FCSTD DOCUMENT  (FreeCAD 0.20R29410 (Git))
Label: SRSv1_0
License: All rights reserved
LicenseURL: http://en.wikipedia.org/wiki/All_rights_reserved
objects: Part::Feature×157, Sketcher::SketchObject×90, App::Part×59, Part::MultiFuse×49, Part::Cylinder×49, Part::Fillet×48, Part::Cut×36, Part::Loft×34, Part::Extrusion×19, Part::Sphere×4, Part::Box×2, Part::MultiCommon×1, Part::Compound×1
note: 490 computed .brp shape members not serialized (recipe doc carries the construction recipe); baked Part::Feature solids carry a one-line shape summary decoded from their .brp

FEATURE [Part::Feature] Part__Feature049  label="T-SlottedFramingScew"
  Placement = pos=(-0.00808436,-263.233,14.5255) rot=(0.577273,-0.577389,-0.577389;2.09434rad)
  shape: bbox 11.25 x 25.4 x 17.44 mm, 56 faces, 2 solids (baked)
FEATURE [Part::Feature] Part__Feature022  label="3136N138_T-Slotted Framing"
  shape: bbox 101.6 x 133.4 x 139.7 mm, 136 faces (baked)
FEATURE [Part::Feature] Part__Feature023  label="47065T801_T-Slotted Framing"
  Placement = pos=(0,100,0) rot=(-1,0,0;1.5708rad)
  shape: bbox 25.4 x 152.4 x 25.4 mm, 108 faces (baked)
FEATURE [Part::Feature] Part__Feature024  label="47065T801_T-Slotted Framing001"
  Placement = pos=(0,200,0) rot=(-1,0,0;1.5708rad)
  shape: bbox 25.4 x 152.4 x 25.4 mm, 108 faces (baked)
FEATURE [Part::MultiFuse] Fusion008  label="framingSupport"
  Placement = pos=(0,0,-3) rot=(0,0,1;3.14159rad)
  Shapes = -> [Part__Feature024,Part__Feature022,Part__Feature023]
FEATURE [Part::Box] Box  label="Cube"
  AttacherType = Attacher::AttachEngine3D
  Height = 12
  Length = 24
  Placement = pos=(-12,-341.5,-244.5) rot=(0,0,1;0rad)
  Width = 23
FEATURE [Part::Box] Box042  label="Cube030"
  AttacherType = Attacher::AttachEngine3D
  Height = 50
  Length = 25
  Placement = pos=(-11,-309,-310) rot=(0,0,1;0rad)
  Width = 25
FEATURE [Part::Cylinder] Cylinder
  Angle = 360
  AttacherType = Attacher::AttachEngine3D
  FirstAngle = 0
  Height = 15
  Placement = pos=(0,-287.79,-241.35) rot=(1,0,0;0.698132rad)
  Radius = 1.63
  SecondAngle = 0
FEATURE [Part::Cylinder] Cylinder128  label="base013"
  Angle = 360
  AttacherType = Attacher::AttachEngine3D
  FirstAngle = 0
  Height = 4.5
  Placement = pos=(136,0,65) rot=(0,0,1;0rad)
  Radius = 40
  SecondAngle = 0
FEATURE [Part::Cylinder] Cylinder129  label="baseCut002"
  Angle = 360
  AttacherType = Attacher::AttachEngine3D
  FirstAngle = 0
  Height = 7
  Placement = pos=(5,0,74) rot=(0,0,1;0rad)
  Radius = 24
  SecondAngle = 0
FEATURE [Part::Cylinder] Cylinder130
  Angle = 360
  AttacherType = Attacher::AttachEngine3D
  FirstAngle = 0
  Height = 1
  Placement = pos=(134,32.6,65) rot=(0,0,1;0rad)
  Radius = 5.5
  SecondAngle = 0
FEATURE [Part::Cylinder] Cylinder131
  Angle = 360
  AttacherType = Attacher::AttachEngine3D
  FirstAngle = 0
  Height = 5.82
  Placement = pos=(0,-21,0) rot=(0,0,1;0rad)
  Radius = 5
  SecondAngle = 0
FEATURE [Part::Cylinder] Cylinder132
  Angle = 360
  AttacherType = Attacher::AttachEngine3D
  FirstAngle = 0
  Height = 5.82
  Placement = pos=(20.5,-21,0) rot=(0,0,1;0rad)
  Radius = 5
  SecondAngle = 0
  expr: Radius = 5
FEATURE [Part::Cylinder] Cylinder133
  Angle = 360
  AttacherType = Attacher::AttachEngine3D
  FirstAngle = 0
  Height = 5.82
  Placement = pos=(0,-21,0) rot=(0,0,1;0rad)
  Radius = 5
  SecondAngle = 0
FEATURE [Part::Cylinder] Cylinder134
  Angle = 360
  AttacherType = Attacher::AttachEngine3D
  FirstAngle = 0
  Height = 5.82
  Placement = pos=(20.5,-21,0) rot=(0,0,1;0rad)
  Radius = 5
  SecondAngle = 0
FEATURE [Part::Cylinder] Cylinder139
  Angle = 360
  AttacherType = Attacher::AttachEngine3D
  FirstAngle = 0
  Height = 10
  Placement = pos=(0,-21,0) rot=(0,0,1;0rad)
  Radius = 2
  SecondAngle = 0
FEATURE [Part::Cylinder] Cylinder140
  Angle = 360
  AttacherType = Attacher::AttachEngine3D
  FirstAngle = 0
  Height = 10
  Placement = pos=(20.5,-21,0) rot=(0,0,1;0rad)
  Radius = 2
  SecondAngle = 0
FEATURE [Part::Cylinder] Cylinder141
  Angle = 360
  AttacherType = Attacher::AttachEngine3D
  FirstAngle = 0
  Height = 10
  Placement = pos=(0,-21,0) rot=(0,0,1;0rad)
  Radius = 2
  SecondAngle = 0
FEATURE [Part::Cylinder] Cylinder142
  Angle = 360
  AttacherType = Attacher::AttachEngine3D
  FirstAngle = 0
  Height = 10
  Placement = pos=(20.5,-21,0) rot=(0,0,1;0rad)
  Radius = 2
  SecondAngle = 0
FEATURE [Part::Cylinder] Cylinder143  label="WireCut003"
  Angle = 360
  AttacherType = Attacher::AttachEngine3D
  FirstAngle = 0
  Height = 60
  Placement = pos=(134,32.6,20) rot=(0,0,1;0rad)
  Radius = 2.5
  SecondAngle = 0
FEATURE [Part::Cylinder] Cylinder146
  Angle = 360
  AttacherType = Attacher::AttachEngine3D
  FirstAngle = 0
  Height = 50
  Placement = pos=(0,-302.012,-276.116) rot=(1,0,0;0.733038rad)
  Radius = 8
  SecondAngle = 0
FEATURE [Part::Cut] Cut039
  Base = -> Cylinder146
  Tool = -> Box
FEATURE [Part::Cylinder] Cylinder147  label="cut"
  Angle = 360
  AttacherType = Attacher::AttachEngine3D
  FirstAngle = 0
  Height = 50
  Placement = pos=(0,-300.005,-278.345) rot=(1,0,0;0.733038rad)
  Radius = 5
  SecondAngle = 0
FEATURE [Part::Cylinder] Cylinder148  label="m2HeatSetInsets016"
  Angle = 360
  AttacherType = Attacher::AttachEngine3D
  FirstAngle = 0
  Height = 10
  Placement = pos=(-35,0,65) rot=(0,0,1;0rad)
  Radius = 2
  SecondAngle = 0
  expr: Radius = 2
FEATURE [Part::Cylinder] Cylinder149  label="m2HeatSetInsets017"
  Angle = 360
  AttacherType = Attacher::AttachEngine3D
  FirstAngle = 0
  Height = 10
  Placement = pos=(35,0,65) rot=(0,0,1;0rad)
  Radius = 2
  SecondAngle = 0
FEATURE [Part::Cylinder] Cylinder150  label="m2HeatSetInsets018"
  Angle = 360
  AttacherType = Attacher::AttachEngine3D
  FirstAngle = 0
  Height = 10
  Placement = pos=(0,35,65) rot=(0,0,1;0rad)
  Radius = 2
  SecondAngle = 0
FEATURE [Part::Cylinder] Cylinder151  label="m2HeatSetInsets019"
  Angle = 360
  AttacherType = Attacher::AttachEngine3D
  FirstAngle = 0
  Height = 10
  Placement = pos=(0,-35,65) rot=(0,0,1;0rad)
  Radius = 2
  SecondAngle = 0
  expr: Radius = 2
FEATURE [Part::MultiFuse] Fusion079  label="m3HeatSetCuts015"
  Placement = pos=(-5,39,70) rot=(0,0,1;0rad)
  Shapes = -> [Cylinder132,Cylinder131]
FEATURE [Part::MultiFuse] Fusion080  label="m3HeatSetCuts016"
  Placement = pos=(-5,3,70) rot=(0,0,1;0rad)
  Shapes = -> [Cylinder134,Cylinder133]
FEATURE [Part::MultiFuse] Fusion081  label="m3HeatSetCuts017"
  Placement = pos=(128.75,10,-1) rot=(0,0,1;0rad)
  Shapes = -> [Fusion080,Fusion079]
FEATURE [Part::MultiFuse] Fusion086  label="m3HeatSetCuts019"
  Placement = pos=(-5,39,70) rot=(0,0,1;0rad)
  Shapes = -> [Cylinder140,Cylinder139]
FEATURE [Part::MultiFuse] Fusion087  label="m3HeatSetCuts020"
  Placement = pos=(-5,3,70) rot=(0,0,1;0rad)
  Shapes = -> [Cylinder142,Cylinder141]
FEATURE [Part::MultiFuse] Fusion085  label="m3HeatSetCuts018"
  Placement = pos=(128.75,10,-1) rot=(0,0,1;0rad)
  Shapes = -> [Fusion087,Fusion086]
FEATURE [Part::MultiFuse] Fusion088  label="lightModuleCut004"
  Shapes = -> [Fusion085,Cylinder143]
FEATURE [Part::MultiFuse] Fusion092
  Placement = pos=(0,-350,-314) rot=(0,0,-1;0.785398rad)
  Shapes = -> [Cylinder148,Cylinder149,Cylinder150,Cylinder151]
FEATURE [Part::Feature] Part__Feature153  label="logoTopCut"
  Placement = pos=(-30.8,-333,-323.9) rot=(0,0,1;0rad)
  shape: bbox 22.79 x 8 x 17.08 mm, 886 faces (baked)
FEATURE [Sketcher::SketchObject] Sketch003  label="inner"
  FullyConstrained = true
  Placement = pos=(0,0,-259.26) rot=(0,0,1;0rad)
  sketch-geometry (4):
    g0: LineSegment StartX=-30 StartY=-277 StartZ=0 EndX=-30 EndY=-327 EndZ=0
    g1: LineSegment StartX=-30 StartY=-327 StartZ=0 EndX=30 EndY=-327 EndZ=0
    g2: LineSegment StartX=30 StartY=-327 StartZ=0 EndX=30 EndY=-277 EndZ=0
    g3: LineSegment StartX=30 StartY=-277 StartZ=0 EndX=-30 EndY=-277 EndZ=0
  constraints (12):
    c: Vertical(g0)
    c: Coincident(g1,g0)
    c: Horizontal(g1)
    c: Coincident(g2,g1)
    c: Vertical(g2)
    c: Coincident(g3,g2)
    c: Coincident(g3,g0)
    c: Horizontal(g3)
    c: DistanceX(g0) = -30
    c: DistanceX(g1) = 30
    c: DistanceY(g0) = -327
    c: DistanceY(g0,g0) = 50
FEATURE [Sketcher::SketchObject] Sketch004  label="outer"
  FullyConstrained = true
  Placement = pos=(0,0,-281.2) rot=(0,0,1;0rad)
  sketch-geometry (4):
    g0: LineSegment StartX=-59 StartY=-252 StartZ=0 EndX=-59 EndY=-352 EndZ=0
    g1: LineSegment StartX=-59 StartY=-352 StartZ=0 EndX=59 EndY=-352 EndZ=0
    g2: LineSegment StartX=59 StartY=-352 StartZ=0 EndX=59 EndY=-252 EndZ=0
    g3: LineSegment StartX=59 StartY=-252 StartZ=0 EndX=-59 EndY=-252 EndZ=0
  constraints (12):
    c: Vertical(g0)
    c: Coincident(g1,g0)
    c: Horizontal(g1)
    c: Coincident(g2,g1)
    c: Vertical(g2)
    c: Coincident(g3,g2)
    c: Coincident(g3,g0)
    c: Horizontal(g3)
    c: DistanceX(g0) = -59
    c: DistanceX(g1) = 59
    c: DistanceY(g0) = -352
    c: DistanceY(g0,g0) = 100
FEATURE [Part::Loft] Loft
  Closed = false
  MaxDegree = 5
  Ruled = false
  Sections = -> [Sketch003,Sketch004]
  Solid = true
FEATURE [Part::Fillet] Fillet
  Base = -> Loft
  Edges = 12 edges r=3: [Edge1,Edge2,Edge3,Edge4,Edge5,Edge6,Edge7,Edge8,Edge9,Edge10,Edge11,Edge12]
FEATURE [Sketcher::SketchObject] Sketch005  label="inner001"
  FullyConstrained = true
  Placement = pos=(0,0,-259.26) rot=(0,0,1;0rad)
  sketch-geometry (4):
    g0: LineSegment StartX=-30 StartY=-277 StartZ=0 EndX=-30 EndY=-327 EndZ=0
    g1: LineSegment StartX=-30 StartY=-327 StartZ=0 EndX=30 EndY=-327 EndZ=0
    g2: LineSegment StartX=30 StartY=-327 StartZ=0 EndX=30 EndY=-277 EndZ=0
    g3: LineSegment StartX=30 StartY=-277 StartZ=0 EndX=-30 EndY=-277 EndZ=0
  constraints (12):
    c: Vertical(g0)
    c: Coincident(g1,g0)
    c: Horizontal(g1)
    c: Coincident(g2,g1)
    c: Vertical(g2)
    c: Coincident(g3,g2)
    c: Coincident(g3,g0)
    c: Horizontal(g3)
    c: DistanceX(g0) = -30
    c: DistanceX(g1) = 30
    c: DistanceY(g0) = -327
    c: DistanceY(g0,g0) = 50
FEATURE [Sketcher::SketchObject] Sketch006  label="outer001"
  FullyConstrained = true
  Placement = pos=(0,0,-281.2) rot=(0,0,1;0rad)
  sketch-geometry (4):
    g0: LineSegment StartX=-59 StartY=-252 StartZ=0 EndX=-59 EndY=-352 EndZ=0
    g1: LineSegment StartX=-59 StartY=-352 StartZ=0 EndX=59 EndY=-352 EndZ=0
    g2: LineSegment StartX=59 StartY=-352 StartZ=0 EndX=59 EndY=-252 EndZ=0
    g3: LineSegment StartX=59 StartY=-252 StartZ=0 EndX=-59 EndY=-252 EndZ=0
  constraints (12):
    c: Vertical(g0)
    c: Coincident(g1,g0)
    c: Horizontal(g1)
    c: Coincident(g2,g1)
    c: Vertical(g2)
    c: Coincident(g3,g2)
    c: Coincident(g3,g0)
    c: Horizontal(g3)
    c: DistanceX(g0) = -59
    c: DistanceX(g1) = 59
    c: DistanceY(g0) = -352
    c: DistanceY(g0,g0) = 100
FEATURE [Part::Loft] Loft001
  Closed = false
  MaxDegree = 5
  Ruled = false
  Sections = -> [Sketch005,Sketch006]
  Solid = true
FEATURE [Part::Fillet] Fillet009
  Base = -> Loft001
  Edges = 12 edges r=3: [Edge1,Edge2,Edge3,Edge4,Edge5,Edge6,Edge7,Edge8,Edge9,Edge10,Edge11,Edge12]
  Placement = pos=(0,0,-4) rot=(0,0,1;0rad)
FEATURE [Part::Cut] Cut  label="sls01"
  Base = -> Fillet
  Tool = -> Fillet009
FEATURE [Sketcher::SketchObject] Sketch007  label="inner002"
  FullyConstrained = true
  Placement = pos=(0,0,-259.26) rot=(0,0,1;0rad)
  sketch-geometry (4):
    g0: LineSegment StartX=-30 StartY=-277 StartZ=0 EndX=-30 EndY=-327 EndZ=0
    g1: LineSegment StartX=-30 StartY=-327 StartZ=0 EndX=30 EndY=-327 EndZ=0
    g2: LineSegment StartX=30 StartY=-327 StartZ=0 EndX=30 EndY=-277 EndZ=0
    g3: LineSegment StartX=30 StartY=-277 StartZ=0 EndX=-30 EndY=-277 EndZ=0
  constraints (12):
    c: Vertical(g0)
    c: Coincident(g1,g0)
    c: Horizontal(g1)
    c: Coincident(g2,g1)
    c: Vertical(g2)
    c: Coincident(g3,g2)
    c: Coincident(g3,g0)
    c: Horizontal(g3)
    c: DistanceX(g0) = -30
    c: DistanceX(g1) = 30
    c: DistanceY(g0) = -327
    c: DistanceY(g0,g0) = 50
FEATURE [Sketcher::SketchObject] Sketch008  label="outer002"
  FullyConstrained = true
  Placement = pos=(0,0,-281.2) rot=(0,0,1;0rad)
  sketch-geometry (4):
    g0: LineSegment StartX=-59 StartY=-252 StartZ=0 EndX=-59 EndY=-352 EndZ=0
    g1: LineSegment StartX=-59 StartY=-352 StartZ=0 EndX=59 EndY=-352 EndZ=0
    g2: LineSegment StartX=59 StartY=-352 StartZ=0 EndX=59 EndY=-252 EndZ=0
    g3: LineSegment StartX=59 StartY=-252 StartZ=0 EndX=-59 EndY=-252 EndZ=0
  constraints (12):
    c: Vertical(g0)
    c: Coincident(g1,g0)
    c: Horizontal(g1)
    c: Coincident(g2,g1)
    c: Vertical(g2)
    c: Coincident(g3,g2)
    c: Coincident(g3,g0)
    c: Horizontal(g3)
    c: DistanceX(g0) = -59
    c: DistanceX(g1) = 59
    c: DistanceY(g0) = -352
    c: DistanceY(g0,g0) = 100
FEATURE [Part::Loft] Loft002
  Closed = false
  MaxDegree = 5
  Ruled = false
  Sections = -> [Sketch007,Sketch008]
  Solid = true
FEATURE [Part::Fillet] Fillet010
  Base = -> Loft002
  Edges = 12 edges r=3: [Edge1,Edge2,Edge3,Edge4,Edge5,Edge6,Edge7,Edge8,Edge9,Edge10,Edge11,Edge12]
FEATURE [Sketcher::SketchObject] Sketch009  label="inner003"
  FullyConstrained = true
  Placement = pos=(0,0,-259.26) rot=(0,0,1;0rad)
  sketch-geometry (4):
    g0: LineSegment StartX=-30 StartY=-277 StartZ=0 EndX=-30 EndY=-327 EndZ=0
    g1: LineSegment StartX=-30 StartY=-327 StartZ=0 EndX=30 EndY=-327 EndZ=0
    g2: LineSegment StartX=30 StartY=-327 StartZ=0 EndX=30 EndY=-277 EndZ=0
    g3: LineSegment StartX=30 StartY=-277 StartZ=0 EndX=-30 EndY=-277 EndZ=0
  constraints (12):
    c: Vertical(g0)
    c: Coincident(g1,g0)
    c: Horizontal(g1)
    c: Coincident(g2,g1)
    c: Vertical(g2)
    c: Coincident(g3,g2)
    c: Coincident(g3,g0)
    c: Horizontal(g3)
    c: DistanceX(g0) = -30
    c: DistanceX(g1) = 30
    c: DistanceY(g0) = -327
    c: DistanceY(g0,g0) = 50
FEATURE [Sketcher::SketchObject] Sketch010  label="outer003"
  FullyConstrained = true
  Placement = pos=(0,0,-281.2) rot=(0,0,1;0rad)
  sketch-geometry (4):
    g0: LineSegment StartX=-59 StartY=-252 StartZ=0 EndX=-59 EndY=-352 EndZ=0
    g1: LineSegment StartX=-59 StartY=-352 StartZ=0 EndX=59 EndY=-352 EndZ=0
    g2: LineSegment StartX=59 StartY=-352 StartZ=0 EndX=59 EndY=-252 EndZ=0
    g3: LineSegment StartX=59 StartY=-252 StartZ=0 EndX=-59 EndY=-252 EndZ=0
  constraints (12):
    c: Vertical(g0)
    c: Coincident(g1,g0)
    c: Horizontal(g1)
    c: Coincident(g2,g1)
    c: Vertical(g2)
    c: Coincident(g3,g2)
    c: Coincident(g3,g0)
    c: Horizontal(g3)
    c: DistanceX(g0) = -59
    c: DistanceX(g1) = 59
    c: DistanceY(g0) = -352
    c: DistanceY(g0,g0) = 100
FEATURE [Part::Loft] Loft003
  Closed = false
  MaxDegree = 5
  Ruled = false
  Sections = -> [Sketch009,Sketch010]
  Solid = true
FEATURE [Part::Fillet] Fillet011
  Base = -> Loft003
  Edges = 12 edges r=3: [Edge1,Edge2,Edge3,Edge4,Edge5,Edge6,Edge7,Edge8,Edge9,Edge10,Edge11,Edge12]
  Placement = pos=(0,0,-4) rot=(0,0,1;0rad)
FEATURE [Part::Cut] Cut004  label="sls002"
  Base = -> Fillet010
  Placement = pos=(0,0,-16) rot=(0,0,1;0rad)
  Tool = -> Fillet011
FEATURE [Sketcher::SketchObject] Sketch011  label="inner004"
  FullyConstrained = true
  Placement = pos=(0,0,-259.26) rot=(0,0,1;0rad)
  sketch-geometry (4):
    g0: LineSegment StartX=-30 StartY=-277 StartZ=0 EndX=-30 EndY=-327 EndZ=0
    g1: LineSegment StartX=-30 StartY=-327 StartZ=0 EndX=30 EndY=-327 EndZ=0
    g2: LineSegment StartX=30 StartY=-327 StartZ=0 EndX=30 EndY=-277 EndZ=0
    g3: LineSegment StartX=30 StartY=-277 StartZ=0 EndX=-30 EndY=-277 EndZ=0
  constraints (12):
    c: Vertical(g0)
    c: Coincident(g1,g0)
    c: Horizontal(g1)
    c: Coincident(g2,g1)
    c: Vertical(g2)
    c: Coincident(g3,g2)
    c: Coincident(g3,g0)
    c: Horizontal(g3)
    c: DistanceX(g0) = -30
    c: DistanceX(g1) = 30
    c: DistanceY(g0) = -327
    c: DistanceY(g0,g0) = 50
FEATURE [Sketcher::SketchObject] Sketch012  label="outer004"
  FullyConstrained = true
  Placement = pos=(0,0,-281.2) rot=(0,0,1;0rad)
  sketch-geometry (4):
    g0: LineSegment StartX=-59 StartY=-252 StartZ=0 EndX=-59 EndY=-352 EndZ=0
    g1: LineSegment StartX=-59 StartY=-352 StartZ=0 EndX=59 EndY=-352 EndZ=0
    g2: LineSegment StartX=59 StartY=-352 StartZ=0 EndX=59 EndY=-252 EndZ=0
    g3: LineSegment StartX=59 StartY=-252 StartZ=0 EndX=-59 EndY=-252 EndZ=0
  constraints (12):
    c: Vertical(g0)
    c: Coincident(g1,g0)
    c: Horizontal(g1)
    c: Coincident(g2,g1)
    c: Vertical(g2)
    c: Coincident(g3,g2)
    c: Coincident(g3,g0)
    c: Horizontal(g3)
    c: DistanceX(g0) = -59
    c: DistanceX(g1) = 59
    c: DistanceY(g0) = -352
    c: DistanceY(g0,g0) = 100
FEATURE [Part::Loft] Loft004
  Closed = false
  MaxDegree = 5
  Ruled = false
  Sections = -> [Sketch011,Sketch012]
  Solid = true
FEATURE [Part::Fillet] Fillet012
  Base = -> Loft004
  Edges = 12 edges r=3: [Edge1,Edge2,Edge3,Edge4,Edge5,Edge6,Edge7,Edge8,Edge9,Edge10,Edge11,Edge12]
FEATURE [Sketcher::SketchObject] Sketch013  label="inner005"
  FullyConstrained = true
  Placement = pos=(0,0,-259.26) rot=(0,0,1;0rad)
  sketch-geometry (4):
    g0: LineSegment StartX=-30 StartY=-277 StartZ=0 EndX=-30 EndY=-327 EndZ=0
    g1: LineSegment StartX=-30 StartY=-327 StartZ=0 EndX=30 EndY=-327 EndZ=0
    g2: LineSegment StartX=30 StartY=-327 StartZ=0 EndX=30 EndY=-277 EndZ=0
    g3: LineSegment StartX=30 StartY=-277 StartZ=0 EndX=-30 EndY=-277 EndZ=0
  constraints (12):
    c: Vertical(g0)
    c: Coincident(g1,g0)
    c: Horizontal(g1)
    c: Coincident(g2,g1)
    c: Vertical(g2)
    c: Coincident(g3,g2)
    c: Coincident(g3,g0)
    c: Horizontal(g3)
    c: DistanceX(g0) = -30
    c: DistanceX(g1) = 30
    c: DistanceY(g0) = -327
    c: DistanceY(g0,g0) = 50
FEATURE [Sketcher::SketchObject] Sketch014  label="outer005"
  FullyConstrained = true
  Placement = pos=(0,0,-281.2) rot=(0,0,1;0rad)
  sketch-geometry (4):
    g0: LineSegment StartX=-59 StartY=-252 StartZ=0 EndX=-59 EndY=-352 EndZ=0
    g1: LineSegment StartX=-59 StartY=-352 StartZ=0 EndX=59 EndY=-352 EndZ=0
    g2: LineSegment StartX=59 StartY=-352 StartZ=0 EndX=59 EndY=-252 EndZ=0
    g3: LineSegment StartX=59 StartY=-252 StartZ=0 EndX=-59 EndY=-252 EndZ=0
  constraints (12):
    c: Vertical(g0)
    c: Coincident(g1,g0)
    c: Horizontal(g1)
    c: Coincident(g2,g1)
    c: Vertical(g2)
    c: Coincident(g3,g2)
    c: Coincident(g3,g0)
    c: Horizontal(g3)
    c: DistanceX(g0) = -59
    c: DistanceX(g1) = 59
    c: DistanceY(g0) = -352
    c: DistanceY(g0,g0) = 100
FEATURE [Part::Loft] Loft005
  Closed = false
  MaxDegree = 5
  Ruled = false
  Sections = -> [Sketch013,Sketch014]
  Solid = true
FEATURE [Part::Fillet] Fillet013
  Base = -> Loft005
  Edges = 12 edges r=3: [Edge1,Edge2,Edge3,Edge4,Edge5,Edge6,Edge7,Edge8,Edge9,Edge10,Edge11,Edge12]
  Placement = pos=(0,0,-4) rot=(0,0,1;0rad)
FEATURE [Part::Cut] Cut005  label="sls003"
  Base = -> Fillet012
  Placement = pos=(0,0,-32) rot=(0,0,1;0rad)
  Tool = -> Fillet013
FEATURE [Sketcher::SketchObject] Sketch015  label="inner006"
  FullyConstrained = true
  Placement = pos=(0,0,-259.26) rot=(0,0,1;0rad)
  sketch-geometry (4):
    g0: LineSegment StartX=-30 StartY=-277 StartZ=0 EndX=-30 EndY=-327 EndZ=0
    g1: LineSegment StartX=-30 StartY=-327 StartZ=0 EndX=30 EndY=-327 EndZ=0
    g2: LineSegment StartX=30 StartY=-327 StartZ=0 EndX=30 EndY=-277 EndZ=0
    g3: LineSegment StartX=30 StartY=-277 StartZ=0 EndX=-30 EndY=-277 EndZ=0
  constraints (12):
    c: Vertical(g0)
    c: Coincident(g1,g0)
    c: Horizontal(g1)
    c: Coincident(g2,g1)
    c: Vertical(g2)
    c: Coincident(g3,g2)
    c: Coincident(g3,g0)
    c: Horizontal(g3)
    c: DistanceX(g0) = -30
    c: DistanceX(g1) = 30
    c: DistanceY(g0) = -327
    c: DistanceY(g0,g0) = 50
FEATURE [Sketcher::SketchObject] Sketch016  label="outer006"
  FullyConstrained = true
  Placement = pos=(0,0,-281.2) rot=(0,0,1;0rad)
  sketch-geometry (4):
    g0: LineSegment StartX=-59 StartY=-252 StartZ=0 EndX=-59 EndY=-352 EndZ=0
    g1: LineSegment StartX=-59 StartY=-352 StartZ=0 EndX=59 EndY=-352 EndZ=0
    g2: LineSegment StartX=59 StartY=-352 StartZ=0 EndX=59 EndY=-252 EndZ=0
    g3: LineSegment StartX=59 StartY=-252 StartZ=0 EndX=-59 EndY=-252 EndZ=0
  constraints (12):
    c: Vertical(g0)
    c: Coincident(g1,g0)
    c: Horizontal(g1)
    c: Coincident(g2,g1)
    c: Vertical(g2)
    c: Coincident(g3,g2)
    c: Coincident(g3,g0)
    c: Horizontal(g3)
    c: DistanceX(g0) = -59
    c: DistanceX(g1) = 59
    c: DistanceY(g0) = -352
    c: DistanceY(g0,g0) = 100
FEATURE [Part::Loft] Loft006
  Closed = false
  MaxDegree = 5
  Ruled = false
  Sections = -> [Sketch015,Sketch016]
  Solid = true
FEATURE [Part::Fillet] Fillet014
  Base = -> Loft006
  Edges = 12 edges r=3: [Edge1,Edge2,Edge3,Edge4,Edge5,Edge6,Edge7,Edge8,Edge9,Edge10,Edge11,Edge12]
FEATURE [Sketcher::SketchObject] Sketch017  label="inner007"
  FullyConstrained = true
  Placement = pos=(0,0,-259.26) rot=(0,0,1;0rad)
  sketch-geometry (4):
    g0: LineSegment StartX=-30 StartY=-277 StartZ=0 EndX=-30 EndY=-327 EndZ=0
    g1: LineSegment StartX=-30 StartY=-327 StartZ=0 EndX=30 EndY=-327 EndZ=0
    g2: LineSegment StartX=30 StartY=-327 StartZ=0 EndX=30 EndY=-277 EndZ=0
    g3: LineSegment StartX=30 StartY=-277 StartZ=0 EndX=-30 EndY=-277 EndZ=0
  constraints (12):
    c: Vertical(g0)
    c: Coincident(g1,g0)
    c: Horizontal(g1)
    c: Coincident(g2,g1)
    c: Vertical(g2)
    c: Coincident(g3,g2)
    c: Coincident(g3,g0)
    c: Horizontal(g3)
    c: DistanceX(g0) = -30
    c: DistanceX(g1) = 30
    c: DistanceY(g0) = -327
    c: DistanceY(g0,g0) = 50
FEATURE [Sketcher::SketchObject] Sketch018  label="outer007"
  FullyConstrained = true
  Placement = pos=(0,0,-281.2) rot=(0,0,1;0rad)
  sketch-geometry (4):
    g0: LineSegment StartX=-59 StartY=-252 StartZ=0 EndX=-59 EndY=-352 EndZ=0
    g1: LineSegment StartX=-59 StartY=-352 StartZ=0 EndX=59 EndY=-352 EndZ=0
    g2: LineSegment StartX=59 StartY=-352 StartZ=0 EndX=59 EndY=-252 EndZ=0
    g3: LineSegment StartX=59 StartY=-252 StartZ=0 EndX=-59 EndY=-252 EndZ=0
  constraints (12):
    c: Vertical(g0)
    c: Coincident(g1,g0)
    c: Horizontal(g1)
    c: Coincident(g2,g1)
    c: Vertical(g2)
    c: Coincident(g3,g2)
    c: Coincident(g3,g0)
    c: Horizontal(g3)
    c: DistanceX(g0) = -59
    c: DistanceX(g1) = 59
    c: DistanceY(g0) = -352
    c: DistanceY(g0,g0) = 100
FEATURE [Part::Loft] Loft007
  Closed = false
  MaxDegree = 5
  Ruled = false
  Sections = -> [Sketch017,Sketch018]
  Solid = true
FEATURE [Part::Fillet] Fillet015
  Base = -> Loft007
  Edges = 12 edges r=3: [Edge1,Edge2,Edge3,Edge4,Edge5,Edge6,Edge7,Edge8,Edge9,Edge10,Edge11,Edge12]
  Placement = pos=(0,0,-4) rot=(0,0,1;0rad)
FEATURE [Part::Cut] Cut006  label="sls004"
  Base = -> Fillet014
  Placement = pos=(0,0,-48) rot=(0,0,1;0rad)
  Tool = -> Fillet015
FEATURE [Part::MultiFuse] Fusion036  label="slsBottom"
  Shapes = -> [Cut006,Cut005]
FEATURE [Sketcher::SketchObject] Sketch023
  FullyConstrained = true
  sketch-geometry (4):
    g0: Circle CenterX=-35 CenterY=-332 CenterZ=0 NormalX=0 NormalY=0 NormalZ=1 AngleXU=0 Radius=5.5
    g1: Circle CenterX=35 CenterY=-332 CenterZ=0 NormalX=0 NormalY=0 NormalZ=1 AngleXU=0 Radius=5.5
    g2: Circle CenterX=35 CenterY=-272 CenterZ=0 NormalX=0 NormalY=0 NormalZ=1 AngleXU=0 Radius=5.5
    g3: Circle CenterX=-35 CenterY=-272 CenterZ=0 NormalX=0 NormalY=0 NormalZ=1 AngleXU=0 Radius=5.5
  constraints (12):
    c: DistanceX(g0) = -35
    c: DistanceY(g0) = -332
    c: Equal(g0,g3)
    c: Equal(g0,g2)
    c: Equal(g0,g1)
    c: Diameter(g0) = 11
    c: DistanceX(g3,g0) = 0
    c: DistanceY(g0,g3) = 60
    c: DistanceY(g2,g3) = 0
    c: DistanceY(g0,g1) = 0
    c: DistanceX(g2,g1) = 0
    c: DistanceX(g1) = 35
FEATURE [Part::Extrusion] Extrude007  label="stands"
  Base = -> Sketch023
  Dir = (0,0,1)
  DirMode = 2
  FaceMakerClass = Part::FaceMakerBullseye
  LengthFwd = 69
  LengthRev = 0
  Placement = pos=(0,0,-323) rot=(0,0,1;0rad)
  Solid = true
  Symmetric = false
FEATURE [Sketcher::SketchObject] Sketch024  label="inner008"
  FullyConstrained = true
  Placement = pos=(0,0,-259.26) rot=(0,0,1;0rad)
  sketch-geometry (4):
    g0: LineSegment StartX=-30 StartY=-277 StartZ=0 EndX=-30 EndY=-327 EndZ=0
    g1: LineSegment StartX=-30 StartY=-327 StartZ=0 EndX=30 EndY=-327 EndZ=0
    g2: LineSegment StartX=30 StartY=-327 StartZ=0 EndX=30 EndY=-277 EndZ=0
    g3: LineSegment StartX=30 StartY=-277 StartZ=0 EndX=-30 EndY=-277 EndZ=0
  constraints (12):
    c: Vertical(g0)
    c: Coincident(g1,g0)
    c: Horizontal(g1)
    c: Coincident(g2,g1)
    c: Vertical(g2)
    c: Coincident(g3,g2)
    c: Coincident(g3,g0)
    c: Horizontal(g3)
    c: DistanceX(g0) = -30
    c: DistanceX(g1) = 30
    c: DistanceY(g0) = -327
    c: DistanceY(g0,g0) = 50
FEATURE [Sketcher::SketchObject] Sketch025  label="outer008"
  FullyConstrained = true
  Placement = pos=(0,0,-281.2) rot=(0,0,1;0rad)
  sketch-geometry (4):
    g0: LineSegment StartX=-59 StartY=-252 StartZ=0 EndX=-59 EndY=-352 EndZ=0
    g1: LineSegment StartX=-59 StartY=-352 StartZ=0 EndX=59 EndY=-352 EndZ=0
    g2: LineSegment StartX=59 StartY=-352 StartZ=0 EndX=59 EndY=-252 EndZ=0
    g3: LineSegment StartX=59 StartY=-252 StartZ=0 EndX=-59 EndY=-252 EndZ=0
  constraints (12):
    c: Vertical(g0)
    c: Coincident(g1,g0)
    c: Horizontal(g1)
    c: Coincident(g2,g1)
    c: Vertical(g2)
    c: Coincident(g3,g2)
    c: Coincident(g3,g0)
    c: Horizontal(g3)
    c: DistanceX(g0) = -59
    c: DistanceX(g1) = 59
    c: DistanceY(g0) = -352
    c: DistanceY(g0,g0) = 100
FEATURE [Part::Loft] Loft008
  Closed = false
  MaxDegree = 5
  Ruled = false
  Sections = -> [Sketch024,Sketch025]
  Solid = true
FEATURE [Part::Fillet] Fillet016
  Base = -> Loft008
  Edges = 12 edges r=3: [Edge1,Edge2,Edge3,Edge4,Edge5,Edge6,Edge7,Edge8,Edge9,Edge10,Edge11,Edge12]
FEATURE [Sketcher::SketchObject] Sketch026  label="inner009"
  FullyConstrained = true
  Placement = pos=(0,0,-259.26) rot=(0,0,1;0rad)
  sketch-geometry (4):
    g0: LineSegment StartX=-30 StartY=-277 StartZ=0 EndX=-30 EndY=-327 EndZ=0
    g1: LineSegment StartX=-30 StartY=-327 StartZ=0 EndX=30 EndY=-327 EndZ=0
    g2: LineSegment StartX=30 StartY=-327 StartZ=0 EndX=30 EndY=-277 EndZ=0
    g3: LineSegment StartX=30 StartY=-277 StartZ=0 EndX=-30 EndY=-277 EndZ=0
  constraints (12):
    c: Vertical(g0)
    c: Coincident(g1,g0)
    c: Horizontal(g1)
    c: Coincident(g2,g1)
    c: Vertical(g2)
    c: Coincident(g3,g2)
    c: Coincident(g3,g0)
    c: Horizontal(g3)
    c: DistanceX(g0) = -30
    c: DistanceX(g1) = 30
    c: DistanceY(g0) = -327
    c: DistanceY(g0,g0) = 50
FEATURE [Sketcher::SketchObject] Sketch027  label="outer009"
  FullyConstrained = true
  Placement = pos=(0,0,-281.2) rot=(0,0,1;0rad)
  sketch-geometry (4):
    g0: LineSegment StartX=-59 StartY=-252 StartZ=0 EndX=-59 EndY=-352 EndZ=0
    g1: LineSegment StartX=-59 StartY=-352 StartZ=0 EndX=59 EndY=-352 EndZ=0
    g2: LineSegment StartX=59 StartY=-352 StartZ=0 EndX=59 EndY=-252 EndZ=0
    g3: LineSegment StartX=59 StartY=-252 StartZ=0 EndX=-59 EndY=-252 EndZ=0
  constraints (12):
    c: Vertical(g0)
    c: Coincident(g1,g0)
    c: Horizontal(g1)
    c: Coincident(g2,g1)
    c: Vertical(g2)
    c: Coincident(g3,g2)
    c: Coincident(g3,g0)
    c: Horizontal(g3)
    c: DistanceX(g0) = -59
    c: DistanceX(g1) = 59
    c: DistanceY(g0) = -352
    c: DistanceY(g0,g0) = 100
FEATURE [Part::Loft] Loft009
  Closed = false
  MaxDegree = 5
  Ruled = false
  Sections = -> [Sketch026,Sketch027]
  Solid = true
FEATURE [Part::Fillet] Fillet017
  Base = -> Loft009
  Edges = 12 edges r=3: [Edge1,Edge2,Edge3,Edge4,Edge5,Edge6,Edge7,Edge8,Edge9,Edge10,Edge11,Edge12]
  Placement = pos=(0,0,-4) rot=(0,0,1;0rad)
FEATURE [Part::Cut] Cut007  label="sls005"
  Base = -> Fillet016
  Placement = pos=(0,0,4) rot=(0,0,1;0rad)
  Tool = -> Fillet017
FEATURE [Sketcher::SketchObject] Sketch028  label="inner010"
  FullyConstrained = true
  Placement = pos=(0,0,-259.26) rot=(0,0,1;0rad)
  sketch-geometry (4):
    g0: LineSegment StartX=-30 StartY=-277 StartZ=0 EndX=-30 EndY=-327 EndZ=0
    g1: LineSegment StartX=-30 StartY=-327 StartZ=0 EndX=30 EndY=-327 EndZ=0
    g2: LineSegment StartX=30 StartY=-327 StartZ=0 EndX=30 EndY=-277 EndZ=0
    g3: LineSegment StartX=30 StartY=-277 StartZ=0 EndX=-30 EndY=-277 EndZ=0
  constraints (12):
    c: Vertical(g0)
    c: Coincident(g1,g0)
    c: Horizontal(g1)
    c: Coincident(g2,g1)
    c: Vertical(g2)
    c: Coincident(g3,g2)
    c: Coincident(g3,g0)
    c: Horizontal(g3)
    c: DistanceX(g0) = -30
    c: DistanceX(g1) = 30
    c: DistanceY(g0) = -327
    c: DistanceY(g0,g0) = 50
FEATURE [Sketcher::SketchObject] Sketch029  label="outer010"
  FullyConstrained = true
  Placement = pos=(0,0,-281.2) rot=(0,0,1;0rad)
  sketch-geometry (4):
    g0: LineSegment StartX=-59 StartY=-252 StartZ=0 EndX=-59 EndY=-352 EndZ=0
    g1: LineSegment StartX=-59 StartY=-352 StartZ=0 EndX=59 EndY=-352 EndZ=0
    g2: LineSegment StartX=59 StartY=-352 StartZ=0 EndX=59 EndY=-252 EndZ=0
    g3: LineSegment StartX=59 StartY=-252 StartZ=0 EndX=-59 EndY=-252 EndZ=0
  constraints (12):
    c: Vertical(g0)
    c: Coincident(g1,g0)
    c: Horizontal(g1)
    c: Coincident(g2,g1)
    c: Vertical(g2)
    c: Coincident(g3,g2)
    c: Coincident(g3,g0)
    c: Horizontal(g3)
    c: DistanceX(g0) = -59
    c: DistanceX(g1) = 59
    c: DistanceY(g0) = -352
    c: DistanceY(g0,g0) = 100
FEATURE [Part::Loft] Loft010
  Closed = false
  MaxDegree = 5
  Ruled = false
  Sections = -> [Sketch028,Sketch029]
  Solid = true
FEATURE [Part::Fillet] Fillet018
  Base = -> Loft010
  Edges = 12 edges r=3: [Edge1,Edge2,Edge3,Edge4,Edge5,Edge6,Edge7,Edge8,Edge9,Edge10,Edge11,Edge12]
FEATURE [Sketcher::SketchObject] Sketch030  label="inner011"
  FullyConstrained = true
  Placement = pos=(0,0,-259.26) rot=(0,0,1;0rad)
  sketch-geometry (4):
    g0: LineSegment StartX=-30 StartY=-277 StartZ=0 EndX=-30 EndY=-327 EndZ=0
    g1: LineSegment StartX=-30 StartY=-327 StartZ=0 EndX=30 EndY=-327 EndZ=0
    g2: LineSegment StartX=30 StartY=-327 StartZ=0 EndX=30 EndY=-277 EndZ=0
    g3: LineSegment StartX=30 StartY=-277 StartZ=0 EndX=-30 EndY=-277 EndZ=0
  constraints (12):
    c: Vertical(g0)
    c: Coincident(g1,g0)
    c: Horizontal(g1)
    c: Coincident(g2,g1)
    c: Vertical(g2)
    c: Coincident(g3,g2)
    c: Coincident(g3,g0)
    c: Horizontal(g3)
    c: DistanceX(g0) = -30
    c: DistanceX(g1) = 30
    c: DistanceY(g0) = -327
    c: DistanceY(g0,g0) = 50
FEATURE [Sketcher::SketchObject] Sketch031  label="outer011"
  FullyConstrained = true
  Placement = pos=(0,0,-281.2) rot=(0,0,1;0rad)
  sketch-geometry (4):
    g0: LineSegment StartX=-59 StartY=-252 StartZ=0 EndX=-59 EndY=-352 EndZ=0
    g1: LineSegment StartX=-59 StartY=-352 StartZ=0 EndX=59 EndY=-352 EndZ=0
    g2: LineSegment StartX=59 StartY=-352 StartZ=0 EndX=59 EndY=-252 EndZ=0
    g3: LineSegment StartX=59 StartY=-252 StartZ=0 EndX=-59 EndY=-252 EndZ=0
  constraints (12):
    c: Vertical(g0)
    c: Coincident(g1,g0)
    c: Horizontal(g1)
    c: Coincident(g2,g1)
    c: Vertical(g2)
    c: Coincident(g3,g2)
    c: Coincident(g3,g0)
    c: Horizontal(g3)
    c: DistanceX(g0) = -59
    c: DistanceX(g1) = 59
    c: DistanceY(g0) = -352
    c: DistanceY(g0,g0) = 100
FEATURE [Part::Loft] Loft011
  Closed = false
  MaxDegree = 5
  Ruled = false
  Sections = -> [Sketch030,Sketch031]
  Solid = true
FEATURE [Part::Fillet] Fillet019
  Base = -> Loft011
  Edges = 12 edges r=3: [Edge1,Edge2,Edge3,Edge4,Edge5,Edge6,Edge7,Edge8,Edge9,Edge10,Edge11,Edge12]
  Placement = pos=(0,0,-4) rot=(0,0,1;0rad)
FEATURE [Part::Cut] Cut008  label="sls006"
  Base = -> Fillet018
  Placement = pos=(0,0,7) rot=(0,0,1;0rad)
  Tool = -> Fillet019
FEATURE [Sketcher::SketchObject] Sketch033
  FullyConstrained = true
  Placement = pos=(0,0,0) rot=(1,0,0;1.5708rad)
  sketch-geometry (4):
    g0: LineSegment StartX=-22 StartY=-275.2 StartZ=0 EndX=22 EndY=-275.2 EndZ=0
    g1: LineSegment StartX=22 StartY=-275.2 StartZ=0 EndX=22 EndY=-323.5 EndZ=0
    g2: LineSegment StartX=22 StartY=-323.5 StartZ=0 EndX=-22 EndY=-323.5 EndZ=0
    g3: LineSegment StartX=-22 StartY=-323.5 StartZ=0 EndX=-22 EndY=-275.2 EndZ=0
  constraints (12):
    c: Coincident(g0,g1)
    c: Coincident(g1,g2)
    c: Coincident(g2,g3)
    c: Coincident(g3,g0)
    c: Horizontal(g0)
    c: Horizontal(g2)
    c: Vertical(g1)
    c: Vertical(g3)
    c: DistanceX(g1) = 22
    c: DistanceX(g0) = -22
    c: DistanceY(g0) = -275.2
    c: DistanceY(g2) = -323.5
FEATURE [Part::Extrusion] Extrude009  label="face"
  Base = -> Sketch033
  Dir = (0,-1,2e-16)
  DirMode = 2
  FaceMakerClass = Part::FaceMakerBullseye
  LengthFwd = 2
  LengthRev = 0
  Placement = pos=(0,-325.87,0) rot=(0,0,1;0rad)
  Solid = true
  Symmetric = false
FEATURE [Sketcher::SketchObject] Sketch034
  FullyConstrained = true
  sketch-geometry (4):
    g0: Circle CenterX=-35 CenterY=-332 CenterZ=0 NormalX=0 NormalY=0 NormalZ=1 AngleXU=0 Radius=2
    g1: Circle CenterX=35 CenterY=-332 CenterZ=0 NormalX=0 NormalY=0 NormalZ=1 AngleXU=0 Radius=2
    g2: Circle CenterX=35 CenterY=-272 CenterZ=0 NormalX=0 NormalY=0 NormalZ=1 AngleXU=0 Radius=2
    g3: Circle CenterX=-35 CenterY=-272 CenterZ=0 NormalX=0 NormalY=0 NormalZ=1 AngleXU=0 Radius=2
  constraints (12):
    c: DistanceX(g0) = -35
    c: DistanceY(g0) = -332
    c: Equal(g0,g3)
    c: Equal(g0,g2)
    c: Equal(g0,g1)
    c: Diameter(g0) = 4
    c: DistanceX(g3,g0) = 0
    c: DistanceY(g0,g3) = 60
    c: DistanceY(g2,g3) = 0
    c: DistanceY(g0,g1) = 0
    c: DistanceX(g2,g1) = 0
    c: DistanceX(g1) = 35
FEATURE [Part::Extrusion] Extrude010  label="slsCuts"
  Base = -> Sketch034
  Dir = (0,0,1)
  DirMode = 2
  FaceMakerClass = Part::FaceMakerBullseye
  LengthFwd = 20
  LengthRev = 0
  Placement = pos=(0,0,-323) rot=(0,0,1;0rad)
  Solid = true
  Symmetric = false
FEATURE [Sketcher::SketchObject] Sketch036
  FullyConstrained = true
  MapMode = 2
  sketch-geometry (4):
    g0: LineSegment StartX=-28 StartY=-347.85 StartZ=0 EndX=28 EndY=-347.85 EndZ=0
    g1: LineSegment StartX=18 StartY=-327.85 StartZ=0 EndX=28 EndY=-347.85 EndZ=0
    g2: LineSegment StartX=-28 StartY=-347.85 StartZ=0 EndX=-18 EndY=-327.85 EndZ=0
    g3: LineSegment StartX=-18 StartY=-327.85 StartZ=0 EndX=18 EndY=-327.85 EndZ=0
  constraints (12):
    c: Horizontal(g0)
    c: Coincident(g1,g0)
    c: Coincident(g2,g0)
    c: Coincident(g3,g2)
    c: Coincident(g3,g1)
    c: Horizontal(g3)
    c: DistanceX(g2) = -18
    c: DistanceX(g1) = 18
    c: DistanceX(g0,g2) = 10
    c: DistanceY(g2) = -327.85
    c: DistanceY(g0,g2) = 20
    c: DistanceX(g1,g0) = 10
FEATURE [Part::Extrusion] Extrude012
  Base = -> Sketch036
  Dir = (0,0,1)
  DirMode = 2
  FaceMakerClass = Part::FaceMakerBullseye
  LengthFwd = 40
  LengthRev = 0
  Placement = pos=(0,0,-329) rot=(0,0,1;0rad)
  Solid = true
  Symmetric = false
FEATURE [Part::Cut] Cut011  label="slsBottom001"
  Base = -> Fusion036
  Tool = -> Extrude012
FEATURE [Part::MultiFuse] Fusion037  label="sls"
  Shapes = -> [Cut011,Extrude009,Extrude007,Cut004,Cut]
FEATURE [Sketcher::SketchObject] Sketch037
  FullyConstrained = true
  sketch-geometry (4):
    g0: LineSegment StartX=-29 StartY=-278.2 StartZ=0 EndX=29 EndY=-278.2 EndZ=0
    g1: LineSegment StartX=29 StartY=-278.2 StartZ=0 EndX=29 EndY=-325.8 EndZ=0
    g2: LineSegment StartX=29 StartY=-325.8 StartZ=0 EndX=-29 EndY=-325.8 EndZ=0
    g3: LineSegment StartX=-29 StartY=-325.8 StartZ=0 EndX=-29 EndY=-278.2 EndZ=0
  constraints (12):
    c: Coincident(g0,g1)
    c: Coincident(g1,g2)
    c: Coincident(g2,g3)
    c: Coincident(g3,g0)
    c: Horizontal(g0)
    c: Horizontal(g2)
    c: Vertical(g1)
    c: Vertical(g3)
    c: DistanceX(g2) = -29
    c: DistanceY(g2) = -325.8
    c: DistanceY(g2,g0) = 47.6
    c: DistanceX(g1) = 29
FEATURE [Part::Extrusion] Extrude013  label="slsCut"
  Base = -> Sketch037
  Dir = (0,0,1)
  DirMode = 2
  FaceMakerClass = Part::FaceMakerBullseye
  LengthFwd = 60
  LengthRev = 0
  Placement = pos=(0,0,-329) rot=(0,0,1;0rad)
  Solid = true
  Symmetric = false
FEATURE [Part::Cut] Cut012  label="sls007"
  Base = -> Fusion037
  Tool = -> Extrude013
FEATURE [Sketcher::SketchObject] Sketch038  label="inner012"
  FullyConstrained = true
  Placement = pos=(0,0,-259.26) rot=(0,0,1;0rad)
  sketch-geometry (4):
    g0: LineSegment StartX=-30 StartY=-277 StartZ=0 EndX=-30 EndY=-327 EndZ=0
    g1: LineSegment StartX=-30 StartY=-327 StartZ=0 EndX=30 EndY=-327 EndZ=0
    g2: LineSegment StartX=30 StartY=-327 StartZ=0 EndX=30 EndY=-277 EndZ=0
    g3: LineSegment StartX=30 StartY=-277 StartZ=0 EndX=-30 EndY=-277 EndZ=0
  constraints (12):
    c: Vertical(g0)
    c: Coincident(g1,g0)
    c: Horizontal(g1)
    c: Coincident(g2,g1)
    c: Vertical(g2)
    c: Coincident(g3,g2)
    c: Coincident(g3,g0)
    c: Horizontal(g3)
    c: DistanceX(g0) = -30
    c: DistanceX(g1) = 30
    c: DistanceY(g0) = -327
    c: DistanceY(g0,g0) = 50
FEATURE [Sketcher::SketchObject] Sketch039  label="outer012"
  FullyConstrained = true
  Placement = pos=(0,0,-281.2) rot=(0,0,1;0rad)
  sketch-geometry (4):
    g0: LineSegment StartX=-59 StartY=-252 StartZ=0 EndX=-59 EndY=-352 EndZ=0
    g1: LineSegment StartX=-59 StartY=-352 StartZ=0 EndX=59 EndY=-352 EndZ=0
    g2: LineSegment StartX=59 StartY=-352 StartZ=0 EndX=59 EndY=-252 EndZ=0
    g3: LineSegment StartX=59 StartY=-252 StartZ=0 EndX=-59 EndY=-252 EndZ=0
  constraints (12):
    c: Vertical(g0)
    c: Coincident(g1,g0)
    c: Horizontal(g1)
    c: Coincident(g2,g1)
    c: Vertical(g2)
    c: Coincident(g3,g2)
    c: Coincident(g3,g0)
    c: Horizontal(g3)
    c: DistanceX(g0) = -59
    c: DistanceX(g1) = 59
    c: DistanceY(g0) = -352
    c: DistanceY(g0,g0) = 100
FEATURE [Part::Loft] Loft012
  Closed = false
  MaxDegree = 5
  Ruled = false
  Sections = -> [Sketch038,Sketch039]
  Solid = true
FEATURE [Part::Fillet] Fillet020
  Base = -> Loft012
  Edges = 12 edges r=3: [Edge1,Edge2,Edge3,Edge4,Edge5,Edge6,Edge7,Edge8,Edge9,Edge10,Edge11,Edge12]
FEATURE [Sketcher::SketchObject] Sketch040  label="inner013"
  FullyConstrained = true
  Placement = pos=(0,0,-259.26) rot=(0,0,1;0rad)
  sketch-geometry (4):
    g0: LineSegment StartX=-30 StartY=-277 StartZ=0 EndX=-30 EndY=-327 EndZ=0
    g1: LineSegment StartX=-30 StartY=-327 StartZ=0 EndX=30 EndY=-327 EndZ=0
    g2: LineSegment StartX=30 StartY=-327 StartZ=0 EndX=30 EndY=-277 EndZ=0
    g3: LineSegment StartX=30 StartY=-277 StartZ=0 EndX=-30 EndY=-277 EndZ=0
  constraints (12):
    c: Vertical(g0)
    c: Coincident(g1,g0)
    c: Horizontal(g1)
    c: Coincident(g2,g1)
    c: Vertical(g2)
    c: Coincident(g3,g2)
    c: Coincident(g3,g0)
    c: Horizontal(g3)
    c: DistanceX(g0) = -30
    c: DistanceX(g1) = 30
    c: DistanceY(g0) = -327
    c: DistanceY(g0,g0) = 50
FEATURE [Sketcher::SketchObject] Sketch041  label="outer013"
  FullyConstrained = true
  Placement = pos=(0,0,-281.2) rot=(0,0,1;0rad)
  sketch-geometry (4):
    g0: LineSegment StartX=-59 StartY=-252 StartZ=0 EndX=-59 EndY=-352 EndZ=0
    g1: LineSegment StartX=-59 StartY=-352 StartZ=0 EndX=59 EndY=-352 EndZ=0
    g2: LineSegment StartX=59 StartY=-352 StartZ=0 EndX=59 EndY=-252 EndZ=0
    g3: LineSegment StartX=59 StartY=-252 StartZ=0 EndX=-59 EndY=-252 EndZ=0
  constraints (12):
    c: Vertical(g0)
    c: Coincident(g1,g0)
    c: Horizontal(g1)
    c: Coincident(g2,g1)
    c: Vertical(g2)
    c: Coincident(g3,g2)
    c: Coincident(g3,g0)
    c: Horizontal(g3)
    c: DistanceX(g0) = -59
    c: DistanceX(g1) = 59
    c: DistanceY(g0) = -352
    c: DistanceY(g0,g0) = 100
FEATURE [Part::Loft] Loft013
  Closed = false
  MaxDegree = 5
  Ruled = false
  Sections = -> [Sketch040,Sketch041]
  Solid = true
FEATURE [Part::Fillet] Fillet021
  Base = -> Loft013
  Edges = 12 edges r=3: [Edge1,Edge2,Edge3,Edge4,Edge5,Edge6,Edge7,Edge8,Edge9,Edge10,Edge11,Edge12]
  Placement = pos=(0,0,-4) rot=(0,0,1;0rad)
FEATURE [Part::Cut] Cut013  label="sls008"
  Base = -> Fillet020
  Placement = pos=(0,0,10) rot=(0,0,1;0rad)
  Tool = -> Fillet021
FEATURE [Part::MultiFuse] Fusion039
  Shapes = -> [Cut013,Cut008,Cut007]
FEATURE [Sketcher::SketchObject] Sketch042  label="inner014"
  FullyConstrained = true
  Placement = pos=(0,0,-259.26) rot=(0,0,1;0rad)
  sketch-geometry (4):
    g0: LineSegment StartX=-30 StartY=-277 StartZ=0 EndX=-30 EndY=-327 EndZ=0
    g1: LineSegment StartX=-30 StartY=-327 StartZ=0 EndX=30 EndY=-327 EndZ=0
    g2: LineSegment StartX=30 StartY=-327 StartZ=0 EndX=30 EndY=-277 EndZ=0
    g3: LineSegment StartX=30 StartY=-277 StartZ=0 EndX=-30 EndY=-277 EndZ=0
  constraints (12):
    c: Vertical(g0)
    c: Coincident(g1,g0)
    c: Horizontal(g1)
    c: Coincident(g2,g1)
    c: Vertical(g2)
    c: Coincident(g3,g2)
    c: Coincident(g3,g0)
    c: Horizontal(g3)
    c: DistanceX(g0) = -30
    c: DistanceX(g1) = 30
    c: DistanceY(g0) = -327
    c: DistanceY(g0,g0) = 50
FEATURE [Sketcher::SketchObject] Sketch043  label="outer014"
  FullyConstrained = true
  Placement = pos=(0,0,-281.2) rot=(0,0,1;0rad)
  sketch-geometry (4):
    g0: LineSegment StartX=-59 StartY=-252 StartZ=0 EndX=-59 EndY=-352 EndZ=0
    g1: LineSegment StartX=-59 StartY=-352 StartZ=0 EndX=59 EndY=-352 EndZ=0
    g2: LineSegment StartX=59 StartY=-352 StartZ=0 EndX=59 EndY=-252 EndZ=0
    g3: LineSegment StartX=59 StartY=-252 StartZ=0 EndX=-59 EndY=-252 EndZ=0
  constraints (12):
    c: Vertical(g0)
    c: Coincident(g1,g0)
    c: Horizontal(g1)
    c: Coincident(g2,g1)
    c: Vertical(g2)
    c: Coincident(g3,g2)
    c: Coincident(g3,g0)
    c: Horizontal(g3)
    c: DistanceX(g0) = -59
    c: DistanceX(g1) = 59
    c: DistanceY(g0) = -352
    c: DistanceY(g0,g0) = 100
FEATURE [Part::Loft] Loft014
  Closed = false
  MaxDegree = 5
  Ruled = false
  Sections = -> [Sketch042,Sketch043]
  Solid = true
FEATURE [Part::Fillet] Fillet022
  Base = -> Loft014
  Edges = 12 edges r=3: [Edge1,Edge2,Edge3,Edge4,Edge5,Edge6,Edge7,Edge8,Edge9,Edge10,Edge11,Edge12]
FEATURE [Sketcher::SketchObject] Sketch044  label="inner015"
  FullyConstrained = true
  Placement = pos=(0,0,-259.26) rot=(0,0,1;0rad)
  sketch-geometry (4):
    g0: LineSegment StartX=-36 StartY=-277 StartZ=0 EndX=-36 EndY=-327 EndZ=0
    g1: LineSegment StartX=-36 StartY=-327 StartZ=0 EndX=36 EndY=-327 EndZ=0
    g2: LineSegment StartX=36 StartY=-327 StartZ=0 EndX=36 EndY=-277 EndZ=0
    g3: LineSegment StartX=36 StartY=-277 StartZ=0 EndX=-36 EndY=-277 EndZ=0
  constraints (12):
    c: Vertical(g0)
    c: Coincident(g1,g0)
    c: Horizontal(g1)
    c: Coincident(g2,g1)
    c: Vertical(g2)
    c: Coincident(g3,g2)
    c: Coincident(g3,g0)
    c: Horizontal(g3)
    c: DistanceX(g0) = -36
    c: DistanceX(g1) = 36
    c: DistanceY(g0) = -327
    c: DistanceY(g0,g0) = 50
FEATURE [Sketcher::SketchObject] Sketch045  label="outer015"
  FullyConstrained = true
  Placement = pos=(0,0,-281.2) rot=(0,0,1;0rad)
  sketch-geometry (4):
    g0: LineSegment StartX=-65 StartY=-252 StartZ=0 EndX=-65 EndY=-352 EndZ=0
    g1: LineSegment StartX=-65 StartY=-352 StartZ=0 EndX=65 EndY=-352 EndZ=0
    g2: LineSegment StartX=65 StartY=-352 StartZ=0 EndX=65 EndY=-252 EndZ=0
    g3: LineSegment StartX=65 StartY=-252 StartZ=0 EndX=-65 EndY=-252 EndZ=0
  constraints (12):
    c: Vertical(g0)
    c: Coincident(g1,g0)
    c: Horizontal(g1)
    c: Coincident(g2,g1)
    c: Vertical(g2)
    c: Coincident(g3,g2)
    c: Coincident(g3,g0)
    c: Horizontal(g3)
    c: DistanceX(g0) = -65
    c: DistanceX(g1) = 65
    c: DistanceY(g0) = -352
    c: DistanceY(g0,g0) = 100
FEATURE [Part::Loft] Loft015
  Closed = false
  MaxDegree = 5
  Ruled = false
  Sections = -> [Sketch044,Sketch045]
  Solid = true
FEATURE [Part::Fillet] Fillet023
  Base = -> Loft015
  Edges = 12 edges r=3: [Edge1,Edge2,Edge3,Edge4,Edge5,Edge6,Edge7,Edge8,Edge9,Edge10,Edge11,Edge12]
  Placement = pos=(0,0,-4) rot=(0,0,1;0rad)
FEATURE [Part::Cut] Cut014  label="sls009"
  Base = -> Fillet022
  Placement = pos=(0,0,4) rot=(0,0,1;0rad)
  Tool = -> Fillet023
FEATURE [Sketcher::SketchObject] Sketch046  label="inner016"
  FullyConstrained = true
  Placement = pos=(0,0,-259.26) rot=(0,0,1;0rad)
  sketch-geometry (4):
    g0: LineSegment StartX=-30 StartY=-277 StartZ=0 EndX=-30 EndY=-327 EndZ=0
    g1: LineSegment StartX=-30 StartY=-327 StartZ=0 EndX=30 EndY=-327 EndZ=0
    g2: LineSegment StartX=30 StartY=-327 StartZ=0 EndX=30 EndY=-277 EndZ=0
    g3: LineSegment StartX=30 StartY=-277 StartZ=0 EndX=-30 EndY=-277 EndZ=0
  constraints (12):
    c: Vertical(g0)
    c: Coincident(g1,g0)
    c: Horizontal(g1)
    c: Coincident(g2,g1)
    c: Vertical(g2)
    c: Coincident(g3,g2)
    c: Coincident(g3,g0)
    c: Horizontal(g3)
    c: DistanceX(g0) = -30
    c: DistanceX(g1) = 30
    c: DistanceY(g0) = -327
    c: DistanceY(g0,g0) = 50
FEATURE [Sketcher::SketchObject] Sketch047  label="outer016"
  FullyConstrained = true
  Placement = pos=(0,0,-281.2) rot=(0,0,1;0rad)
  sketch-geometry (4):
    g0: LineSegment StartX=-59 StartY=-252 StartZ=0 EndX=-59 EndY=-352 EndZ=0
    g1: LineSegment StartX=-59 StartY=-352 StartZ=0 EndX=59 EndY=-352 EndZ=0
    g2: LineSegment StartX=59 StartY=-352 StartZ=0 EndX=59 EndY=-252 EndZ=0
    g3: LineSegment StartX=59 StartY=-252 StartZ=0 EndX=-59 EndY=-252 EndZ=0
  constraints (12):
    c: Vertical(g0)
    c: Coincident(g1,g0)
    c: Horizontal(g1)
    c: Coincident(g2,g1)
    c: Vertical(g2)
    c: Coincident(g3,g2)
    c: Coincident(g3,g0)
    c: Horizontal(g3)
    c: DistanceX(g0) = -59
    c: DistanceX(g1) = 59
    c: DistanceY(g0) = -352
    c: DistanceY(g0,g0) = 100
FEATURE [Part::Loft] Loft016
  Closed = false
  MaxDegree = 5
  Ruled = false
  Sections = -> [Sketch046,Sketch047]
  Solid = true
FEATURE [Part::Fillet] Fillet024
  Base = -> Loft016
  Edges = 12 edges r=3: [Edge1,Edge2,Edge3,Edge4,Edge5,Edge6,Edge7,Edge8,Edge9,Edge10,Edge11,Edge12]
FEATURE [Sketcher::SketchObject] Sketch048  label="inner017"
  FullyConstrained = true
  Placement = pos=(0,0,-259.26) rot=(0,0,1;0rad)
  sketch-geometry (4):
    g0: LineSegment StartX=-30 StartY=-277 StartZ=0 EndX=-30 EndY=-327 EndZ=0
    g1: LineSegment StartX=-30 StartY=-327 StartZ=0 EndX=30 EndY=-327 EndZ=0
    g2: LineSegment StartX=30 StartY=-327 StartZ=0 EndX=30 EndY=-277 EndZ=0
    g3: LineSegment StartX=30 StartY=-277 StartZ=0 EndX=-30 EndY=-277 EndZ=0
  constraints (12):
    c: Vertical(g0)
    c: Coincident(g1,g0)
    c: Horizontal(g1)
    c: Coincident(g2,g1)
    c: Vertical(g2)
    c: Coincident(g3,g2)
    c: Coincident(g3,g0)
    c: Horizontal(g3)
    c: DistanceX(g0) = -30
    c: DistanceX(g1) = 30
    c: DistanceY(g0) = -327
    c: DistanceY(g0,g0) = 50
FEATURE [Sketcher::SketchObject] Sketch049  label="outer017"
  FullyConstrained = true
  Placement = pos=(0,0,-281.2) rot=(0,0,1;0rad)
  sketch-geometry (4):
    g0: LineSegment StartX=-65 StartY=-252 StartZ=0 EndX=-65 EndY=-352 EndZ=0
    g1: LineSegment StartX=-65 StartY=-352 StartZ=0 EndX=65 EndY=-352 EndZ=0
    g2: LineSegment StartX=65 StartY=-352 StartZ=0 EndX=65 EndY=-252 EndZ=0
    g3: LineSegment StartX=65 StartY=-252 StartZ=0 EndX=-65 EndY=-252 EndZ=0
  constraints (12):
    c: Vertical(g0)
    c: Coincident(g1,g0)
    c: Horizontal(g1)
    c: Coincident(g2,g1)
    c: Vertical(g2)
    c: Coincident(g3,g2)
    c: Coincident(g3,g0)
    c: Horizontal(g3)
    c: DistanceX(g0) = -65
    c: DistanceX(g1) = 65
    c: DistanceY(g0) = -352
    c: DistanceY(g0,g0) = 100
FEATURE [Part::Loft] Loft017
  Closed = false
  MaxDegree = 5
  Ruled = false
  Sections = -> [Sketch048,Sketch049]
  Solid = true
FEATURE [Part::Fillet] Fillet025
  Base = -> Loft017
  Edges = 12 edges r=3: [Edge1,Edge2,Edge3,Edge4,Edge5,Edge6,Edge7,Edge8,Edge9,Edge10,Edge11,Edge12]
  Placement = pos=(0,0,-4) rot=(0,0,1;0rad)
FEATURE [Part::Cut] Cut015  label="sls010"
  Base = -> Fillet024
  Placement = pos=(0,0,7) rot=(0,0,1;0rad)
  Tool = -> Fillet025
FEATURE [Sketcher::SketchObject] Sketch050  label="inner018"
  FullyConstrained = true
  Placement = pos=(0,0,-259.26) rot=(0,0,1;0rad)
  sketch-geometry (4):
    g0: LineSegment StartX=-30 StartY=-277 StartZ=0 EndX=-30 EndY=-327 EndZ=0
    g1: LineSegment StartX=-30 StartY=-327 StartZ=0 EndX=30 EndY=-327 EndZ=0
    g2: LineSegment StartX=30 StartY=-327 StartZ=0 EndX=30 EndY=-277 EndZ=0
    g3: LineSegment StartX=30 StartY=-277 StartZ=0 EndX=-30 EndY=-277 EndZ=0
  constraints (12):
    c: Vertical(g0)
    c: Coincident(g1,g0)
    c: Horizontal(g1)
    c: Coincident(g2,g1)
    c: Vertical(g2)
    c: Coincident(g3,g2)
    c: Coincident(g3,g0)
    c: Horizontal(g3)
    c: DistanceX(g0) = -30
    c: DistanceX(g1) = 30
    c: DistanceY(g0) = -327
    c: DistanceY(g0,g0) = 50
FEATURE [Sketcher::SketchObject] Sketch051  label="outer018"
  FullyConstrained = true
  Placement = pos=(0,0,-281.2) rot=(0,0,1;0rad)
  sketch-geometry (4):
    g0: LineSegment StartX=-59 StartY=-252 StartZ=0 EndX=-59 EndY=-352 EndZ=0
    g1: LineSegment StartX=-59 StartY=-352 StartZ=0 EndX=59 EndY=-352 EndZ=0
    g2: LineSegment StartX=59 StartY=-352 StartZ=0 EndX=59 EndY=-252 EndZ=0
    g3: LineSegment StartX=59 StartY=-252 StartZ=0 EndX=-59 EndY=-252 EndZ=0
  constraints (12):
    c: Vertical(g0)
    c: Coincident(g1,g0)
    c: Horizontal(g1)
    c: Coincident(g2,g1)
    c: Vertical(g2)
    c: Coincident(g3,g2)
    c: Coincident(g3,g0)
    c: Horizontal(g3)
    c: DistanceX(g0) = -59
    c: DistanceX(g1) = 59
    c: DistanceY(g0) = -352
    c: DistanceY(g0,g0) = 100
FEATURE [Part::Loft] Loft018
  Closed = false
  MaxDegree = 5
  Ruled = false
  Sections = -> [Sketch050,Sketch051]
  Solid = true
FEATURE [Part::Fillet] Fillet026
  Base = -> Loft018
  Edges = 12 edges r=3: [Edge1,Edge2,Edge3,Edge4,Edge5,Edge6,Edge7,Edge8,Edge9,Edge10,Edge11,Edge12]
FEATURE [Sketcher::SketchObject] Sketch052  label="inner019"
  FullyConstrained = true
  Placement = pos=(0,0,-259.26) rot=(0,0,1;0rad)
  sketch-geometry (4):
    g0: LineSegment StartX=-30 StartY=-277 StartZ=0 EndX=-30 EndY=-327 EndZ=0
    g1: LineSegment StartX=-30 StartY=-327 StartZ=0 EndX=30 EndY=-327 EndZ=0
    g2: LineSegment StartX=30 StartY=-327 StartZ=0 EndX=30 EndY=-277 EndZ=0
    g3: LineSegment StartX=30 StartY=-277 StartZ=0 EndX=-30 EndY=-277 EndZ=0
  constraints (12):
    c: Vertical(g0)
    c: Coincident(g1,g0)
    c: Horizontal(g1)
    c: Coincident(g2,g1)
    c: Vertical(g2)
    c: Coincident(g3,g2)
    c: Coincident(g3,g0)
    c: Horizontal(g3)
    c: DistanceX(g0) = -30
    c: DistanceX(g1) = 30
    c: DistanceY(g0) = -327
    c: DistanceY(g0,g0) = 50
FEATURE [Sketcher::SketchObject] Sketch053  label="outer019"
  FullyConstrained = true
  Placement = pos=(0,0,-281.2) rot=(0,0,1;0rad)
  sketch-geometry (4):
    g0: LineSegment StartX=-59 StartY=-252 StartZ=0 EndX=-59 EndY=-352 EndZ=0
    g1: LineSegment StartX=-59 StartY=-352 StartZ=0 EndX=59 EndY=-352 EndZ=0
    g2: LineSegment StartX=59 StartY=-352 StartZ=0 EndX=59 EndY=-252 EndZ=0
    g3: LineSegment StartX=59 StartY=-252 StartZ=0 EndX=-59 EndY=-252 EndZ=0
  constraints (12):
    c: Vertical(g0)
    c: Coincident(g1,g0)
    c: Horizontal(g1)
    c: Coincident(g2,g1)
    c: Vertical(g2)
    c: Coincident(g3,g2)
    c: Coincident(g3,g0)
    c: Horizontal(g3)
    c: DistanceX(g0) = -59
    c: DistanceX(g1) = 59
    c: DistanceY(g0) = -352
    c: DistanceY(g0,g0) = 100
FEATURE [Part::Loft] Loft019
  Closed = false
  MaxDegree = 5
  Ruled = false
  Sections = -> [Sketch052,Sketch053]
  Solid = true
FEATURE [Part::Fillet] Fillet027
  Base = -> Loft019
  Edges = 12 edges r=3: [Edge1,Edge2,Edge3,Edge4,Edge5,Edge6,Edge7,Edge8,Edge9,Edge10,Edge11,Edge12]
  Placement = pos=(0,0,-4) rot=(0,0,1;0rad)
FEATURE [Part::Cut] Cut016  label="sls011"
  Base = -> Fillet026
  Placement = pos=(0,0,10) rot=(0,0,1;0rad)
  Tool = -> Fillet027
FEATURE [Part::MultiFuse] Fusion040
  Placement = pos=(0,0,5) rot=(0,0,1;0rad)
  Shapes = -> [Cut016,Cut015,Cut014]
FEATURE [Part::MultiFuse] Fusion041  label="slsCUts"
  Shapes = -> [Fusion040,Fusion039]
FEATURE [Part::MultiFuse] Fusion042  label="slsCuts001"
  Shapes = -> [Fusion041,Extrude010]
FEATURE [Part::Cut] Cut017  label="sls012"
  Base = -> Cut012
  Tool = -> Fusion042
FEATURE [Part::Cut] Cut018  label="sls013"
  Base = -> Cut017
  Placement = pos=(0,17,15) rot=(0,0,1;0rad)
  Tool = -> Part__Feature153
FEATURE [Sketcher::SketchObject] Sketch054
  FullyConstrained = true
  MapMode = 2
  Placement = pos=(-0.5,-512,-305.5) rot=(0.57735,-0.57735,-0.57735;2.0944rad)
  sketch-geometry (8):
    g0: LineSegment StartX=-225.068 StartY=76.4427 StartZ=0 EndX=-228.265 EndY=72.5985 EndZ=0
    g1: LineSegment StartX=-228.265 StartY=72.5985 StartZ=0 EndX=-209.044 EndY=56.6125 EndZ=0
    g2: LineSegment StartX=-185 StartY=46.25 StartZ=0 EndX=-212.066 EndY=69.9864 EndZ=0
    g3: LineSegment StartX=-214.208 StartY=67.4108 StartZ=0 EndX=-212.066 EndY=69.9864 EndZ=0
    g4: LineSegment StartX=-214.208 StartY=67.4108 StartZ=0 EndX=-225.068 EndY=76.4427 EndZ=0
    g5: LineSegment StartX=-185 StartY=46.25 StartZ=0 EndX=-185 EndY=40.7882 EndZ=0
    g6: LineSegment StartX=-185 StartY=40.7882 StartZ=0 EndX=-203.044 EndY=56.6125 EndZ=0
    g7: LineSegment StartX=-203.044 StartY=56.6125 StartZ=0 EndX=-209.044 EndY=56.6125 EndZ=0
  constraints (24):
    c: Coincident(g0,g1)
    c: Coincident(g2,g3)
    c: Coincident(g4,g3)
    c: Coincident(g4,g0)
    c: Coincident(g5,g2)
    c: Coincident(g6,g5)
    c: Coincident(g7,g6)
    c: Horizontal(g7)
    c: Coincident(g1,g7)
    c: Parallel(g2,g6)
    c: Angle(g3,g2) = 1.54462
    c: Angle(g0,g4) = 1.5708
    c: Angle(g3,g4) = 1.5708
    c: DistanceX(g2) = -185
    c: DistanceY(g2) = 46.25
    c: Vertical(g5)
    c: Angle(g2,g5) = 2.29074
    c: Distance(g2) = 36
    c: Distance(g3) = 3.35
    c: Distance(g0) = 5
    c: Parallel(g4,g1)
    c: DistanceX(g7,g7) = 6
    c: Distance(g1) = 25
    c: Distance(g6) = 24
FEATURE [Part::Extrusion] Extrude014
  Base = -> Sketch054
  Dir = (-1,0,0)
  DirMode = 2
  FaceMakerClass = Part::FaceMakerBullseye
  LengthFwd = 61.6
  LengthRev = 0
  Placement = pos=(31.3,0,0) rot=(0,0,1;0rad)
  Solid = true
  Symmetric = false
FEATURE [Part::Cut] Cut020
  Base = -> Extrude014
  Tool = -> Cylinder
FEATURE [Part::MultiFuse] Fusion043  label="sls014"
  Shapes = -> [Cut020,Cut018]
FEATURE [Sketcher::SketchObject] Sketch095
  FullyConstrained = true
  sketch-geometry (4):
    g0: LineSegment StartX=-29.4 StartY=-303 StartZ=0 EndX=29.4 EndY=-303 EndZ=0
    g1: LineSegment StartX=29.4 StartY=-303 StartZ=0 EndX=39.5 EndY=-345 EndZ=0
    g2: LineSegment StartX=39.5 StartY=-345 StartZ=0 EndX=-39.5 EndY=-345 EndZ=0
    g3: LineSegment StartX=-39.5 StartY=-345 StartZ=0 EndX=-29.4 EndY=-303 EndZ=0
  constraints (12):
    c: Horizontal(g0)
    c: Coincident(g1,g0)
    c: Coincident(g2,g1)
    c: Horizontal(g2)
    c: Coincident(g3,g2)
    c: Coincident(g3,g0)
    c: DistanceX(g2) = -39.5
    c: DistanceY(g2) = -345
    c: DistanceX(g0) = -29.4
    c: DistanceX(g0) = 29.4
    c: DistanceX(g1) = 39.5
    c: DistanceY(g1,g0) = 42
FEATURE [Part::Extrusion] Extrude032  label="slsIn"
  Base = -> Sketch095
  Dir = (0,0,1)
  DirMode = 2
  FaceMakerClass = Part::FaceMakerBullseye
  LengthFwd = 4.5
  LengthRev = 0
  Placement = pos=(0,0,-249) rot=(0,0,1;0rad)
  Solid = true
  Symmetric = false
FEATURE [Sketcher::SketchObject] Sketch096
  FullyConstrained = true
  Placement = pos=(0,0,0) rot=(0.57735,0.57735,0.57735;2.0944rad)
  sketch-geometry (4):
    g0: LineSegment StartX=-358.25 StartY=-249 StartZ=0 EndX=-353.25 EndY=-249 EndZ=0
    g1: LineSegment StartX=-353.25 StartY=-249 StartZ=0 EndX=-326.489 EndY=-278.721 EndZ=0
    g2: LineSegment StartX=-326.489 StartY=-278.721 StartZ=0 EndX=-329.25 EndY=-281.208 EndZ=0
    g3: LineSegment StartX=-329.25 StartY=-281.208 StartZ=0 EndX=-358.25 EndY=-249 EndZ=0
  constraints (12):
    c: Coincident(g1,g0)
    c: Coincident(g0,g3)
    c: Horizontal(g0)
    c: DistanceX(g0,g0) = 5
    c: DistanceY(g0) = -249
    c: Coincident(g1,g2)
    c: Parallel(g3,g1)
    c: Coincident(g3,g2)
    c: Angle(g2,g3) = 1.5708
    c: Angle(g2) = -2.40855
    c: DistanceX(g3,g3) = 29
    c: DistanceX(g2) = -329.25
FEATURE [Part::Extrusion] Extrude033  label="slsIn001"
  Base = -> Sketch096
  Dir = (1,0,0)
  DirMode = 2
  FaceMakerClass = Part::FaceMakerBullseye
  LengthFwd = 20
  LengthRev = 0
  Placement = pos=(-10,0,0) rot=(0,0,1;0rad)
  Solid = true
  Symmetric = false
FEATURE [Part::MultiFuse] Fusion090
  Shapes = -> [Fusion043,Extrude032,Extrude033,Cut039]
FEATURE [Part::Sphere] Sphere004  label="SphereBase002"
  Angle1 = 0
  Angle2 = 12
  Angle3 = 360
  AttacherType = Attacher::AttachEngine3D
  Placement = pos=(5,0,74) rot=(0,0,1;0rad)
  Radius = 27.5
FEATURE [Part::Cut] Cut036
  Base = -> Sphere004
  Placement = pos=(131,0,-5) rot=(0,0,1;0rad)
  Tool = -> Cylinder129
FEATURE [Part::MultiFuse] Fusion082  label="Base002"
  Placement = pos=(-2,10,0) rot=(0,0,1;0rad)
  Shapes = -> [Cut036,Cylinder128]
FEATURE [Part::MultiFuse] Fusion083  label="lightModule008"
  Shapes = -> [Fusion082,Cylinder130,Fusion081]
FEATURE [Part::Cut] Cut037  label="lightModule007"
  Base = -> Fusion083
  Placement = pos=(-134,-360,-314) rot=(0,0,1;0rad)
  Tool = -> Fusion088
FEATURE [Part::MultiFuse] Fusion091  label="sls015"
  Shapes = -> [Fusion090,Cut037]
FEATURE [Part::Cut] Cut040  label="sls016"
  Base = -> Fusion091
  Tool = -> Cylinder147
FEATURE [Part::Cut] Cut041
  Base = -> Cut040
  Tool = -> Fusion092
FEATURE [Sketcher::SketchObject] Sketch100  label="SketchTop002"
  FullyConstrained = true
  sketch-geometry (6):
    g0: LineSegment StartX=50 StartY=-368.819 StartZ=0 EndX=80.9017 EndY=-273.713 EndZ=0
    g1: LineSegment StartX=80.9017 StartY=-273.713 StartZ=0 EndX=0 EndY=-214.935 EndZ=0
    g2: LineSegment StartX=0 StartY=-214.935 StartZ=0 EndX=-80.9017 EndY=-273.713 EndZ=0
    g3: LineSegment StartX=-80.9017 StartY=-273.713 StartZ=0 EndX=-50 EndY=-368.819 EndZ=0
    g4: LineSegment StartX=-50 StartY=-368.819 StartZ=0 EndX=50 EndY=-368.819 EndZ=0
    g5: Circle CenterX=0 CenterY=-300 CenterZ=0 NormalX=0 NormalY=0 NormalZ=1 AngleXU=0 Radius=85.0651
  constraints (15):
    c: Coincident(g0,g1)
    c: Coincident(g1,g2)
    c: Coincident(g2,g3)
    c: Coincident(g3,g4)
    c: Coincident(g4,g0)
    c: Equal(g0, g1-g4) x4
    c: PointOnObject(g0,g5)
    c: PointOnObject(g1,g5)
    c: PointOnObject(g2,g5)
    c: PointOnObject(g3,g5)
    c: PointOnObject(g4,g5)
    c: Horizontal(g4)
    c: DistanceX(g4,g4) = 100
    c: DistanceY(g5) = -300
    c: DistanceX(g5) = 0
FEATURE [Sketcher::SketchObject] Sketch101  label="SketchBottom002"
  FullyConstrained = true
  Placement = pos=(0,0,20) rot=(0,0,1;0rad)
  sketch-geometry (6):
    g0: LineSegment StartX=37.5 StartY=-351.614 StartZ=0 EndX=60.6763 EndY=-280.285 EndZ=0
    g1: LineSegment StartX=60.6763 StartY=-280.285 StartZ=0 EndX=0 EndY=-236.201 EndZ=0
    g2: LineSegment StartX=0 StartY=-236.201 StartZ=0 EndX=-60.6763 EndY=-280.285 EndZ=0
    g3: LineSegment StartX=-60.6763 StartY=-280.285 StartZ=0 EndX=-37.5 EndY=-351.614 EndZ=0
    g4: LineSegment StartX=-37.5 StartY=-351.614 StartZ=0 EndX=37.5 EndY=-351.614 EndZ=0
    g5: Circle CenterX=0 CenterY=-300 CenterZ=0 NormalX=0 NormalY=0 NormalZ=1 AngleXU=0 Radius=63.7988
  constraints (15):
    c: Coincident(g0,g1)
    c: Coincident(g1,g2)
    c: Coincident(g2,g3)
    c: Coincident(g3,g4)
    c: Coincident(g4,g0)
    c: Equal(g0, g1-g4) x4
    c: PointOnObject(g0,g5)
    c: PointOnObject(g1,g5)
    c: PointOnObject(g2,g5)
    c: PointOnObject(g3,g5)
    c: PointOnObject(g4,g5)
    c: Horizontal(g4)
    c: DistanceX(g4,g4) = 75
    c: DistanceX(g5) = 0
    c: DistanceY(g5) = -300
FEATURE [Part::Loft] Loft022
  Closed = false
  MaxDegree = 5
  Ruled = false
  Sections = -> [Sketch100,Sketch101]
  Solid = true
FEATURE [Sketcher::SketchObject] Sketch102  label="SketchTop003"
  FullyConstrained = true
  sketch-geometry (6):
    g0: LineSegment StartX=47.5 StartY=-365.378 StartZ=0 EndX=76.8566 EndY=-275.028 EndZ=0
    g1: LineSegment StartX=76.8566 StartY=-275.028 StartZ=0 EndX=1.9185e-12 EndY=-219.188 EndZ=0
    g2: LineSegment StartX=1.9185e-12 StartY=-219.188 StartZ=0 EndX=-76.8566 EndY=-275.028 EndZ=0
    g3: LineSegment StartX=-76.8566 StartY=-275.028 StartZ=0 EndX=-47.5 EndY=-365.378 EndZ=0
    g4: LineSegment StartX=-47.5 StartY=-365.378 StartZ=0 EndX=47.5 EndY=-365.378 EndZ=0
    g5: Circle CenterX=0 CenterY=-300 CenterZ=0 NormalX=0 NormalY=0 NormalZ=1 AngleXU=0 Radius=80.8118
  constraints (15):
    c: Coincident(g0,g1)
    c: Coincident(g1,g2)
    c: Coincident(g2,g3)
    c: Coincident(g3,g4)
    c: Coincident(g4,g0)
    c: Equal(g0, g1-g4) x4
    c: PointOnObject(g0,g5)
    c: PointOnObject(g1,g5)
    c: PointOnObject(g2,g5)
    c: PointOnObject(g3,g5)
    c: PointOnObject(g4,g5)
    c: Horizontal(g4)
    c: DistanceX(g4,g4) = 95
    c: DistanceY(g5) = -300
    c: DistanceX(g5) = 0
FEATURE [Sketcher::SketchObject] Sketch103  label="SketchBottom003"
  FullyConstrained = true
  Placement = pos=(0,0,20) rot=(0,0,1;0rad)
  sketch-geometry (6):
    g0: LineSegment StartX=35 StartY=-348.173 StartZ=0 EndX=56.6312 EndY=-281.599 EndZ=0
    g1: LineSegment StartX=56.6312 StartY=-281.599 StartZ=0 EndX=0 EndY=-240.454 EndZ=0
    g2: LineSegment StartX=0 StartY=-240.454 StartZ=0 EndX=-56.6312 EndY=-281.599 EndZ=0
    g3: LineSegment StartX=-56.6312 StartY=-281.599 StartZ=0 EndX=-35 EndY=-348.173 EndZ=0
    g4: LineSegment StartX=-35 StartY=-348.173 StartZ=0 EndX=35 EndY=-348.173 EndZ=0
    g5: Circle CenterX=0 CenterY=-300 CenterZ=0 NormalX=0 NormalY=0 NormalZ=1 AngleXU=0 Radius=59.5456
  constraints (15):
    c: Coincident(g0,g1)
    c: Coincident(g1,g2)
    c: Coincident(g2,g3)
    c: Coincident(g3,g4)
    c: Coincident(g4,g0)
    c: Equal(g0, g1-g4) x4
    c: PointOnObject(g0,g5)
    c: PointOnObject(g1,g5)
    c: PointOnObject(g2,g5)
    c: PointOnObject(g3,g5)
    c: PointOnObject(g4,g5)
    c: Horizontal(g4)
    c: DistanceX(g4,g4) = 70
    c: DistanceX(g5) = 0
    c: DistanceY(g5) = -300
FEATURE [Part::Loft] Loft023
  Closed = false
  MaxDegree = 5
  Ruled = false
  Sections = -> [Sketch102,Sketch103]
  Solid = true
FEATURE [Part::Cut] Cut044  label="srsCone001"
  Base = -> Loft022
  Placement = pos=(0,0,-36) rot=(0,0,1;0rad)
  Tool = -> Loft023
FEATURE [Part::Fillet] Fillet031
  Base = -> Cut044
  Edges = 5 edges r=1.5: [Edge3,Edge15,Edge16,Edge17,Edge18]
FEATURE [Part::Fillet] Fillet032
  Base = -> Fillet031
  Edges = 5 edges r=1.5: [Edge4,Edge7,Edge11,Edge12,Edge13]
FEATURE [Part::Fillet] Fillet033
  Base = -> Fillet032
  Edges = 5 edges r=2: [Edge1,Edge3,Edge5,Edge15,Edge17]
FEATURE [Part::Fillet] Fillet034  label="srsCone"
  Base = -> Fillet033
  Edges = 5 edges r=1.5: [Edge63,Edge64,Edge65,Edge66,Edge67]
FEATURE [Sketcher::SketchObject] Sketch104  label="SketchTop004"
  FullyConstrained = true
  sketch-geometry (6):
    g0: LineSegment StartX=50 StartY=-368.819 StartZ=0 EndX=80.9017 EndY=-273.713 EndZ=0
    g1: LineSegment StartX=80.9017 StartY=-273.713 StartZ=0 EndX=0 EndY=-214.935 EndZ=0
    g2: LineSegment StartX=0 StartY=-214.935 StartZ=0 EndX=-80.9017 EndY=-273.713 EndZ=0
    g3: LineSegment StartX=-80.9017 StartY=-273.713 StartZ=0 EndX=-50 EndY=-368.819 EndZ=0
    g4: LineSegment StartX=-50 StartY=-368.819 StartZ=0 EndX=50 EndY=-368.819 EndZ=0
    g5: Circle CenterX=0 CenterY=-300 CenterZ=0 NormalX=0 NormalY=0 NormalZ=1 AngleXU=0 Radius=85.0651
  constraints (15):
    c: Coincident(g0,g1)
    c: Coincident(g1,g2)
    c: Coincident(g2,g3)
    c: Coincident(g3,g4)
    c: Coincident(g4,g0)
    c: Equal(g0, g1-g4) x4
    c: PointOnObject(g0,g5)
    c: PointOnObject(g1,g5)
    c: PointOnObject(g2,g5)
    c: PointOnObject(g3,g5)
    c: PointOnObject(g4,g5)
    c: Horizontal(g4)
    c: DistanceX(g4,g4) = 100
    c: DistanceY(g5) = -300
    c: DistanceX(g5) = 0
FEATURE [Sketcher::SketchObject] Sketch105  label="SketchBottom004"
  FullyConstrained = true
  Placement = pos=(0,0,20) rot=(0,0,1;0rad)
  sketch-geometry (6):
    g0: LineSegment StartX=37.5 StartY=-351.614 StartZ=0 EndX=60.6763 EndY=-280.285 EndZ=0
    g1: LineSegment StartX=60.6763 StartY=-280.285 StartZ=0 EndX=0 EndY=-236.201 EndZ=0
    g2: LineSegment StartX=0 StartY=-236.201 StartZ=0 EndX=-60.6763 EndY=-280.285 EndZ=0
    g3: LineSegment StartX=-60.6763 StartY=-280.285 StartZ=0 EndX=-37.5 EndY=-351.614 EndZ=0
    g4: LineSegment StartX=-37.5 StartY=-351.614 StartZ=0 EndX=37.5 EndY=-351.614 EndZ=0
    g5: Circle CenterX=0 CenterY=-300 CenterZ=0 NormalX=0 NormalY=0 NormalZ=1 AngleXU=0 Radius=63.7988
  constraints (15):
    c: Coincident(g0,g1)
    c: Coincident(g1,g2)
    c: Coincident(g2,g3)
    c: Coincident(g3,g4)
    c: Coincident(g4,g0)
    c: Equal(g0, g1-g4) x4
    c: PointOnObject(g0,g5)
    c: PointOnObject(g1,g5)
    c: PointOnObject(g2,g5)
    c: PointOnObject(g3,g5)
    c: PointOnObject(g4,g5)
    c: Horizontal(g4)
    c: DistanceX(g4,g4) = 75
    c: DistanceX(g5) = 0
    c: DistanceY(g5) = -300
FEATURE [Part::Loft] Loft024
  Closed = false
  MaxDegree = 5
  Ruled = false
  Sections = -> [Sketch104,Sketch105]
  Solid = true
FEATURE [Sketcher::SketchObject] Sketch106  label="SketchTop005"
  FullyConstrained = true
  sketch-geometry (6):
    g0: LineSegment StartX=47.5 StartY=-365.378 StartZ=0 EndX=76.8566 EndY=-275.028 EndZ=0
    g1: LineSegment StartX=76.8566 StartY=-275.028 StartZ=0 EndX=1.9185e-12 EndY=-219.188 EndZ=0
    g2: LineSegment StartX=1.9185e-12 StartY=-219.188 StartZ=0 EndX=-76.8566 EndY=-275.028 EndZ=0
    g3: LineSegment StartX=-76.8566 StartY=-275.028 StartZ=0 EndX=-47.5 EndY=-365.378 EndZ=0
    g4: LineSegment StartX=-47.5 StartY=-365.378 StartZ=0 EndX=47.5 EndY=-365.378 EndZ=0
    g5: Circle CenterX=0 CenterY=-300 CenterZ=0 NormalX=0 NormalY=0 NormalZ=1 AngleXU=0 Radius=80.8118
  constraints (15):
    c: Coincident(g0,g1)
    c: Coincident(g1,g2)
    c: Coincident(g2,g3)
    c: Coincident(g3,g4)
    c: Coincident(g4,g0)
    c: Equal(g0, g1-g4) x4
    c: PointOnObject(g0,g5)
    c: PointOnObject(g1,g5)
    c: PointOnObject(g2,g5)
    c: PointOnObject(g3,g5)
    c: PointOnObject(g4,g5)
    c: Horizontal(g4)
    c: DistanceX(g4,g4) = 95
    c: DistanceY(g5) = -300
    c: DistanceX(g5) = 0
FEATURE [Sketcher::SketchObject] Sketch107  label="SketchBottom005"
  FullyConstrained = true
  Placement = pos=(0,0,20) rot=(0,0,1;0rad)
  sketch-geometry (6):
    g0: LineSegment StartX=35 StartY=-348.173 StartZ=0 EndX=56.6312 EndY=-281.599 EndZ=0
    g1: LineSegment StartX=56.6312 StartY=-281.599 StartZ=0 EndX=0 EndY=-240.454 EndZ=0
    g2: LineSegment StartX=0 StartY=-240.454 StartZ=0 EndX=-56.6312 EndY=-281.599 EndZ=0
    g3: LineSegment StartX=-56.6312 StartY=-281.599 StartZ=0 EndX=-35 EndY=-348.173 EndZ=0
    g4: LineSegment StartX=-35 StartY=-348.173 StartZ=0 EndX=35 EndY=-348.173 EndZ=0
    g5: Circle CenterX=0 CenterY=-300 CenterZ=0 NormalX=0 NormalY=0 NormalZ=1 AngleXU=0 Radius=59.5456
  constraints (15):
    c: Coincident(g0,g1)
    c: Coincident(g1,g2)
    c: Coincident(g2,g3)
    c: Coincident(g3,g4)
    c: Coincident(g4,g0)
    c: Equal(g0, g1-g4) x4
    c: PointOnObject(g0,g5)
    c: PointOnObject(g1,g5)
    c: PointOnObject(g2,g5)
    c: PointOnObject(g3,g5)
    c: PointOnObject(g4,g5)
    c: Horizontal(g4)
    c: DistanceX(g4,g4) = 70
    c: DistanceX(g5) = 0
    c: DistanceY(g5) = -300
FEATURE [Part::Loft] Loft025
  Closed = false
  MaxDegree = 5
  Ruled = false
  Sections = -> [Sketch106,Sketch107]
  Solid = true
FEATURE [Part::Cut] Cut045  label="srsCone002"
  Base = -> Loft024
  Placement = pos=(0,0,-36) rot=(0,0,1;0rad)
  Tool = -> Loft025
FEATURE [Part::Fillet] Fillet035
  Base = -> Cut045
  Edges = 5 edges r=1.5: [Edge3,Edge15,Edge16,Edge17,Edge18]
FEATURE [Part::Fillet] Fillet036
  Base = -> Fillet035
  Edges = 5 edges r=1.5: [Edge4,Edge7,Edge11,Edge12,Edge13]
FEATURE [Part::Fillet] Fillet037
  Base = -> Fillet036
  Edges = 5 edges r=2: [Edge1,Edge3,Edge5,Edge15,Edge17]
FEATURE [Part::Fillet] Fillet038  label="srsCone003"
  Base = -> Fillet037
  Edges = 5 edges r=1.5: [Edge63,Edge64,Edge65,Edge66,Edge67]
  Placement = pos=(0,0,-18) rot=(0,0,1;0rad)
FEATURE [Sketcher::SketchObject] Sketch108  label="SketchTop006"
  FullyConstrained = true
  sketch-geometry (6):
    g0: LineSegment StartX=50 StartY=-368.819 StartZ=0 EndX=80.9017 EndY=-273.713 EndZ=0
    g1: LineSegment StartX=80.9017 StartY=-273.713 StartZ=0 EndX=0 EndY=-214.935 EndZ=0
    g2: LineSegment StartX=0 StartY=-214.935 StartZ=0 EndX=-80.9017 EndY=-273.713 EndZ=0
    g3: LineSegment StartX=-80.9017 StartY=-273.713 StartZ=0 EndX=-50 EndY=-368.819 EndZ=0
    g4: LineSegment StartX=-50 StartY=-368.819 StartZ=0 EndX=50 EndY=-368.819 EndZ=0
    g5: Circle CenterX=0 CenterY=-300 CenterZ=0 NormalX=0 NormalY=0 NormalZ=1 AngleXU=0 Radius=85.0651
  constraints (15):
    c: Coincident(g0,g1)
    c: Coincident(g1,g2)
    c: Coincident(g2,g3)
    c: Coincident(g3,g4)
    c: Coincident(g4,g0)
    c: Equal(g0, g1-g4) x4
    c: PointOnObject(g0,g5)
    c: PointOnObject(g1,g5)
    c: PointOnObject(g2,g5)
    c: PointOnObject(g3,g5)
    c: PointOnObject(g4,g5)
    c: Horizontal(g4)
    c: DistanceX(g4,g4) = 100
    c: DistanceY(g5) = -300
    c: DistanceX(g5) = 0
FEATURE [Sketcher::SketchObject] Sketch109  label="SketchBottom006"
  FullyConstrained = true
  Placement = pos=(0,0,20) rot=(0,0,1;0rad)
  sketch-geometry (6):
    g0: LineSegment StartX=37.5 StartY=-351.614 StartZ=0 EndX=60.6763 EndY=-280.285 EndZ=0
    g1: LineSegment StartX=60.6763 StartY=-280.285 StartZ=0 EndX=0 EndY=-236.201 EndZ=0
    g2: LineSegment StartX=0 StartY=-236.201 StartZ=0 EndX=-60.6763 EndY=-280.285 EndZ=0
    g3: LineSegment StartX=-60.6763 StartY=-280.285 StartZ=0 EndX=-37.5 EndY=-351.614 EndZ=0
    g4: LineSegment StartX=-37.5 StartY=-351.614 StartZ=0 EndX=37.5 EndY=-351.614 EndZ=0
    g5: Circle CenterX=0 CenterY=-300 CenterZ=0 NormalX=0 NormalY=0 NormalZ=1 AngleXU=0 Radius=63.7988
  constraints (15):
    c: Coincident(g0,g1)
    c: Coincident(g1,g2)
    c: Coincident(g2,g3)
    c: Coincident(g3,g4)
    c: Coincident(g4,g0)
    c: Equal(g0, g1-g4) x4
    c: PointOnObject(g0,g5)
    c: PointOnObject(g1,g5)
    c: PointOnObject(g2,g5)
    c: PointOnObject(g3,g5)
    c: PointOnObject(g4,g5)
    c: Horizontal(g4)
    c: DistanceX(g4,g4) = 75
    c: DistanceX(g5) = 0
    c: DistanceY(g5) = -300
FEATURE [Part::Loft] Loft026
  Closed = false
  MaxDegree = 5
  Ruled = false
  Sections = -> [Sketch108,Sketch109]
  Solid = true
FEATURE [Sketcher::SketchObject] Sketch110  label="SketchTop007"
  FullyConstrained = true
  sketch-geometry (6):
    g0: LineSegment StartX=47.5 StartY=-365.378 StartZ=0 EndX=76.8566 EndY=-275.028 EndZ=0
    g1: LineSegment StartX=76.8566 StartY=-275.028 StartZ=0 EndX=1.9185e-12 EndY=-219.188 EndZ=0
    g2: LineSegment StartX=1.9185e-12 StartY=-219.188 StartZ=0 EndX=-76.8566 EndY=-275.028 EndZ=0
    g3: LineSegment StartX=-76.8566 StartY=-275.028 StartZ=0 EndX=-47.5 EndY=-365.378 EndZ=0
    g4: LineSegment StartX=-47.5 StartY=-365.378 StartZ=0 EndX=47.5 EndY=-365.378 EndZ=0
    g5: Circle CenterX=0 CenterY=-300 CenterZ=0 NormalX=0 NormalY=0 NormalZ=1 AngleXU=0 Radius=80.8118
  constraints (15):
    c: Coincident(g0,g1)
    c: Coincident(g1,g2)
    c: Coincident(g2,g3)
    c: Coincident(g3,g4)
    c: Coincident(g4,g0)
    c: Equal(g0, g1-g4) x4
    c: PointOnObject(g0,g5)
    c: PointOnObject(g1,g5)
    c: PointOnObject(g2,g5)
    c: PointOnObject(g3,g5)
    c: PointOnObject(g4,g5)
    c: Horizontal(g4)
    c: DistanceX(g4,g4) = 95
    c: DistanceY(g5) = -300
    c: DistanceX(g5) = 0
FEATURE [Sketcher::SketchObject] Sketch111  label="SketchBottom007"
  FullyConstrained = true
  Placement = pos=(0,0,20) rot=(0,0,1;0rad)
  sketch-geometry (6):
    g0: LineSegment StartX=35 StartY=-348.173 StartZ=0 EndX=56.6312 EndY=-281.599 EndZ=0
    g1: LineSegment StartX=56.6312 StartY=-281.599 StartZ=0 EndX=0 EndY=-240.454 EndZ=0
    g2: LineSegment StartX=0 StartY=-240.454 StartZ=0 EndX=-56.6312 EndY=-281.599 EndZ=0
    g3: LineSegment StartX=-56.6312 StartY=-281.599 StartZ=0 EndX=-35 EndY=-348.173 EndZ=0
    g4: LineSegment StartX=-35 StartY=-348.173 StartZ=0 EndX=35 EndY=-348.173 EndZ=0
    g5: Circle CenterX=0 CenterY=-300 CenterZ=0 NormalX=0 NormalY=0 NormalZ=1 AngleXU=0 Radius=59.5456
  constraints (15):
    c: Coincident(g0,g1)
    c: Coincident(g1,g2)
    c: Coincident(g2,g3)
    c: Coincident(g3,g4)
    c: Coincident(g4,g0)
    c: Equal(g0, g1-g4) x4
    c: PointOnObject(g0,g5)
    c: PointOnObject(g1,g5)
    c: PointOnObject(g2,g5)
    c: PointOnObject(g3,g5)
    c: PointOnObject(g4,g5)
    c: Horizontal(g4)
    c: DistanceX(g4,g4) = 70
    c: DistanceX(g5) = 0
    c: DistanceY(g5) = -300
FEATURE [Part::Loft] Loft027
  Closed = false
  MaxDegree = 5
  Ruled = false
  Sections = -> [Sketch110,Sketch111]
  Solid = true
FEATURE [Part::Cut] Cut046  label="srsCone004"
  Base = -> Loft026
  Placement = pos=(0,0,-36) rot=(0,0,1;0rad)
  Tool = -> Loft027
FEATURE [Part::Fillet] Fillet039
  Base = -> Cut046
  Edges = 5 edges r=1.5: [Edge3,Edge15,Edge16,Edge17,Edge18]
FEATURE [Part::Fillet] Fillet040
  Base = -> Fillet039
  Edges = 5 edges r=1.5: [Edge4,Edge7,Edge11,Edge12,Edge13]
FEATURE [Part::Fillet] Fillet041
  Base = -> Fillet040
  Edges = 5 edges r=2: [Edge1,Edge3,Edge5,Edge15,Edge17]
FEATURE [Part::Fillet] Fillet042  label="srsCone005"
  Base = -> Fillet041
  Edges = 5 edges r=1.5: [Edge63,Edge64,Edge65,Edge66,Edge67]
  Placement = pos=(0,0,-36) rot=(0,0,1;0rad)
FEATURE [Sketcher::SketchObject] Sketch112  label="SketchTop008"
  FullyConstrained = true
  sketch-geometry (6):
    g0: LineSegment StartX=50 StartY=-368.819 StartZ=0 EndX=80.9017 EndY=-273.713 EndZ=0
    g1: LineSegment StartX=80.9017 StartY=-273.713 StartZ=0 EndX=0 EndY=-214.935 EndZ=0
    g2: LineSegment StartX=0 StartY=-214.935 StartZ=0 EndX=-80.9017 EndY=-273.713 EndZ=0
    g3: LineSegment StartX=-80.9017 StartY=-273.713 StartZ=0 EndX=-50 EndY=-368.819 EndZ=0
    g4: LineSegment StartX=-50 StartY=-368.819 StartZ=0 EndX=50 EndY=-368.819 EndZ=0
    g5: Circle CenterX=0 CenterY=-300 CenterZ=0 NormalX=0 NormalY=0 NormalZ=1 AngleXU=0 Radius=85.0651
  constraints (15):
    c: Coincident(g0,g1)
    c: Coincident(g1,g2)
    c: Coincident(g2,g3)
    c: Coincident(g3,g4)
    c: Coincident(g4,g0)
    c: Equal(g0, g1-g4) x4
    c: PointOnObject(g0,g5)
    c: PointOnObject(g1,g5)
    c: PointOnObject(g2,g5)
    c: PointOnObject(g3,g5)
    c: PointOnObject(g4,g5)
    c: Horizontal(g4)
    c: DistanceX(g4,g4) = 100
    c: DistanceY(g5) = -300
    c: DistanceX(g5) = 0
FEATURE [Sketcher::SketchObject] Sketch113  label="SketchBottom008"
  FullyConstrained = true
  Placement = pos=(0,0,20) rot=(0,0,1;0rad)
  sketch-geometry (6):
    g0: LineSegment StartX=37.5 StartY=-351.614 StartZ=0 EndX=60.6763 EndY=-280.285 EndZ=0
    g1: LineSegment StartX=60.6763 StartY=-280.285 StartZ=0 EndX=0 EndY=-236.201 EndZ=0
    g2: LineSegment StartX=0 StartY=-236.201 StartZ=0 EndX=-60.6763 EndY=-280.285 EndZ=0
    g3: LineSegment StartX=-60.6763 StartY=-280.285 StartZ=0 EndX=-37.5 EndY=-351.614 EndZ=0
    g4: LineSegment StartX=-37.5 StartY=-351.614 StartZ=0 EndX=37.5 EndY=-351.614 EndZ=0
    g5: Circle CenterX=0 CenterY=-300 CenterZ=0 NormalX=0 NormalY=0 NormalZ=1 AngleXU=0 Radius=63.7988
  constraints (15):
    c: Coincident(g0,g1)
    c: Coincident(g1,g2)
    c: Coincident(g2,g3)
    c: Coincident(g3,g4)
    c: Coincident(g4,g0)
    c: Equal(g0, g1-g4) x4
    c: PointOnObject(g0,g5)
    c: PointOnObject(g1,g5)
    c: PointOnObject(g2,g5)
    c: PointOnObject(g3,g5)
    c: PointOnObject(g4,g5)
    c: Horizontal(g4)
    c: DistanceX(g4,g4) = 75
    c: DistanceX(g5) = 0
    c: DistanceY(g5) = -300
FEATURE [Part::Loft] Loft028
  Closed = false
  MaxDegree = 5
  Ruled = false
  Sections = -> [Sketch112,Sketch113]
  Solid = true
FEATURE [Sketcher::SketchObject] Sketch114  label="SketchTop009"
  FullyConstrained = true
  sketch-geometry (6):
    g0: LineSegment StartX=47.5 StartY=-365.378 StartZ=0 EndX=76.8566 EndY=-275.028 EndZ=0
    g1: LineSegment StartX=76.8566 StartY=-275.028 StartZ=0 EndX=1.9185e-12 EndY=-219.188 EndZ=0
    g2: LineSegment StartX=1.9185e-12 StartY=-219.188 StartZ=0 EndX=-76.8566 EndY=-275.028 EndZ=0
    g3: LineSegment StartX=-76.8566 StartY=-275.028 StartZ=0 EndX=-47.5 EndY=-365.378 EndZ=0
    g4: LineSegment StartX=-47.5 StartY=-365.378 StartZ=0 EndX=47.5 EndY=-365.378 EndZ=0
    g5: Circle CenterX=0 CenterY=-300 CenterZ=0 NormalX=0 NormalY=0 NormalZ=1 AngleXU=0 Radius=80.8118
  constraints (15):
    c: Coincident(g0,g1)
    c: Coincident(g1,g2)
    c: Coincident(g2,g3)
    c: Coincident(g3,g4)
    c: Coincident(g4,g0)
    c: Equal(g0, g1-g4) x4
    c: PointOnObject(g0,g5)
    c: PointOnObject(g1,g5)
    c: PointOnObject(g2,g5)
    c: PointOnObject(g3,g5)
    c: PointOnObject(g4,g5)
    c: Horizontal(g4)
    c: DistanceX(g4,g4) = 95
    c: DistanceY(g5) = -300
    c: DistanceX(g5) = 0
FEATURE [Sketcher::SketchObject] Sketch115  label="SketchBottom009"
  FullyConstrained = true
  Placement = pos=(0,0,20) rot=(0,0,1;0rad)
  sketch-geometry (6):
    g0: LineSegment StartX=35 StartY=-348.173 StartZ=0 EndX=56.6312 EndY=-281.599 EndZ=0
    g1: LineSegment StartX=56.6312 StartY=-281.599 StartZ=0 EndX=0 EndY=-240.454 EndZ=0
    g2: LineSegment StartX=0 StartY=-240.454 StartZ=0 EndX=-56.6312 EndY=-281.599 EndZ=0
    g3: LineSegment StartX=-56.6312 StartY=-281.599 StartZ=0 EndX=-35 EndY=-348.173 EndZ=0
    g4: LineSegment StartX=-35 StartY=-348.173 StartZ=0 EndX=35 EndY=-348.173 EndZ=0
    g5: Circle CenterX=0 CenterY=-300 CenterZ=0 NormalX=0 NormalY=0 NormalZ=1 AngleXU=0 Radius=59.5456
  constraints (15):
    c: Coincident(g0,g1)
    c: Coincident(g1,g2)
    c: Coincident(g2,g3)
    c: Coincident(g3,g4)
    c: Coincident(g4,g0)
    c: Equal(g0, g1-g4) x4
    c: PointOnObject(g0,g5)
    c: PointOnObject(g1,g5)
    c: PointOnObject(g2,g5)
    c: PointOnObject(g3,g5)
    c: PointOnObject(g4,g5)
    c: Horizontal(g4)
    c: DistanceX(g4,g4) = 70
    c: DistanceX(g5) = 0
    c: DistanceY(g5) = -300
FEATURE [Part::Loft] Loft029
  Closed = false
  MaxDegree = 5
  Ruled = false
  Sections = -> [Sketch114,Sketch115]
  Solid = true
FEATURE [Part::Cut] Cut047  label="srsCone006"
  Base = -> Loft028
  Placement = pos=(0,0,-36) rot=(0,0,1;0rad)
  Tool = -> Loft029
FEATURE [Part::Fillet] Fillet043
  Base = -> Cut047
  Edges = 5 edges r=1.5: [Edge3,Edge15,Edge16,Edge17,Edge18]
FEATURE [Part::Fillet] Fillet044
  Base = -> Fillet043
  Edges = 5 edges r=1.5: [Edge4,Edge7,Edge11,Edge12,Edge13]
FEATURE [Part::Fillet] Fillet045
  Base = -> Fillet044
  Edges = 5 edges r=2: [Edge1,Edge3,Edge5,Edge15,Edge17]
FEATURE [Part::Fillet] Fillet046  label="srsCone007"
  Base = -> Fillet045
  Edges = 5 edges r=1.5: [Edge63,Edge64,Edge65,Edge66,Edge67]
  Placement = pos=(0,0,-54) rot=(0,0,1;0rad)
FEATURE [Sketcher::SketchObject] Sketch116  label="SketchTop010"
  FullyConstrained = true
  sketch-geometry (6):
    g0: LineSegment StartX=50 StartY=-368.819 StartZ=0 EndX=80.9017 EndY=-273.713 EndZ=0
    g1: LineSegment StartX=80.9017 StartY=-273.713 StartZ=0 EndX=0 EndY=-214.935 EndZ=0
    g2: LineSegment StartX=0 StartY=-214.935 StartZ=0 EndX=-80.9017 EndY=-273.713 EndZ=0
    g3: LineSegment StartX=-80.9017 StartY=-273.713 StartZ=0 EndX=-50 EndY=-368.819 EndZ=0
    g4: LineSegment StartX=-50 StartY=-368.819 StartZ=0 EndX=50 EndY=-368.819 EndZ=0
    g5: Circle CenterX=0 CenterY=-300 CenterZ=0 NormalX=0 NormalY=0 NormalZ=1 AngleXU=0 Radius=85.0651
  constraints (15):
    c: Coincident(g0,g1)
    c: Coincident(g1,g2)
    c: Coincident(g2,g3)
    c: Coincident(g3,g4)
    c: Coincident(g4,g0)
    c: Equal(g0, g1-g4) x4
    c: PointOnObject(g0,g5)
    c: PointOnObject(g1,g5)
    c: PointOnObject(g2,g5)
    c: PointOnObject(g3,g5)
    c: PointOnObject(g4,g5)
    c: Horizontal(g4)
    c: DistanceX(g4,g4) = 100
    c: DistanceY(g5) = -300
    c: DistanceX(g5) = 0
FEATURE [Sketcher::SketchObject] Sketch117  label="SketchBottom010"
  FullyConstrained = true
  Placement = pos=(0,0,20) rot=(0,0,1;0rad)
  sketch-geometry (6):
    g0: LineSegment StartX=37.5 StartY=-351.614 StartZ=0 EndX=60.6763 EndY=-280.285 EndZ=0
    g1: LineSegment StartX=60.6763 StartY=-280.285 StartZ=0 EndX=0 EndY=-236.201 EndZ=0
    g2: LineSegment StartX=0 StartY=-236.201 StartZ=0 EndX=-60.6763 EndY=-280.285 EndZ=0
    g3: LineSegment StartX=-60.6763 StartY=-280.285 StartZ=0 EndX=-37.5 EndY=-351.614 EndZ=0
    g4: LineSegment StartX=-37.5 StartY=-351.614 StartZ=0 EndX=37.5 EndY=-351.614 EndZ=0
    g5: Circle CenterX=0 CenterY=-300 CenterZ=0 NormalX=0 NormalY=0 NormalZ=1 AngleXU=0 Radius=63.7988
  constraints (15):
    c: Coincident(g0,g1)
    c: Coincident(g1,g2)
    c: Coincident(g2,g3)
    c: Coincident(g3,g4)
    c: Coincident(g4,g0)
    c: Equal(g0, g1-g4) x4
    c: PointOnObject(g0,g5)
    c: PointOnObject(g1,g5)
    c: PointOnObject(g2,g5)
    c: PointOnObject(g3,g5)
    c: PointOnObject(g4,g5)
    c: Horizontal(g4)
    c: DistanceX(g4,g4) = 75
    c: DistanceX(g5) = 0
    c: DistanceY(g5) = -300
FEATURE [Part::Loft] Loft030
  Closed = false
  MaxDegree = 5
  Ruled = false
  Sections = -> [Sketch116,Sketch117]
  Solid = true
FEATURE [Sketcher::SketchObject] Sketch118  label="SketchTop011"
  FullyConstrained = true
  sketch-geometry (6):
    g0: LineSegment StartX=47.5 StartY=-365.378 StartZ=0 EndX=76.8566 EndY=-275.028 EndZ=0
    g1: LineSegment StartX=76.8566 StartY=-275.028 StartZ=0 EndX=1.9185e-12 EndY=-219.188 EndZ=0
    g2: LineSegment StartX=1.9185e-12 StartY=-219.188 StartZ=0 EndX=-76.8566 EndY=-275.028 EndZ=0
    g3: LineSegment StartX=-76.8566 StartY=-275.028 StartZ=0 EndX=-47.5 EndY=-365.378 EndZ=0
    g4: LineSegment StartX=-47.5 StartY=-365.378 StartZ=0 EndX=47.5 EndY=-365.378 EndZ=0
    g5: Circle CenterX=0 CenterY=-300 CenterZ=0 NormalX=0 NormalY=0 NormalZ=1 AngleXU=0 Radius=80.8118
  constraints (15):
    c: Coincident(g0,g1)
    c: Coincident(g1,g2)
    c: Coincident(g2,g3)
    c: Coincident(g3,g4)
    c: Coincident(g4,g0)
    c: Equal(g0, g1-g4) x4
    c: PointOnObject(g0,g5)
    c: PointOnObject(g1,g5)
    c: PointOnObject(g2,g5)
    c: PointOnObject(g3,g5)
    c: PointOnObject(g4,g5)
    c: Horizontal(g4)
    c: DistanceX(g4,g4) = 95
    c: DistanceY(g5) = -300
    c: DistanceX(g5) = 0
FEATURE [Sketcher::SketchObject] Sketch119  label="SketchBottom011"
  FullyConstrained = true
  Placement = pos=(0,0,20) rot=(0,0,1;0rad)
  sketch-geometry (6):
    g0: LineSegment StartX=35 StartY=-348.173 StartZ=0 EndX=56.6312 EndY=-281.599 EndZ=0
    g1: LineSegment StartX=56.6312 StartY=-281.599 StartZ=0 EndX=0 EndY=-240.454 EndZ=0
    g2: LineSegment StartX=0 StartY=-240.454 StartZ=0 EndX=-56.6312 EndY=-281.599 EndZ=0
    g3: LineSegment StartX=-56.6312 StartY=-281.599 StartZ=0 EndX=-35 EndY=-348.173 EndZ=0
    g4: LineSegment StartX=-35 StartY=-348.173 StartZ=0 EndX=35 EndY=-348.173 EndZ=0
    g5: Circle CenterX=0 CenterY=-300 CenterZ=0 NormalX=0 NormalY=0 NormalZ=1 AngleXU=0 Radius=59.5456
  constraints (15):
    c: Coincident(g0,g1)
    c: Coincident(g1,g2)
    c: Coincident(g2,g3)
    c: Coincident(g3,g4)
    c: Coincident(g4,g0)
    c: Equal(g0, g1-g4) x4
    c: PointOnObject(g0,g5)
    c: PointOnObject(g1,g5)
    c: PointOnObject(g2,g5)
    c: PointOnObject(g3,g5)
    c: PointOnObject(g4,g5)
    c: Horizontal(g4)
    c: DistanceX(g4,g4) = 70
    c: DistanceX(g5) = 0
    c: DistanceY(g5) = -300
FEATURE [Part::Loft] Loft031
  Closed = false
  MaxDegree = 5
  Ruled = false
  Sections = -> [Sketch118,Sketch119]
  Solid = true
FEATURE [Part::Cut] Cut048  label="srsCone008"
  Base = -> Loft030
  Placement = pos=(0,0,-36) rot=(0,0,1;0rad)
  Tool = -> Loft031
FEATURE [Part::Fillet] Fillet047
  Base = -> Cut048
  Edges = 5 edges r=1.5: [Edge3,Edge15,Edge16,Edge17,Edge18]
FEATURE [Part::Fillet] Fillet048
  Base = -> Fillet047
  Edges = 5 edges r=1.5: [Edge4,Edge7,Edge11,Edge12,Edge13]
FEATURE [Part::Fillet] Fillet049
  Base = -> Fillet048
  Edges = 5 edges r=2: [Edge1,Edge3,Edge5,Edge15,Edge17]
FEATURE [Part::Fillet] Fillet050  label="srsCone009"
  Base = -> Fillet049
  Edges = 5 edges r=1.5: [Edge63,Edge64,Edge65,Edge66,Edge67]
  Placement = pos=(0,0,-72) rot=(0,0,1;0rad)
FEATURE [Sketcher::SketchObject] Sketch120  label="SketchTop012"
  FullyConstrained = true
  sketch-geometry (6):
    g0: LineSegment StartX=50 StartY=-368.819 StartZ=0 EndX=80.9017 EndY=-273.713 EndZ=0
    g1: LineSegment StartX=80.9017 StartY=-273.713 StartZ=0 EndX=0 EndY=-214.935 EndZ=0
    g2: LineSegment StartX=0 StartY=-214.935 StartZ=0 EndX=-80.9017 EndY=-273.713 EndZ=0
    g3: LineSegment StartX=-80.9017 StartY=-273.713 StartZ=0 EndX=-50 EndY=-368.819 EndZ=0
    g4: LineSegment StartX=-50 StartY=-368.819 StartZ=0 EndX=50 EndY=-368.819 EndZ=0
    g5: Circle CenterX=0 CenterY=-300 CenterZ=0 NormalX=0 NormalY=0 NormalZ=1 AngleXU=0 Radius=85.0651
  constraints (15):
    c: Coincident(g0,g1)
    c: Coincident(g1,g2)
    c: Coincident(g2,g3)
    c: Coincident(g3,g4)
    c: Coincident(g4,g0)
    c: Equal(g0, g1-g4) x4
    c: PointOnObject(g0,g5)
    c: PointOnObject(g1,g5)
    c: PointOnObject(g2,g5)
    c: PointOnObject(g3,g5)
    c: PointOnObject(g4,g5)
    c: Horizontal(g4)
    c: DistanceX(g4,g4) = 100
    c: DistanceY(g5) = -300
    c: DistanceX(g5) = 0
FEATURE [Sketcher::SketchObject] Sketch121  label="SketchBottom012"
  FullyConstrained = true
  Placement = pos=(0,0,20) rot=(0,0,1;0rad)
  sketch-geometry (6):
    g0: LineSegment StartX=37.5 StartY=-351.614 StartZ=0 EndX=60.6763 EndY=-280.285 EndZ=0
    g1: LineSegment StartX=60.6763 StartY=-280.285 StartZ=0 EndX=0 EndY=-236.201 EndZ=0
    g2: LineSegment StartX=0 StartY=-236.201 StartZ=0 EndX=-60.6763 EndY=-280.285 EndZ=0
    g3: LineSegment StartX=-60.6763 StartY=-280.285 StartZ=0 EndX=-37.5 EndY=-351.614 EndZ=0
    g4: LineSegment StartX=-37.5 StartY=-351.614 StartZ=0 EndX=37.5 EndY=-351.614 EndZ=0
    g5: Circle CenterX=0 CenterY=-300 CenterZ=0 NormalX=0 NormalY=0 NormalZ=1 AngleXU=0 Radius=63.7988
  constraints (15):
    c: Coincident(g0,g1)
    c: Coincident(g1,g2)
    c: Coincident(g2,g3)
    c: Coincident(g3,g4)
    c: Coincident(g4,g0)
    c: Equal(g0, g1-g4) x4
    c: PointOnObject(g0,g5)
    c: PointOnObject(g1,g5)
    c: PointOnObject(g2,g5)
    c: PointOnObject(g3,g5)
    c: PointOnObject(g4,g5)
    c: Horizontal(g4)
    c: DistanceX(g4,g4) = 75
    c: DistanceX(g5) = 0
    c: DistanceY(g5) = -300
FEATURE [Part::Loft] Loft032
  Closed = false
  MaxDegree = 5
  Ruled = false
  Sections = -> [Sketch120,Sketch121]
  Solid = true
FEATURE [Sketcher::SketchObject] Sketch122  label="SketchTop013"
  FullyConstrained = true
  sketch-geometry (6):
    g0: LineSegment StartX=47.5 StartY=-365.378 StartZ=0 EndX=76.8566 EndY=-275.028 EndZ=0
    g1: LineSegment StartX=76.8566 StartY=-275.028 StartZ=0 EndX=1.9185e-12 EndY=-219.188 EndZ=0
    g2: LineSegment StartX=1.9185e-12 StartY=-219.188 StartZ=0 EndX=-76.8566 EndY=-275.028 EndZ=0
    g3: LineSegment StartX=-76.8566 StartY=-275.028 StartZ=0 EndX=-47.5 EndY=-365.378 EndZ=0
    g4: LineSegment StartX=-47.5 StartY=-365.378 StartZ=0 EndX=47.5 EndY=-365.378 EndZ=0
    g5: Circle CenterX=0 CenterY=-300 CenterZ=0 NormalX=0 NormalY=0 NormalZ=1 AngleXU=0 Radius=80.8118
  constraints (15):
    c: Coincident(g0,g1)
    c: Coincident(g1,g2)
    c: Coincident(g2,g3)
    c: Coincident(g3,g4)
    c: Coincident(g4,g0)
    c: Equal(g0, g1-g4) x4
    c: PointOnObject(g0,g5)
    c: PointOnObject(g1,g5)
    c: PointOnObject(g2,g5)
    c: PointOnObject(g3,g5)
    c: PointOnObject(g4,g5)
    c: Horizontal(g4)
    c: DistanceX(g4,g4) = 95
    c: DistanceY(g5) = -300
    c: DistanceX(g5) = 0
FEATURE [Sketcher::SketchObject] Sketch123  label="SketchBottom013"
  FullyConstrained = true
  Placement = pos=(0,0,20) rot=(0,0,1;0rad)
  sketch-geometry (6):
    g0: LineSegment StartX=35 StartY=-348.173 StartZ=0 EndX=56.6312 EndY=-281.599 EndZ=0
    g1: LineSegment StartX=56.6312 StartY=-281.599 StartZ=0 EndX=0 EndY=-240.454 EndZ=0
    g2: LineSegment StartX=0 StartY=-240.454 StartZ=0 EndX=-56.6312 EndY=-281.599 EndZ=0
    g3: LineSegment StartX=-56.6312 StartY=-281.599 StartZ=0 EndX=-35 EndY=-348.173 EndZ=0
    g4: LineSegment StartX=-35 StartY=-348.173 StartZ=0 EndX=35 EndY=-348.173 EndZ=0
    g5: Circle CenterX=0 CenterY=-300 CenterZ=0 NormalX=0 NormalY=0 NormalZ=1 AngleXU=0 Radius=59.5456
  constraints (15):
    c: Coincident(g0,g1)
    c: Coincident(g1,g2)
    c: Coincident(g2,g3)
    c: Coincident(g3,g4)
    c: Coincident(g4,g0)
    c: Equal(g0, g1-g4) x4
    c: PointOnObject(g0,g5)
    c: PointOnObject(g1,g5)
    c: PointOnObject(g2,g5)
    c: PointOnObject(g3,g5)
    c: PointOnObject(g4,g5)
    c: Horizontal(g4)
    c: DistanceX(g4,g4) = 70
    c: DistanceX(g5) = 0
    c: DistanceY(g5) = -300
FEATURE [Part::Loft] Loft033
  Closed = false
  MaxDegree = 5
  Ruled = false
  Sections = -> [Sketch122,Sketch123]
  Solid = true
FEATURE [Part::Cut] Cut049  label="srsCone010"
  Base = -> Loft032
  Placement = pos=(0,0,-36) rot=(0,0,1;0rad)
  Tool = -> Loft033
FEATURE [Part::Fillet] Fillet051
  Base = -> Cut049
  Edges = 5 edges r=1.5: [Edge3,Edge15,Edge16,Edge17,Edge18]
FEATURE [Part::Fillet] Fillet052
  Base = -> Fillet051
  Edges = 5 edges r=1.5: [Edge4,Edge7,Edge11,Edge12,Edge13]
FEATURE [Part::Fillet] Fillet053
  Base = -> Fillet052
  Edges = 5 edges r=2: [Edge1,Edge3,Edge5,Edge15,Edge17]
FEATURE [Part::Fillet] Fillet054  label="srsCone011"
  Base = -> Fillet053
  Edges = 5 edges r=1.5: [Edge63,Edge64,Edge65,Edge66,Edge67]
  Placement = pos=(0,0,-90) rot=(0,0,1;0rad)
FEATURE [Sketcher::SketchObject] Sketch124  label="SketchTop014"
  FullyConstrained = true
  sketch-geometry (6):
    g0: LineSegment StartX=50 StartY=-368.819 StartZ=0 EndX=80.9017 EndY=-273.713 EndZ=0
    g1: LineSegment StartX=80.9017 StartY=-273.713 StartZ=0 EndX=0 EndY=-214.935 EndZ=0
    g2: LineSegment StartX=0 StartY=-214.935 StartZ=0 EndX=-80.9017 EndY=-273.713 EndZ=0
    g3: LineSegment StartX=-80.9017 StartY=-273.713 StartZ=0 EndX=-50 EndY=-368.819 EndZ=0
    g4: LineSegment StartX=-50 StartY=-368.819 StartZ=0 EndX=50 EndY=-368.819 EndZ=0
    g5: Circle CenterX=0 CenterY=-300 CenterZ=0 NormalX=0 NormalY=0 NormalZ=1 AngleXU=0 Radius=85.0651
  constraints (15):
    c: Coincident(g0,g1)
    c: Coincident(g1,g2)
    c: Coincident(g2,g3)
    c: Coincident(g3,g4)
    c: Coincident(g4,g0)
    c: Equal(g0, g1-g4) x4
    c: PointOnObject(g0,g5)
    c: PointOnObject(g1,g5)
    c: PointOnObject(g2,g5)
    c: PointOnObject(g3,g5)
    c: PointOnObject(g4,g5)
    c: Horizontal(g4)
    c: DistanceX(g4,g4) = 100
    c: DistanceY(g5) = -300
    c: DistanceX(g5) = 0
FEATURE [Sketcher::SketchObject] Sketch125  label="SketchBottom014"
  FullyConstrained = true
  Placement = pos=(0,0,20) rot=(0,0,1;0rad)
  sketch-geometry (6):
    g0: LineSegment StartX=37.5 StartY=-351.614 StartZ=0 EndX=60.6763 EndY=-280.285 EndZ=0
    g1: LineSegment StartX=60.6763 StartY=-280.285 StartZ=0 EndX=0 EndY=-236.201 EndZ=0
    g2: LineSegment StartX=0 StartY=-236.201 StartZ=0 EndX=-60.6763 EndY=-280.285 EndZ=0
    g3: LineSegment StartX=-60.6763 StartY=-280.285 StartZ=0 EndX=-37.5 EndY=-351.614 EndZ=0
    g4: LineSegment StartX=-37.5 StartY=-351.614 StartZ=0 EndX=37.5 EndY=-351.614 EndZ=0
    g5: Circle CenterX=0 CenterY=-300 CenterZ=0 NormalX=0 NormalY=0 NormalZ=1 AngleXU=0 Radius=63.7988
  constraints (15):
    c: Coincident(g0,g1)
    c: Coincident(g1,g2)
    c: Coincident(g2,g3)
    c: Coincident(g3,g4)
    c: Coincident(g4,g0)
    c: Equal(g0, g1-g4) x4
    c: PointOnObject(g0,g5)
    c: PointOnObject(g1,g5)
    c: PointOnObject(g2,g5)
    c: PointOnObject(g3,g5)
    c: PointOnObject(g4,g5)
    c: Horizontal(g4)
    c: DistanceX(g4,g4) = 75
    c: DistanceX(g5) = 0
    c: DistanceY(g5) = -300
FEATURE [Part::Loft] Loft034
  Closed = false
  MaxDegree = 5
  Ruled = false
  Sections = -> [Sketch124,Sketch125]
  Solid = true
FEATURE [Sketcher::SketchObject] Sketch126  label="SketchTop015"
  FullyConstrained = true
  sketch-geometry (6):
    g0: LineSegment StartX=47.5 StartY=-365.378 StartZ=0 EndX=76.8566 EndY=-275.028 EndZ=0
    g1: LineSegment StartX=76.8566 StartY=-275.028 StartZ=0 EndX=1.9185e-12 EndY=-219.188 EndZ=0
    g2: LineSegment StartX=1.9185e-12 StartY=-219.188 StartZ=0 EndX=-76.8566 EndY=-275.028 EndZ=0
    g3: LineSegment StartX=-76.8566 StartY=-275.028 StartZ=0 EndX=-47.5 EndY=-365.378 EndZ=0
    g4: LineSegment StartX=-47.5 StartY=-365.378 StartZ=0 EndX=47.5 EndY=-365.378 EndZ=0
    g5: Circle CenterX=0 CenterY=-300 CenterZ=0 NormalX=0 NormalY=0 NormalZ=1 AngleXU=0 Radius=80.8118
  constraints (15):
    c: Coincident(g0,g1)
    c: Coincident(g1,g2)
    c: Coincident(g2,g3)
    c: Coincident(g3,g4)
    c: Coincident(g4,g0)
    c: Equal(g0, g1-g4) x4
    c: PointOnObject(g0,g5)
    c: PointOnObject(g1,g5)
    c: PointOnObject(g2,g5)
    c: PointOnObject(g3,g5)
    c: PointOnObject(g4,g5)
    c: Horizontal(g4)
    c: DistanceX(g4,g4) = 95
    c: DistanceY(g5) = -300
    c: DistanceX(g5) = 0
FEATURE [Sketcher::SketchObject] Sketch127  label="SketchBottom015"
  FullyConstrained = true
  Placement = pos=(0,0,20) rot=(0,0,1;0rad)
  sketch-geometry (6):
    g0: LineSegment StartX=35 StartY=-348.173 StartZ=0 EndX=56.6312 EndY=-281.599 EndZ=0
    g1: LineSegment StartX=56.6312 StartY=-281.599 StartZ=0 EndX=0 EndY=-240.454 EndZ=0
    g2: LineSegment StartX=0 StartY=-240.454 StartZ=0 EndX=-56.6312 EndY=-281.599 EndZ=0
    g3: LineSegment StartX=-56.6312 StartY=-281.599 StartZ=0 EndX=-35 EndY=-348.173 EndZ=0
    g4: LineSegment StartX=-35 StartY=-348.173 StartZ=0 EndX=35 EndY=-348.173 EndZ=0
    g5: Circle CenterX=0 CenterY=-300 CenterZ=0 NormalX=0 NormalY=0 NormalZ=1 AngleXU=0 Radius=59.5456
  constraints (15):
    c: Coincident(g0,g1)
    c: Coincident(g1,g2)
    c: Coincident(g2,g3)
    c: Coincident(g3,g4)
    c: Coincident(g4,g0)
    c: Equal(g0, g1-g4) x4
    c: PointOnObject(g0,g5)
    c: PointOnObject(g1,g5)
    c: PointOnObject(g2,g5)
    c: PointOnObject(g3,g5)
    c: PointOnObject(g4,g5)
    c: Horizontal(g4)
    c: DistanceX(g4,g4) = 70
    c: DistanceX(g5) = 0
    c: DistanceY(g5) = -300
FEATURE [Part::Loft] Loft035
  Closed = false
  MaxDegree = 5
  Ruled = false
  Sections = -> [Sketch126,Sketch127]
  Solid = true
FEATURE [Part::Cut] Cut050  label="srsCone012"
  Base = -> Loft034
  Placement = pos=(0,0,-36) rot=(0,0,1;0rad)
  Tool = -> Loft035
FEATURE [Part::Fillet] Fillet055
  Base = -> Cut050
  Edges = 5 edges r=1.5: [Edge3,Edge15,Edge16,Edge17,Edge18]
FEATURE [Part::Fillet] Fillet056
  Base = -> Fillet055
  Edges = 5 edges r=1.5: [Edge4,Edge7,Edge11,Edge12,Edge13]
FEATURE [Part::Fillet] Fillet057
  Base = -> Fillet056
  Edges = 5 edges r=2: [Edge1,Edge3,Edge5,Edge15,Edge17]
FEATURE [Part::Fillet] Fillet058  label="srsCone013"
  Base = -> Fillet057
  Edges = 5 edges r=1.5: [Edge63,Edge64,Edge65,Edge66,Edge67]
  Placement = pos=(0,0,-108) rot=(0,0,1;0rad)
FEATURE [Sketcher::SketchObject] Sketch128  label="SketchTop016"
  FullyConstrained = true
  sketch-geometry (6):
    g0: LineSegment StartX=50 StartY=-368.819 StartZ=0 EndX=80.9017 EndY=-273.713 EndZ=0
    g1: LineSegment StartX=80.9017 StartY=-273.713 StartZ=0 EndX=0 EndY=-214.935 EndZ=0
    g2: LineSegment StartX=0 StartY=-214.935 StartZ=0 EndX=-80.9017 EndY=-273.713 EndZ=0
    g3: LineSegment StartX=-80.9017 StartY=-273.713 StartZ=0 EndX=-50 EndY=-368.819 EndZ=0
    g4: LineSegment StartX=-50 StartY=-368.819 StartZ=0 EndX=50 EndY=-368.819 EndZ=0
    g5: Circle CenterX=0 CenterY=-300 CenterZ=0 NormalX=0 NormalY=0 NormalZ=1 AngleXU=0 Radius=85.0651
  constraints (15):
    c: Coincident(g0,g1)
    c: Coincident(g1,g2)
    c: Coincident(g2,g3)
    c: Coincident(g3,g4)
    c: Coincident(g4,g0)
    c: Equal(g0, g1-g4) x4
    c: PointOnObject(g0,g5)
    c: PointOnObject(g1,g5)
    c: PointOnObject(g2,g5)
    c: PointOnObject(g3,g5)
    c: PointOnObject(g4,g5)
    c: Horizontal(g4)
    c: DistanceX(g4,g4) = 100
    c: DistanceY(g5) = -300
    c: DistanceX(g5) = 0
FEATURE [Sketcher::SketchObject] Sketch129  label="SketchBottom016"
  FullyConstrained = true
  Placement = pos=(0,0,20) rot=(0,0,1;0rad)
  sketch-geometry (6):
    g0: LineSegment StartX=37.5 StartY=-351.614 StartZ=0 EndX=60.6763 EndY=-280.285 EndZ=0
    g1: LineSegment StartX=60.6763 StartY=-280.285 StartZ=0 EndX=0 EndY=-236.201 EndZ=0
    g2: LineSegment StartX=0 StartY=-236.201 StartZ=0 EndX=-60.6763 EndY=-280.285 EndZ=0
    g3: LineSegment StartX=-60.6763 StartY=-280.285 StartZ=0 EndX=-37.5 EndY=-351.614 EndZ=0
    g4: LineSegment StartX=-37.5 StartY=-351.614 StartZ=0 EndX=37.5 EndY=-351.614 EndZ=0
    g5: Circle CenterX=0 CenterY=-300 CenterZ=0 NormalX=0 NormalY=0 NormalZ=1 AngleXU=0 Radius=63.7988
  constraints (15):
    c: Coincident(g0,g1)
    c: Coincident(g1,g2)
    c: Coincident(g2,g3)
    c: Coincident(g3,g4)
    c: Coincident(g4,g0)
    c: Equal(g0, g1-g4) x4
    c: PointOnObject(g0,g5)
    c: PointOnObject(g1,g5)
    c: PointOnObject(g2,g5)
    c: PointOnObject(g3,g5)
    c: PointOnObject(g4,g5)
    c: Horizontal(g4)
    c: DistanceX(g4,g4) = 75
    c: DistanceX(g5) = 0
    c: DistanceY(g5) = -300
FEATURE [Part::Extrusion] Extrude  label="top"
  Base = -> Sketch129
  Dir = (0,0,1)
  DirMode = 2
  FaceMakerClass = Part::FaceMakerBullseye
  LengthFwd = 4
  LengthRev = 0
  Placement = pos=(0,0,-40) rot=(0,0,1;0rad)
  Solid = true
  Symmetric = false
FEATURE [Sketcher::SketchObject] Sketch  label="logoPanel"
  FullyConstrained = true
  Placement = pos=(0,0,-126) rot=(0,0,1;0rad)
  sketch-geometry (4):
    g0: LineSegment StartX=29.9062 StartY=-352 StartZ=0 EndX=27 EndY=-348 EndZ=0
    g1: LineSegment StartX=-27 StartY=-348 StartZ=0 EndX=-29.9062 EndY=-352 EndZ=0
    g2: LineSegment StartX=29.9062 StartY=-352 StartZ=0 EndX=-29.9062 EndY=-352 EndZ=0
    g3: LineSegment StartX=-27 StartY=-348 StartZ=0 EndX=27 EndY=-348 EndZ=0
  constraints (12):
    c: DistanceY(g1) = -352
    c: DistanceY(g1) = -348
    c: Coincident(g2,g0)
    c: Coincident(g2,g1)
    c: Horizontal(g2)
    c: Angle(g2,g1) = 0.942478
    c: Angle(g0,g2) = 0.942478
    c: DistanceX(g1) = -27
    c: DistanceX(g0) = 27
    c: Coincident(g3,g1)
    c: Coincident(g3,g0)
    c: Horizontal(g3)
FEATURE [Part::Feature] Part__Feature154  label="logoTopCut001"
  Placement = pos=(-31.2,-352,-123) rot=(0,0,1;0rad)
  shape: bbox 22.79 x 8 x 17.08 mm, 886 faces (baked)
FEATURE [Sketcher::SketchObject] Sketch130  label="logoPanel001"
  FullyConstrained = true
  Placement = pos=(0,0,-126) rot=(0,0,1;0rad)
  sketch-geometry (4):
    g0: LineSegment StartX=33.0778 StartY=-370 StartZ=0 EndX=20 EndY=-352 EndZ=0
    g1: LineSegment StartX=20 StartY=-352 StartZ=0 EndX=-20 EndY=-352 EndZ=0
    g2: LineSegment StartX=-20 StartY=-352 StartZ=0 EndX=-33.0778 EndY=-370 EndZ=0
    g3: LineSegment StartX=33.0778 StartY=-370 StartZ=0 EndX=-33.0778 EndY=-370 EndZ=0
  constraints (12):
    c: Coincident(g1,g0)
    c: Horizontal(g1)
    c: Coincident(g2,g1)
    c: DistanceY(g1) = -352
    c: Coincident(g3,g0)
    c: Coincident(g3,g2)
    c: Horizontal(g3)
    c: Angle(g3,g2) = 0.942478
    c: Angle(g0,g3) = 0.942478
    c: DistanceX(g0) = 20
    c: DistanceX(g1) = -20
    c: DistanceY(g2) = -370
FEATURE [Part::Feature] Part__Feature  label="ips7100s"
  Placement = pos=(24,-310,-121) rot=(0,0,1;0rad)
  shape: bbox 48.08 x 13.98 x 44.07 mm, 1935 faces (baked)
FEATURE [Part::Feature] Part__Feature155  label="fan"
  Placement = pos=(22.5475,33.2927,6) rot=(-0.588042,0.808831,0;3.14159rad)
  shape: bbox 15 x 15 x 4.502 mm, 133 faces (baked)
FEATURE [Part::Feature] Part__Feature001  label="plastic"
  Placement = pos=(22,36,-5.99e-13) rot=(1,0,0;3.14159rad)
  shape: bbox 48 x 37 x 12 mm, 162 faces, 21 solids (baked)
FEATURE [Part::Feature] Part__Feature002  label="metal_cover_connector"
  Placement = pos=(-2,18.5,11.5) rot=(0,0.707107,0.707107;3.14159rad)
  shape: bbox 48 x 37 x 6 mm, 58 faces (baked)
FEATURE [Part::Feature] Part__Feature003  label="metal_cover_fan"
  Placement = pos=(-2,18.5,0.5) rot=(0,-0.707107,0.707107;3.14159rad)
  shape: bbox 48 x 37 x 6 mm, 63 faces (baked)
FEATURE [Part::Feature] Part__Feature004  label="1_27mm_pin_right_angle"
  Placement = pos=(-0.770082,-1.65718,-0.233527) rot=(0,0,1;0rad)
  shape: bbox 2.2 x 4.2 x 0.4 mm, 17 faces (baked)
FEATURE [Part::Feature] Part__Feature005  label="1_27mm_plastic_for_pin"
  Placement = pos=(-0.452582,-1.45718,-0.233527) rot=(0,1,0;1.5708rad)
  shape: bbox 1.905 x 1 x 1.27 mm, 10 faces (baked)
FEATURE [Part::Feature] Part__Feature006  label="1_27mm_pin_right_angle001"
  Placement = pos=(-0.770082,-1.65718,-0.233527) rot=(0,0,1;0rad)
  shape: bbox 2.2 x 4.2 x 0.4 mm, 17 faces (baked)
FEATURE [Part::Feature] Part__Feature007  label="1_27mm_plastic_for_pin001"
  Placement = pos=(-0.452582,-1.45718,-0.233527) rot=(0,1,0;1.5708rad)
  shape: bbox 1.905 x 1 x 1.27 mm, 10 faces (baked)
FEATURE [Part::Feature] Part__Feature008  label="1_27mm_pin_right_angle002"
  Placement = pos=(-0.770082,-1.65718,-0.233527) rot=(0,0,1;0rad)
  shape: bbox 2.2 x 4.2 x 0.4 mm, 17 faces (baked)
FEATURE [Part::Feature] Part__Feature009  label="1_27mm_plastic_for_pin002"
  Placement = pos=(-0.452582,-1.45718,-0.233527) rot=(0,1,0;1.5708rad)
  shape: bbox 1.905 x 1 x 1.27 mm, 10 faces (baked)
FEATURE [Part::Feature] Part__Feature010  label="1_27mm_pin_right_angle003"
  Placement = pos=(-0.770082,-1.65718,-0.233527) rot=(0,0,1;0rad)
  shape: bbox 2.2 x 4.2 x 0.4 mm, 17 faces (baked)
FEATURE [Part::Feature] Part__Feature011  label="1_27mm_plastic_for_pin003"
  Placement = pos=(-0.452582,-1.45718,-0.233527) rot=(0,1,0;1.5708rad)
  shape: bbox 1.905 x 1 x 1.27 mm, 10 faces (baked)
FEATURE [Part::Feature] Part__Feature012  label="1_27mm_pin_right_angle004"
  Placement = pos=(-0.770082,-1.65718,-0.233527) rot=(0,0,1;0rad)
  shape: bbox 2.2 x 4.2 x 0.4 mm, 17 faces (baked)
FEATURE [Part::Feature] Part__Feature013  label="1_27mm_plastic_for_pin004"
  Placement = pos=(-0.452582,-1.45718,-0.233527) rot=(0,1,0;1.5708rad)
  shape: bbox 1.905 x 1 x 1.27 mm, 10 faces (baked)
FEATURE [Part::Feature] Part__Feature014  label="1_27mm_pin_right_angle005"
  Placement = pos=(-0.770082,-1.65718,-0.233527) rot=(0,0,1;0rad)
  shape: bbox 2.2 x 4.2 x 0.4 mm, 17 faces (baked)
FEATURE [Part::Feature] Part__Feature015  label="1_27mm_plastic_for_pin005"
  Placement = pos=(-0.452582,-1.45718,-0.233527) rot=(0,1,0;1.5708rad)
  shape: bbox 1.905 x 1 x 1.27 mm, 10 faces (baked)
FEATURE [Part::Feature] Part__Feature016  label="1_27mm_pin_right_angle006"
  Placement = pos=(-0.770082,-1.65718,-0.233527) rot=(0,0,1;0rad)
  shape: bbox 2.2 x 4.2 x 0.4 mm, 17 faces (baked)
FEATURE [Part::Feature] Part__Feature017  label="1_27mm_plastic_for_pin006"
  Placement = pos=(-0.452582,-1.45718,-0.233527) rot=(0,1,0;1.5708rad)
  shape: bbox 1.905 x 1 x 1.27 mm, 10 faces (baked)
FEATURE [Part::Feature] Part__Feature018  label="1_27mm_pin_right_angle007"
  Placement = pos=(-0.770082,-1.65718,-0.233527) rot=(0,0,1;0rad)
  shape: bbox 2.2 x 4.2 x 0.4 mm, 17 faces (baked)
FEATURE [Part::Feature] Part__Feature019  label="1_27mm_plastic_for_pin007"
  Placement = pos=(-0.452582,-1.45718,-0.233527) rot=(0,1,0;1.5708rad)
  shape: bbox 1.905 x 1 x 1.27 mm, 10 faces (baked)
FEATURE [Part::Feature] Part__Feature020  label="1_27mm_pin_right_angle008"
  Placement = pos=(-0.770082,-1.65718,-0.233527) rot=(0,0,1;0rad)
  shape: bbox 2.2 x 4.2 x 0.4 mm, 17 faces (baked)
FEATURE [Part::Feature] Part__Feature021  label="1_27mm_plastic_for_pin008"
  Placement = pos=(-0.452582,-1.45718,-0.233527) rot=(0,1,0;1.5708rad)
  shape: bbox 1.905 x 1 x 1.27 mm, 10 faces (baked)
FEATURE [Part::Feature] Part__Feature156  label="1_27mm_pin_right_angle009"
  Placement = pos=(-0.770082,-1.65718,-0.233527) rot=(0,0,1;0rad)
  shape: bbox 2.2 x 4.2 x 0.4 mm, 17 faces (baked)
FEATURE [Part::Feature] Part__Feature157  label="1_27mm_plastic_for_pin009"
  Placement = pos=(-0.452582,-1.45718,-0.233527) rot=(0,1,0;1.5708rad)
  shape: bbox 1.905 x 1 x 1.27 mm, 10 faces (baked)
FEATURE [App::Part] __27mm_single_pin_assembled  label="1_27mm_single_pin_assembled"
  Group = -> [Part__Feature004,Part__Feature005]
  Origin = -> Origin
  Placement = pos=(-0.361489,-0.21886,0.454215) rot=(0,0,1;0rad)
FEATURE [App::Part] __27mm_single_pin_assembled001  label="1_27mm_single_pin_assembled001"
  Group = -> [Part__Feature006,Part__Feature007]
  Origin = -> Origin001
  Placement = pos=(-0.361489,-0.21886,-0.795785) rot=(0,0,1;0rad)
FEATURE [App::Part] __27mm_single_pin_assembled002  label="1_27mm_single_pin_assembled002"
  Group = -> [Part__Feature008,Part__Feature009]
  Origin = -> Origin002
  Placement = pos=(-0.361489,-0.21886,-2.04579) rot=(0,0,1;0rad)
FEATURE [App::Part] __27mm_single_pin_assembled003  label="1_27mm_single_pin_assembled003"
  Group = -> [Part__Feature010,Part__Feature011]
  Origin = -> Origin003
  Placement = pos=(-0.361489,-0.21886,-3.29579) rot=(0,0,1;0rad)
FEATURE [App::Part] __27mm_single_pin_assembled004  label="1_27mm_single_pin_assembled004"
  Group = -> [Part__Feature012,Part__Feature013]
  Origin = -> Origin004
  Placement = pos=(-0.361489,-0.21886,-4.54579) rot=(0,0,1;0rad)
FEATURE [App::Part] __27mm_single_pin_assembled005  label="1_27mm_single_pin_assembled005"
  Group = -> [Part__Feature014,Part__Feature015]
  Origin = -> Origin005
  Placement = pos=(-3.17165,-0.21886,-3.76284) rot=(0,1,0;3.14159rad)
FEATURE [App::Part] __27mm_single_pin_assembled006  label="1_27mm_single_pin_assembled006"
  Group = -> [Part__Feature016,Part__Feature017]
  Origin = -> Origin006
  Placement = pos=(-3.17165,-0.21886,-5.01284) rot=(0,1,0;3.14159rad)
FEATURE [App::Part] __27mm_single_pin_assembled007  label="1_27mm_single_pin_assembled007"
  Group = -> [Part__Feature018,Part__Feature019]
  Origin = -> Origin007
  Placement = pos=(-3.17165,-0.21886,-0.0128383) rot=(0,1,0;3.14159rad)
FEATURE [App::Part] __27mm_single_pin_assembled008  label="1_27mm_single_pin_assembled008"
  Group = -> [Part__Feature020,Part__Feature021]
  Origin = -> Origin008
  Placement = pos=(-3.17165,-0.21886,-2.51284) rot=(0,1,0;3.14159rad)
FEATURE [App::Part] __27mm_single_pin_assembled009  label="1_27mm_single_pin_assembled009"
  Group = -> [Part__Feature156,Part__Feature157]
  Origin = -> Origin009
  Placement = pos=(-3.17165,-0.21886,-1.26284) rot=(0,1,0;3.14159rad)
FEATURE [App::Part] __27mm_2x10pin  label="1_27mm_2x10pin"
  Group = -> [__27mm_single_pin_assembled,__27mm_single_pin_assembled001,__27mm_single_pin_assembled002,__27mm_single_pin_assembled003,__27mm_single_pin_assembled004,__27mm_single_pin_assembled005,__27mm_single_pin_assembled006,__27mm_single_pin_assembled007,__27mm_single_pin_assembled008,__27mm_single_pin_assembled009]
  Origin = -> Origin010
  Placement = pos=(18.0516,5.67069,10.176) rot=(1,0,0;1.5708rad)
FEATURE [App::Part] pms7003
  Group = -> [Part__Feature155,Part__Feature001,Part__Feature002,Part__Feature003,__27mm_2x10pin]
  Origin = -> Origin011
  Placement = pos=(2,-286.5,-118) rot=(1,0,0;1.5708rad)
FEATURE [Part::Feature] Part__Feature158  label="SCD30"
  Placement = pos=(-1.5,-271.75,-52) rot=(0,0,1;0rad)
  shape: bbox 35.11 x 7.027 x 23.02 mm, 2292 faces, 25 solids (baked)
FEATURE [Part::Feature] Part__Feature159  label="SOLID"
  shape: bbox 1 x 0.5 x 0.5 mm, 28 faces (baked)
FEATURE [App::Part] C_0402_1005Metric
  Group = -> [Part__Feature159]
  Origin = -> Origin012
  Placement = pos=(120.904,-86.868,1.65) rot=(0,0,1;0rad)
FEATURE [Part::Feature] Part__Feature160  label="COMPOUND"
  shape: bbox 2.998 x 2.998 x 0.9931 mm, 45 faces, 8 solids (baked)
FEATURE [Part::Feature] Part__Feature161  label="COMPOUND001"
  shape: bbox 6 x 2.96 x 4.95 mm, 229 faces, 7 solids (baked)
FEATURE [Part::Feature] Part__Feature162  label="COMPOUND002"
  shape: bbox 6 x 2.96 x 4.95 mm, 229 faces, 7 solids (baked)
FEATURE [Part::Feature] Part__Feature163  label="SOLID001"
  shape: bbox 1 x 0.5 x 0.5 mm, 28 faces (baked)
FEATURE [App::Part] C_0402_1005Metric001
  Group = -> [Part__Feature163]
  Origin = -> Origin016
  Placement = pos=(124.968,-87.376,1.65) rot=(0,0,-1;1.5708rad)
FEATURE [Part::Feature] Part__Feature164  label="SOLID002"
  shape: bbox 0.65 x 0.35 x 0.2 mm, 24 faces (baked)
FEATURE [App::Part] LED_0201_0603Metric
  Group = -> [Part__Feature164]
  Origin = -> Origin017
  Placement = pos=(117.196,-81.5848,1.65) rot=(0,0,1;0rad)
FEATURE [Part::Feature] Part__Feature165  label="SOLID003"
  shape: bbox 2.54 x 10.16 x 11.54 mm, 100 faces (baked)
FEATURE [Part::Feature] Part__Feature166  label="SOLID004"
  shape: bbox 1 x 0.5 x 0.35 mm, 26 faces (baked)
FEATURE [Part::Feature] Part__Feature167  label="SOLID005"
  shape: bbox 1 x 2 x 0.45 mm, 140 faces (baked)
FEATURE [Part::Feature] Part__Feature168  label="COMPOUND003"
  shape: bbox 25.4 x 17.78 x 1.6 mm, 31 faces (baked)
FEATURE [App::Part] PinHeader_1x04_P2_54mm_Vertical  label="PinHeader_1x04_P2.54mm_Vertical"
  Group = -> [Part__Feature165]
  Origin = -> Origin018
  Placement = pos=(120.904,-91.2114,-0.05) rot=(-0.707107,0.707107,0;3.14159rad)
FEATURE [App::Part] R_0402_1005Metric
  Group = -> [Part__Feature166]
  Origin = -> Origin019
  Placement = pos=(119.634,-84.328,1.65) rot=(0,0,1;1.5708rad)
FEATURE [App::Part] R_Array_Concave_4x0402
  Group = -> [Part__Feature167]
  Origin = -> Origin020
  Placement = pos=(129.642,-85.3186,1.65) rot=(0,0,1;0rad)
FEATURE [App::Part] SENSOR_AHT20_GAE
  Group = -> [Part__Feature160]
  Origin = -> Origin013
  Placement = pos=(125.019,-83.8708,1.65) rot=(0,0,1;0rad)
FEATURE [App::Part] SM04B_SRSS_TB_LF__SN_  label="SM04B-SRSS-TB_LF__SN_"
  Group = -> [Part__Feature161]
  Origin = -> Origin014
  Placement = pos=(132.732,-85.8012,1.15) rot=(0.57735,0.57735,0.57735;2.0944rad)
FEATURE [App::Part] SM04B_SRSS_TB_LF__SN_001  label="SM04B-SRSS-TB_LF__SN_001"
  Group = -> [Part__Feature162]
  Origin = -> Origin015
  Placement = pos=(116.391,-85.8266,1.15) rot=(-0.57735,0.57735,0.57735;4.18879rad)
FEATURE [App::Part] Open_CASCADE_STEP_translator_6_9_1  label="BME280"
  Group = -> [C_0402_1005Metric,SENSOR_AHT20_GAE,SM04B_SRSS_TB_LF__SN_,SM04B_SRSS_TB_LF__SN_001,C_0402_1005Metric001,LED_0201_0603Metric,PinHeader_1x04_P2_54mm_Vertical,R_0402_1005Metric,R_Array_Concave_4x0402,Part__Feature168]
  Origin = -> Origin021
  Placement = pos=(-125,-315,36.25) rot=(-1,0,0;4.71239rad)
FEATURE [Part::Feature] Part__Feature169  label="COZIR"
  Placement = pos=(5.41,2.98,10) rot=(0,0,1;0rad)
  shape: bbox 51.61 x 17 x 50.23 mm, 43 faces (baked)
FEATURE [Part::Feature] Part__Feature170  label="COMPOUND004"
  shape: bbox 3.14 x 5 x 10.76 mm, 60 faces, 10 solids (baked)
FEATURE [App::Part] COZIR_Sensor_v2  label="COZIR Sensor v2"
  Group = -> [Part__Feature169,Part__Feature170]
  Origin = -> Origin022
  Placement = pos=(53.75,-287.25,-104.75) rot=(0,0,1;0rad)
FEATURE [Part::Feature] Part__Feature171  label="cozIRBlink"
  Placement = pos=(0,-264.25,-92) rot=(0,0,1;0rad)
  shape: bbox 21.06 x 9.056 x 38.62 mm, 1727 faces (baked)
FEATURE [Part::Cylinder] Cylinder153  label="SJH-5XD"
  Angle = 360
  AttacherType = Attacher::AttachEngine3D
  FirstAngle = 0
  Height = 19
  Placement = pos=(38,-285,-115) rot=(0,0,1;0rad)
  Radius = 10
  SecondAngle = 0
FEATURE [Part::Feature] Part__Feature172  label="SOLID006"
  shape: bbox 14.22 x 14.22 x 8 mm, 4 faces (baked)
FEATURE [Part::Feature] Part__Feature173  label="COMPOUND005"
  shape: bbox 19 x 19 x 10.5 mm, 41 faces, 0 solids (baked)
FEATURE [App::Part] Document  label="SO2LowCost"
  Group = -> [Part__Feature172,Part__Feature173]
  Origin = -> Origin023
  Placement = pos=(-38,-285,-115) rot=(0,0,1;0rad)
FEATURE [Part::Feature] Part__Feature174  label="SOLID007"
  shape: bbox 1 x 0.5 x 0.5 mm, 28 faces (baked)
FEATURE [App::Part] C_0402_1005Metric002
  Group = -> [Part__Feature174]
  Origin = -> Origin024
  Placement = pos=(120.904,-86.868,1.65) rot=(0,0,1;0rad)
FEATURE [Part::Feature] Part__Feature175  label="COMPOUND006"
  shape: bbox 2.998 x 2.998 x 0.9931 mm, 45 faces, 8 solids (baked)
FEATURE [Part::Feature] Part__Feature176  label="COMPOUND007"
  shape: bbox 6 x 2.96 x 4.95 mm, 229 faces, 7 solids (baked)
FEATURE [Part::Feature] Part__Feature177  label="COMPOUND008"
  shape: bbox 6 x 2.96 x 4.95 mm, 229 faces, 7 solids (baked)
FEATURE [Part::Feature] Part__Feature178  label="SOLID008"
  shape: bbox 1 x 0.5 x 0.5 mm, 28 faces (baked)
FEATURE [App::Part] C_0402_1005Metric003
  Group = -> [Part__Feature178]
  Origin = -> Origin028
  Placement = pos=(124.968,-87.376,1.65) rot=(0,0,-1;1.5708rad)
FEATURE [Part::Feature] Part__Feature179  label="SOLID009"
  shape: bbox 0.65 x 0.35 x 0.2 mm, 24 faces (baked)
FEATURE [App::Part] LED_0201_0603Metric001
  Group = -> [Part__Feature179]
  Origin = -> Origin029
  Placement = pos=(117.196,-81.5848,1.65) rot=(0,0,1;0rad)
FEATURE [Part::Feature] Part__Feature180  label="SOLID010"
  shape: bbox 2.54 x 10.16 x 11.54 mm, 100 faces (baked)
FEATURE [Part::Feature] Part__Feature181  label="SOLID011"
  shape: bbox 1 x 0.5 x 0.35 mm, 26 faces (baked)
FEATURE [Part::Feature] Part__Feature182  label="SOLID012"
  shape: bbox 1 x 2 x 0.45 mm, 140 faces (baked)
FEATURE [Part::Feature] Part__Feature183  label="COMPOUND009"
  shape: bbox 25.4 x 17.78 x 1.6 mm, 31 faces (baked)
FEATURE [App::Part] PinHeader_1x04_P2_54mm_Vertical001  label="PinHeader_1x04_P2.54mm_Vertical001"
  Group = -> [Part__Feature180]
  Origin = -> Origin030
  Placement = pos=(120.904,-91.2114,-0.05) rot=(-0.707107,0.707107,0;3.14159rad)
FEATURE [App::Part] R_0402_1005Metric001
  Group = -> [Part__Feature181]
  Origin = -> Origin031
  Placement = pos=(119.634,-84.328,1.65) rot=(0,0,1;1.5708rad)
FEATURE [App::Part] R_Array_Concave_4x0403
  Group = -> [Part__Feature182]
  Origin = -> Origin032
  Placement = pos=(129.642,-85.3186,1.65) rot=(0,0,1;0rad)
FEATURE [App::Part] SENSOR_AHT20_GAE001
  Group = -> [Part__Feature175]
  Origin = -> Origin025
  Placement = pos=(125.019,-83.8708,1.65) rot=(0,0,1;0rad)
FEATURE [App::Part] SM04B_SRSS_TB_LF__SN_002  label="SM04B-SRSS-TB_LF__SN_002"
  Group = -> [Part__Feature176]
  Origin = -> Origin026
  Placement = pos=(132.732,-85.8012,1.15) rot=(0.57735,0.57735,0.57735;2.0944rad)
FEATURE [App::Part] SM04B_SRSS_TB_LF__SN_003  label="SM04B-SRSS-TB_LF__SN_003"
  Group = -> [Part__Feature177]
  Origin = -> Origin027
  Placement = pos=(116.391,-85.8266,1.15) rot=(-0.57735,0.57735,0.57735;4.18879rad)
FEATURE [App::Part] Open_CASCADE_STEP_translator_6_9_002  label="TMP117"
  Group = -> [C_0402_1005Metric002,SENSOR_AHT20_GAE001,SM04B_SRSS_TB_LF__SN_002,SM04B_SRSS_TB_LF__SN_003,C_0402_1005Metric003,LED_0201_0603Metric001,PinHeader_1x04_P2_54mm_Vertical001,R_0402_1005Metric001,R_Array_Concave_4x0403,Part__Feature183]
  Origin = -> Origin033
  Placement = pos=(-125,-330,36.25) rot=(-1,0,0;4.71239rad)
FEATURE [Part::Feature] Part__Feature184  label="SOLID013"
  shape: bbox 1 x 0.5 x 0.5 mm, 28 faces (baked)
FEATURE [App::Part] C_0402_1005Metric004
  Group = -> [Part__Feature184]
  Origin = -> Origin034
  Placement = pos=(120.904,-86.868,1.65) rot=(0,0,1;0rad)
FEATURE [Part::Feature] Part__Feature185  label="COMPOUND010"
  shape: bbox 2.998 x 2.998 x 0.9931 mm, 45 faces, 8 solids (baked)
FEATURE [Part::Feature] Part__Feature186  label="COMPOUND011"
  shape: bbox 6 x 2.96 x 4.95 mm, 229 faces, 7 solids (baked)
FEATURE [Part::Feature] Part__Feature187  label="COMPOUND012"
  shape: bbox 6 x 2.96 x 4.95 mm, 229 faces, 7 solids (baked)
FEATURE [Part::Feature] Part__Feature188  label="SOLID014"
  shape: bbox 1 x 0.5 x 0.5 mm, 28 faces (baked)
FEATURE [App::Part] C_0402_1005Metric005
  Group = -> [Part__Feature188]
  Origin = -> Origin038
  Placement = pos=(124.968,-87.376,1.65) rot=(0,0,-1;1.5708rad)
FEATURE [Part::Feature] Part__Feature189  label="SOLID015"
  shape: bbox 0.65 x 0.35 x 0.2 mm, 24 faces (baked)
FEATURE [App::Part] LED_0201_0603Metric002
  Group = -> [Part__Feature189]
  Origin = -> Origin039
  Placement = pos=(117.196,-81.5848,1.65) rot=(0,0,1;0rad)
FEATURE [Part::Feature] Part__Feature190  label="SOLID016"
  shape: bbox 2.54 x 10.16 x 11.54 mm, 100 faces (baked)
FEATURE [Part::Feature] Part__Feature191  label="SOLID017"
  shape: bbox 1 x 0.5 x 0.35 mm, 26 faces (baked)
FEATURE [Part::Feature] Part__Feature192  label="SOLID018"
  shape: bbox 1 x 2 x 0.45 mm, 140 faces (baked)
FEATURE [Part::Feature] Part__Feature193  label="COMPOUND013"
  shape: bbox 25.4 x 17.78 x 1.6 mm, 31 faces (baked)
FEATURE [App::Part] PinHeader_1x04_P2_54mm_Vertical002  label="PinHeader_1x04_P2.54mm_Vertical002"
  Group = -> [Part__Feature190]
  Origin = -> Origin040
  Placement = pos=(120.904,-91.2114,-0.05) rot=(-0.707107,0.707107,0;3.14159rad)
FEATURE [App::Part] R_0402_1005Metric002
  Group = -> [Part__Feature191]
  Origin = -> Origin041
  Placement = pos=(119.634,-84.328,1.65) rot=(0,0,1;1.5708rad)
FEATURE [App::Part] R_Array_Concave_4x0404
  Group = -> [Part__Feature192]
  Origin = -> Origin042
  Placement = pos=(129.642,-85.3186,1.65) rot=(0,0,1;0rad)
FEATURE [App::Part] SENSOR_AHT20_GAE002
  Group = -> [Part__Feature185]
  Origin = -> Origin035
  Placement = pos=(125.019,-83.8708,1.65) rot=(0,0,1;0rad)
FEATURE [App::Part] SM04B_SRSS_TB_LF__SN_004  label="SM04B-SRSS-TB_LF__SN_004"
  Group = -> [Part__Feature186]
  Origin = -> Origin036
  Placement = pos=(132.732,-85.8012,1.15) rot=(0.57735,0.57735,0.57735;2.0944rad)
FEATURE [App::Part] SM04B_SRSS_TB_LF__SN_005  label="SM04B-SRSS-TB_LF__SN_005"
  Group = -> [Part__Feature187]
  Origin = -> Origin037
  Placement = pos=(116.391,-85.8266,1.15) rot=(-0.57735,0.57735,0.57735;4.18879rad)
FEATURE [App::Part] Open_CASCADE_STEP_translator_6_9_003  label="LPS22"
  Group = -> [C_0402_1005Metric004,SENSOR_AHT20_GAE002,SM04B_SRSS_TB_LF__SN_004,SM04B_SRSS_TB_LF__SN_005,C_0402_1005Metric005,LED_0201_0603Metric002,PinHeader_1x04_P2_54mm_Vertical002,R_0402_1005Metric002,R_Array_Concave_4x0404,Part__Feature193]
  Origin = -> Origin043
  Placement = pos=(-125,-301,36.25) rot=(-1,0,0;4.71239rad)
FEATURE [Part::Feature] Part__Feature194  label="SOLID019"
  shape: bbox 1 x 0.5 x 0.5 mm, 28 faces (baked)
FEATURE [App::Part] C_0402_1005Metric006
  Group = -> [Part__Feature194]
  Origin = -> Origin044
  Placement = pos=(120.904,-86.868,1.65) rot=(0,0,1;0rad)
FEATURE [Part::Feature] Part__Feature195  label="COMPOUND014"
  shape: bbox 2.998 x 2.998 x 0.9931 mm, 45 faces, 8 solids (baked)
FEATURE [Part::Feature] Part__Feature196  label="COMPOUND015"
  shape: bbox 6 x 2.96 x 4.95 mm, 229 faces, 7 solids (baked)
FEATURE [Part::Feature] Part__Feature197  label="COMPOUND016"
  shape: bbox 6 x 2.96 x 4.95 mm, 229 faces, 7 solids (baked)
FEATURE [Part::Feature] Part__Feature198  label="SOLID020"
  shape: bbox 1 x 0.5 x 0.5 mm, 28 faces (baked)
FEATURE [App::Part] C_0402_1005Metric007
  Group = -> [Part__Feature198]
  Origin = -> Origin048
  Placement = pos=(124.968,-87.376,1.65) rot=(0,0,-1;1.5708rad)
FEATURE [Part::Feature] Part__Feature199  label="SOLID021"
  shape: bbox 0.65 x 0.35 x 0.2 mm, 24 faces (baked)
FEATURE [App::Part] LED_0201_0603Metric003
  Group = -> [Part__Feature199]
  Origin = -> Origin049
  Placement = pos=(117.196,-81.5848,1.65) rot=(0,0,1;0rad)
FEATURE [Part::Feature] Part__Feature200  label="SOLID022"
  shape: bbox 2.54 x 10.16 x 11.54 mm, 100 faces (baked)
FEATURE [Part::Feature] Part__Feature201  label="SOLID023"
  shape: bbox 1 x 0.5 x 0.35 mm, 26 faces (baked)
FEATURE [Part::Feature] Part__Feature202  label="SOLID024"
  shape: bbox 1 x 2 x 0.45 mm, 140 faces (baked)
FEATURE [Part::Feature] Part__Feature203  label="COMPOUND017"
  shape: bbox 25.4 x 17.78 x 1.6 mm, 31 faces (baked)
FEATURE [App::Part] PinHeader_1x04_P2_54mm_Vertical003  label="PinHeader_1x04_P2.54mm_Vertical003"
  Group = -> [Part__Feature200]
  Origin = -> Origin050
  Placement = pos=(120.904,-91.2114,-0.05) rot=(-0.707107,0.707107,0;3.14159rad)
FEATURE [App::Part] R_0402_1005Metric003
  Group = -> [Part__Feature201]
  Origin = -> Origin051
  Placement = pos=(119.634,-84.328,1.65) rot=(0,0,1;1.5708rad)
FEATURE [App::Part] R_Array_Concave_4x0405
  Group = -> [Part__Feature202]
  Origin = -> Origin052
  Placement = pos=(129.642,-85.3186,1.65) rot=(0,0,1;0rad)
FEATURE [App::Part] SENSOR_AHT20_GAE003
  Group = -> [Part__Feature195]
  Origin = -> Origin045
  Placement = pos=(125.019,-83.8708,1.65) rot=(0,0,1;0rad)
FEATURE [App::Part] SM04B_SRSS_TB_LF__SN_006  label="SM04B-SRSS-TB_LF__SN_006"
  Group = -> [Part__Feature196]
  Origin = -> Origin046
  Placement = pos=(132.732,-85.8012,1.15) rot=(0.57735,0.57735,0.57735;2.0944rad)
FEATURE [App::Part] SM04B_SRSS_TB_LF__SN_007  label="SM04B-SRSS-TB_LF__SN_007"
  Group = -> [Part__Feature197]
  Origin = -> Origin047
  Placement = pos=(116.391,-85.8266,1.15) rot=(-0.57735,0.57735,0.57735;4.18879rad)
FEATURE [App::Part] Open_CASCADE_STEP_translator_6_9_004  label="SHT40"
  Group = -> [C_0402_1005Metric006,SENSOR_AHT20_GAE003,SM04B_SRSS_TB_LF__SN_006,SM04B_SRSS_TB_LF__SN_007,C_0402_1005Metric007,LED_0201_0603Metric003,PinHeader_1x04_P2_54mm_Vertical003,R_0402_1005Metric003,R_Array_Concave_4x0405,Part__Feature203]
  Origin = -> Origin053
  Placement = pos=(-125,-278,36.25) rot=(-1,0,0;4.71239rad)
FEATURE [Part::Extrusion] Extrude034  label="logoPanel002"
  Base = -> Sketch
  Dir = (0,0,1)
  DirMode = 2
  FaceMakerClass = Part::FaceMakerBullseye
  LengthFwd = 38
  LengthRev = 0
  Solid = true
  Symmetric = false
FEATURE [Sketcher::SketchObject] Sketch131
  FullyConstrained = true
FEATURE [Sketcher::SketchObject] Sketch132  label="SketchBottom017"
  FullyConstrained = true
  Placement = pos=(0,0,-126) rot=(0,0,1;0rad)
  sketch-geometry (6):
    g0: LineSegment StartX=37.5 StartY=-351.614 StartZ=0 EndX=60.6763 EndY=-280.285 EndZ=0
    g1: LineSegment StartX=60.6763 StartY=-280.285 StartZ=0 EndX=0 EndY=-236.201 EndZ=0
    g2: LineSegment StartX=0 StartY=-236.201 StartZ=0 EndX=-60.6763 EndY=-280.285 EndZ=0
    g3: LineSegment StartX=-60.6763 StartY=-280.285 StartZ=0 EndX=-37.5 EndY=-351.614 EndZ=0
    g4: LineSegment StartX=-37.5 StartY=-351.614 StartZ=0 EndX=37.5 EndY=-351.614 EndZ=0
    g5: Circle CenterX=0 CenterY=-300 CenterZ=0 NormalX=0 NormalY=0 NormalZ=1 AngleXU=0 Radius=63.7988
  constraints (15):
    c: Coincident(g0,g1)
    c: Coincident(g1,g2)
    c: Coincident(g2,g3)
    c: Coincident(g3,g4)
    c: Coincident(g4,g0)
    c: Equal(g0, g1-g4) x4
    c: PointOnObject(g0,g5)
    c: PointOnObject(g1,g5)
    c: PointOnObject(g2,g5)
    c: PointOnObject(g3,g5)
    c: PointOnObject(g4,g5)
    c: Horizontal(g4)
    c: DistanceX(g4,g4) = 75
    c: DistanceX(g5) = 0
    c: DistanceY(g5) = -300
FEATURE [Part::Extrusion] Extrude036  label="legPart1"
  Base = -> Sketch132
  Dir = (0,0,1)
  DirMode = 2
  FaceMakerClass = Part::FaceMakerBullseye
  LengthFwd = 110
  LengthRev = 0
  Solid = true
  Symmetric = false
FEATURE [Sketcher::SketchObject] Sketch133  label="SketchBottom018"
  FullyConstrained = true
  Placement = pos=(0,0,-126) rot=(0,0,1;0rad)
  sketch-geometry (2):
    g0: Circle CenterX=0 CenterY=-300 CenterZ=0 NormalX=0 NormalY=0 NormalZ=1 AngleXU=0 Radius=63.8
    g1: Circle CenterX=0 CenterY=-300 CenterZ=0 NormalX=0 NormalY=0 NormalZ=1 AngleXU=0 Radius=55
  constraints (5):
    c: Diameter(g1) = 110
    c: Diameter(g0) = 127.6
    c: DistanceY(g0) = -300
    c: DistanceX(g0) = 0
    c: Coincident(g0,g1)
FEATURE [Part::Extrusion] Extrude037  label="legPart002"
  Base = -> Sketch133
  Dir = (0,0,1)
  DirMode = 2
  FaceMakerClass = Part::FaceMakerBullseye
  LengthFwd = 110
  LengthRev = 0
  Solid = true
  Symmetric = false
FEATURE [Part::MultiCommon] Common  label="legs"
  Shapes = -> [Extrude037,Extrude036]
FEATURE [Part::Extrusion] Extrude035  label="srsCut"
  Base = -> Sketch130
  Dir = (0,0,1)
  DirMode = 2
  FaceMakerClass = Part::FaceMakerBullseye
  LengthFwd = 38
  LengthRev = 0
  Solid = true
  Symmetric = false
FEATURE [Part::MultiFuse] Fusion  label="logoLevels"
  Shapes = -> [Fillet050,Fillet054]
FEATURE [Part::Cut] Cut051  label="srsLogoLevels"
  Base = -> Fusion
  Tool = -> Extrude035
FEATURE [Part::MultiFuse] Fusion093  label="legeLevels"
  Shapes = -> [Cut051,Extrude034]
FEATURE [Part::Cut] Cut052  label="srsLogoLevels001"
  Base = -> Fusion093
  Tool = -> Part__Feature154
FEATURE [Part::MultiFuse] Fusion094  label="srsPentagon"
  Shapes = -> [Cut052,Fillet058,Fillet046,Fillet042,Fillet038,Fillet034,Common,Extrude]
FEATURE [Sketcher::SketchObject] Sketch134
  FullyConstrained = true
  Placement = pos=(0,-234,0) rot=(1,0,0;1.5708rad)
  sketch-geometry (8):
    g0: LineSegment StartX=-13 StartY=10 StartZ=0 EndX=13 EndY=10 EndZ=0
    g1: LineSegment StartX=13 StartY=10 StartZ=0 EndX=13 EndY=-16 EndZ=0
    g2: LineSegment StartX=13 StartY=-16 StartZ=0 EndX=-13 EndY=-16 EndZ=0
    g3: LineSegment StartX=-13 StartY=-16 StartZ=0 EndX=-13 EndY=10 EndZ=0
    g4: LineSegment StartX=-20 StartY=-20 StartZ=0 EndX=-20 EndY=17 EndZ=0
    g5: LineSegment StartX=-20 StartY=17 StartZ=0 EndX=20 EndY=17 EndZ=0
    g6: LineSegment StartX=20 StartY=17 StartZ=0 EndX=20 EndY=-20 EndZ=0
    g7: LineSegment StartX=-20 StartY=-20 StartZ=0 EndX=20 EndY=-20 EndZ=0
  constraints (24):
    c: Coincident(g0,g1)
    c: Coincident(g1,g2)
    c: Coincident(g2,g3)
    c: Coincident(g3,g0)
    c: Horizontal(g0)
    c: Horizontal(g2)
    c: Vertical(g1)
    c: Vertical(g3)
    c: DistanceY(g2,g0) = 26
    c: DistanceX(g0,g0) = 26
    c: DistanceX(g0) = -13
    c: Vertical(g4)
    c: Coincident(g5,g4)
    c: Horizontal(g5)
    c: DistanceX(g4,g0) = 7
    c: DistanceY(g0,g4) = 7
    c: DistanceX(g0,g5) = 7
    c: DistanceY(g4) = -20
    c: Coincident(g6,g5)
    c: Vertical(g6)
    c: Coincident(g7,g4)
    c: Coincident(g7,g6)
    c: Horizontal(g7)
    c: DistanceY(g2) = -16
FEATURE [Part::Extrusion] Extrude038  label="tSlotHold"
  Base = -> Sketch134
  Dir = (0,-1,2e-16)
  DirMode = 2
  FaceMakerClass = Part::FaceMakerBullseye
  LengthFwd = 45
  LengthRev = 0
  Solid = true
  Symmetric = false
FEATURE [Part::Feature] Part__Feature204  label="PH Pan head screw M2x0.40 x 6"
  Placement = pos=(101.945,-83.8381,-1.82512) rot=(0,0,1;3.14159rad)
  shape: bbox 4.006 x 4.006 x 7.57 mm, 32 faces (baked)
FEATURE [Part::Feature] Part__Feature205  label="Part 8"
  Placement = pos=(178.445,24.1619,-39.4251) rot=(0,1,0;3.14159rad)
  shape: bbox 166 x 27.4 x 2 mm, 14 faces (baked)
FEATURE [Part::Feature] Part__Feature206  label="event gore PMF100320"
  Placement = pos=(79.1369,-76.58,11.5741) rot=(0,-1,0;0.037482rad)
  shape: bbox 2.468 x 15.31 x 15.29 mm, 4 faces (baked)
FEATURE [Part::Feature] Part__Feature207  label="event gore PMF100321"
  Placement = pos=(79.1369,-76.58,11.5741) rot=(0,-1,0;0.037482rad)
  shape: bbox 15.95 x 18.27 x 18.26 mm, 114 faces (baked)
FEATURE [Part::Feature] Part__Feature208  label="PH Pan head screw M2x0.40 x 007"
  Placement = pos=(101.945,24.1619,-1.82512) rot=(0,0,1;0rad)
  shape: bbox 4.006 x 4.006 x 7.57 mm, 32 faces (baked)
FEATURE [Part::Feature] Part__Feature209  label="WPB20-28-7_3D"
  Placement = pos=(178.445,24.1619,30.5749) rot=(0,0,1;0rad)
  shape: bbox 200.6 x 280.6 x 46.01 mm, 1035 faces (baked)
FEATURE [Part::Feature] Part__Feature210  label="PH Pan head screw M2x0.40 x 008"
  Placement = pos=(254.945,-83.8381,-1.82512) rot=(0,0,1;3.14159rad)
  shape: bbox 4.006 x 4.006 x 7.57 mm, 32 faces (baked)
FEATURE [Part::Feature] Part__Feature211  label="Cable Gland PG7-PG19 Lock Nut_PG13.5"
  Placement = pos=(223.445,-112.627,11.6686) rot=(1,0,0;0.037482rad)
  shape: bbox 29.02 x 6.449 x 29 mm, 29 faces (baked)
FEATURE [Part::Feature] Part__Feature212  label="Cable Gland PG7-PG19 Body_PG13.5"
  Placement = pos=(223.445,-118.923,11.4325) rot=(0,-0.01874,0.999824;3.14159rad)
  shape: bbox 25.06 x 36.36 x 23.18 mm, 156 faces (baked)
FEATURE [Part::Feature] Part__Feature213  label="Cable Gland PG7-PG19 Washer_PG13.5"
  Placement = pos=(223.445,-115.725,11.5524) rot=(0,-0.01874,0.999824;3.14159rad)
  shape: bbox 25 x 2.136 x 25.03 mm, 4 faces (baked)
FEATURE [Part::Feature] Part__Feature214  label="Cable Gland PG7-PG19 Gland Nut_PG13.5"
  Placement = pos=(223.445,-132.014,10.9416) rot=(0.825324,-0.010582,0.56456;3.17253rad)
  shape: bbox 25.82 x 20.19 x 25.8 mm, 50 faces (baked)
FEATURE [Part::Feature] Part__Feature215  label="Cable Gland PG7-PG19 Sleeve_PG13.5"
  Placement = pos=(223.445,-137.51,10.7355) rot=(0,-0.01874,0.999824;3.14159rad)
  shape: bbox 15.7 x 8.583 x 15.99 mm, 4 faces (baked)
FEATURE [App::Part] Cable_Gland_PG7_PG19__PG13_5__1_  label="Cable Gland PG7-PG19, PG13.5 <1>"
  Group = -> [Part__Feature211,Part__Feature212,Part__Feature213,Part__Feature214,Part__Feature215]
  Origin = -> Origin054
FEATURE [Part::Feature] Part__Feature216  label="WPMB-M4-2"
  Placement = pos=(178.445,24.1619,-13.4251) rot=(0,1,0;3.14159rad)
  shape: bbox 91.99 x 91.99 x 12.05 mm, 899 faces (baked)
FEATURE [Part::Feature] Part__Feature217  label="Micro_USB_Plug v10"
  Placement = pos=(255.557,33.7719,7.31475) rot=(0.577351,0.577352,-0.577348;4.18879rad)
  shape: bbox 4.78 x 0.2 x 0.4672 mm, 14 faces (baked)
FEATURE [Part::Feature] Part__Feature218  label="Micro_USB_Plug_Connector"
  Placement = pos=(255.557,33.7719,7.31475) rot=(0.577351,0.577352,-0.577348;4.18879rad)
  shape: bbox 7.5 x 6.85 x 1.85 mm, 68 faces (baked)
FEATURE [Part::Feature] Part__Feature219  label="Micro_USB_Plug v011"
  Placement = pos=(255.557,33.7719,7.31475) rot=(0.577351,0.577352,-0.577348;4.18879rad)
  shape: bbox 4.78 x 0.2 x 0.4672 mm, 14 faces (baked)
FEATURE [Part::Feature] Part__Feature220  label="Micro_USB_Plug_Connector001"
  Placement = pos=(255.557,33.7719,7.31475) rot=(0.577351,0.577352,-0.577348;4.18879rad)
  shape: bbox 4.574 x 0.32 x 1.625 mm, 11 faces (baked)
FEATURE [Part::Feature] Part__Feature221  label="micro_usb_plug rt angle"
  Placement = pos=(255.557,33.7719,7.31475) rot=(0.577351,0.577352,-0.577348;4.18879rad)
  shape: bbox 12.25 x 19.75 x 7.006 mm, 151 faces (baked)
FEATURE [Part::Feature] Part__Feature222  label="Micro_USB_Plug v012"
  Placement = pos=(255.557,33.7719,7.31475) rot=(0.577351,0.577352,-0.577348;4.18879rad)
  shape: bbox 4.78 x 0.2 x 0.4672 mm, 14 faces (baked)
FEATURE [Part::Feature] Part__Feature223  label="Micro_USB_Plug v013"
  Placement = pos=(255.557,33.7719,7.31475) rot=(0.577351,0.577352,-0.577348;4.18879rad)
  shape: bbox 4.78 x 0.2 x 0.4672 mm, 14 faces (baked)
FEATURE [Part::Feature] Part__Feature224  label="Wire"
  Placement = pos=(255.557,33.7719,7.31475) rot=(0.577351,0.577352,-0.577348;4.18879rad)
  shape: bbox 3.2 x 9.5 x 3.2 mm, 3 faces (baked)
FEATURE [Part::Feature] Part__Feature225  label="Micro_USB_Plug_Connector002"
  Placement = pos=(255.557,33.7719,7.31475) rot=(0.577351,0.577352,-0.577348;4.18879rad)
  shape: bbox 4.7 x 0.32 x 1.625 mm, 11 faces (baked)
FEATURE [Part::Feature] Part__Feature226  label="Micro_USB_Plug v014"
  Placement = pos=(255.557,33.7719,7.31475) rot=(0.577351,0.577352,-0.577348;4.18879rad)
  shape: bbox 4.78 x 0.2 x 0.4672 mm, 14 faces (baked)
FEATURE [Part::Feature] Part__Feature227  label="Micro_USB_Plug_Connector003"
  Placement = pos=(255.557,33.7719,7.31475) rot=(0.577351,0.577352,-0.577348;4.18879rad)
  shape: bbox 7.5 x 6.35 x 1.35 mm, 54 faces (baked)
FEATURE [Part::Feature] Part__Feature228  label="2_C_3_4_6_1_1"
  Placement = pos=(205.099,-19.2281,8.57488) rot=(-1,-3e-06,-3e-06;1.57079rad)
  shape: bbox 73.52 x 148.2 x 33.63 mm, 876 faces (baked)
FEATURE [Part::Feature] Part__Feature025  label="2_BAT_3_4_6_1_1"
  Placement = pos=(205.099,-19.2281,8.57488) rot=(-1,-3e-06,-3e-06;1.57079rad)
  shape: bbox 14.36 x 15.32 x 64.97 mm, 83 faces (baked)
FEATURE [Part::Feature] Part__Feature026  label="2_B_3_4_6_1_1"
  Placement = pos=(205.099,-19.2281,8.57488) rot=(-1,-3e-06,-3e-06;1.57079rad)
  shape: bbox 78.1 x 152 x 64.86 mm, 1086 faces (baked)
FEATURE [Part::Feature] Part__Feature027  label="2_A_3_4_6_2_1"
  Placement = pos=(205.099,-19.2281,8.57488) rot=(-1,-3e-06,-3e-06;1.57079rad)
  shape: bbox 73.51 x 148.2 x 58.23 mm, 268 faces (baked)
FEATURE [Part::Feature] Part__Feature028  label="PH Pan head screw M2x0.40 x 009"
  Placement = pos=(254.945,24.1619,-1.82512) rot=(0,0,1;0rad)
  shape: bbox 4.006 x 4.006 x 7.57 mm, 32 faces (baked)
FEATURE [Part::Feature] Part__Feature029  label="Part 009"
  Placement = pos=(178.445,-83.8381,-39.4251) rot=(1,0,0;3.14159rad)
  shape: bbox 166 x 27.4 x 2 mm, 14 faces (baked)
FEATURE [Part::Feature] Part__Feature030  label="WPC20-28_3D"
  Placement = pos=(178.435,24.1794,31.5749) rot=(0,0,1;0rad)
  shape: bbox 201.1 x 281.1 x 21.57 mm, 1217 faces (baked)
FEATURE [Part::Feature] Part__Feature031  label="Cable Gland PG7-PG19 Sleeve_PG9"
  Placement = pos=(133.445,-133.413,10.8891) rot=(0,-0.01874,0.999824;3.14159rad)
  shape: bbox 11 x 8.207 x 11.28 mm, 4 faces (baked)
FEATURE [Part::Feature] Part__Feature032  label="Cable Gland PG7-PG19 Washer_PG9"
  Placement = pos=(133.445,-115.725,11.5524) rot=(0,-0.01874,0.999824;3.14159rad)
  shape: bbox 19.7 x 1.937 x 19.73 mm, 4 faces (baked)
FEATURE [Part::Feature] Part__Feature033  label="Cable Gland PG7-PG19 Lock Nut_PG9"
  Placement = pos=(133.445,-112.627,11.6686) rot=(1,0,0;0.037482rad)
  shape: bbox 24.34 x 6.322 x 24.32 mm, 29 faces (baked)
FEATURE [Part::Feature] Part__Feature034  label="Cable Gland PG7-PG19 Body_PG9"
  Placement = pos=(133.445,-118.823,11.4362) rot=(0,-0.01874,0.999824;3.14159rad)
  shape: bbox 19.4 x 32.49 x 17.68 mm, 129 faces (baked)
FEATURE [Part::Feature] Part__Feature035  label="Cable Gland PG7-PG19 Gland Nut_PG9"
  Placement = pos=(133.445,-130.065,11.0147) rot=(0.825324,-0.010582,0.56456;3.17253rad)
  shape: bbox 20.81 x 16.04 x 20.8 mm, 48 faces (baked)
FEATURE [App::Part] Cable_Gland_PG7_PG19__PG9__1_  label="Cable Gland PG7-PG19, PG9 <1>"
  Group = -> [Part__Feature031,Part__Feature032,Part__Feature033,Part__Feature034,Part__Feature035]
  Origin = -> Origin056
FEATURE [Part::Feature] Part__Feature036  label="id2"
  shape: bbox 274 x 229.5 x 2.5 mm, 53 faces (baked)
FEATURE [Part::Feature] Part__Feature037  label="id5"
  shape: bbox 251.2 x 70.58 x 83.44 mm, 48 faces (baked)
FEATURE [Part::Feature] Part__Feature038  label="id8"
  shape: bbox 253.5 x 2.737 x 2.883 mm, 6 faces (baked)
FEATURE [Part::MultiFuse] Fusion095  label="solarPanelMount"
  Placement = pos=(0,0,0) rot=(1,0,0;0.698132rad)
  Shapes = -> [Part__Feature036,Part__Feature037,Part__Feature038]
FEATURE [Part::Feature] Part__Feature039  label="Part 2"
  Placement = pos=(-0.595807,44.562,74.9733) rot=(1,0,0;3.14159rad)
  shape: bbox 272 x 434 x 1.1 mm, 24 faces (baked)
FEATURE [Part::Feature] Part__Feature041  label="id16"
  Placement = pos=(-0.595807,44.562,69.8733) rot=(0,0,1;0rad)
  shape: bbox 4 x 8.79 x 2 mm, 10 faces (baked)
FEATURE [Part::Feature] Part__Feature042  label="id21"
  Placement = pos=(-0.595807,44.562,69.8733) rot=(0,0,1;0rad)
  shape: bbox 125 x 42.28 x 0.1 mm, 8 faces (baked)
FEATURE [Part::Feature] Part__Feature043  label="id26"
  Placement = pos=(-0.595807,44.562,69.8733) rot=(0,0,1;0rad)
  shape: bbox 125 x 42.28 x 0.1 mm, 8 faces (baked)
FEATURE [Part::Feature] Part__Feature044  label="id31"
  Placement = pos=(-0.595807,44.562,69.8733) rot=(0,0,1;0rad)
  shape: bbox 4 x 8.79 x 2 mm, 10 faces (baked)
FEATURE [Part::Feature] Part__Feature045  label="id36"
  Placement = pos=(-0.595807,44.562,69.8733) rot=(0,0,1;0rad)
  shape: bbox 125 x 42.28 x 0.1 mm, 8 faces (baked)
FEATURE [Part::Feature] Part__Feature046  label="id41"
  Placement = pos=(-0.595807,44.562,69.8733) rot=(0,0,1;0rad)
  shape: bbox 4 x 4 x 2 mm, 4 faces (baked)
FEATURE [Part::Feature] Part__Feature047  label="id46"
  Placement = pos=(-0.595807,44.562,69.8733) rot=(0,0,1;0rad)
  shape: bbox 4 x 4 x 2 mm, 4 faces (baked)
FEATURE [Part::Feature] Part__Feature048  label="id51"
  Placement = pos=(-0.595807,44.562,69.8733) rot=(0,0,1;0rad)
  shape: bbox 125 x 42.28 x 0.1 mm, 8 faces (baked)
FEATURE [Part::Feature] Part__Feature229  label="id56"
  Placement = pos=(-0.595807,44.562,69.8733) rot=(0,0,1;0rad)
  shape: bbox 125 x 42.28 x 0.1 mm, 8 faces (baked)
FEATURE [Part::Feature] Part__Feature050  label="id61"
  Placement = pos=(-0.595807,44.562,69.8733) rot=(0,0,1;0rad)
  shape: bbox 4 x 4 x 2 mm, 4 faces (baked)
FEATURE [Part::Feature] Part__Feature051  label="id66"
  Placement = pos=(-0.595807,44.562,69.8733) rot=(0,0,1;0rad)
  shape: bbox 125 x 42.28 x 0.1 mm, 8 faces (baked)
FEATURE [Part::Feature] Part__Feature052  label="id71"
  Placement = pos=(-0.595807,44.562,69.8733) rot=(0,0,1;0rad)
  shape: bbox 125 x 40.44 x 0.1 mm, 6 faces (baked)
FEATURE [Part::Feature] Part__Feature053  label="id76"
  Placement = pos=(-0.595807,44.562,69.8733) rot=(0,0,1;0rad)
  shape: bbox 125 x 40.44 x 0.1 mm, 6 faces (baked)
FEATURE [Part::Feature] Part__Feature054  label="id81"
  Placement = pos=(-0.595807,44.562,69.8733) rot=(0,0,1;0rad)
  shape: bbox 125 x 42.28 x 0.1 mm, 8 faces (baked)
FEATURE [Part::Feature] Part__Feature055  label="id86"
  Placement = pos=(-0.595807,44.562,69.8733) rot=(0,0,1;0rad)
  shape: bbox 125 x 42.28 x 0.1 mm, 8 faces (baked)
FEATURE [Part::Feature] Part__Feature056  label="id91"
  Placement = pos=(-0.595807,44.562,69.8733) rot=(0,0,1;0rad)
  shape: bbox 125 x 42.28 x 0.1 mm, 8 faces (baked)
FEATURE [Part::Feature] Part__Feature057  label="id96"
  Placement = pos=(-0.595807,44.562,69.8733) rot=(0,0,1;0rad)
  shape: bbox 272 x 434 x 2 mm, 24 faces (baked)
FEATURE [Part::Feature] Part__Feature058  label="id101"
  Placement = pos=(-0.595807,44.562,69.8733) rot=(0,0,1;0rad)
  shape: bbox 125 x 42.28 x 0.1 mm, 8 faces (baked)
FEATURE [Part::Feature] Part__Feature059  label="id106"
  Placement = pos=(-0.595807,44.562,69.8733) rot=(0,0,1;0rad)
  shape: bbox 125 x 42.28 x 0.1 mm, 8 faces (baked)
FEATURE [Part::Feature] Part__Feature060  label="id111"
  Placement = pos=(-0.595807,44.562,69.8733) rot=(0,0,1;0rad)
  shape: bbox 125 x 42.28 x 0.1 mm, 8 faces (baked)
FEATURE [Part::Feature] Part__Feature061  label="id116"
  Placement = pos=(-0.595807,44.562,69.8733) rot=(0,0,1;0rad)
  shape: bbox 4 x 4 x 2 mm, 4 faces (baked)
FEATURE [Part::Feature] Part__Feature062  label="id121"
  Placement = pos=(-0.595807,44.562,69.8733) rot=(0,0,1;0rad)
  shape: bbox 4 x 4 x 2 mm, 4 faces (baked)
FEATURE [Part::Feature] Part__Feature063  label="id126"
  Placement = pos=(-0.595807,44.562,69.8733) rot=(0,0,1;0rad)
  shape: bbox 125 x 42.28 x 0.1 mm, 8 faces (baked)
FEATURE [Part::Feature] Part__Feature064  label="id131"
  Placement = pos=(-0.595807,44.562,69.8733) rot=(0,0,1;0rad)
  shape: bbox 4 x 4 x 2 mm, 4 faces (baked)
FEATURE [Part::Feature] Part__Feature065  label="id136"
  Placement = pos=(-0.595807,44.562,69.8733) rot=(0,0,1;0rad)
  shape: bbox 125 x 40.44 x 0.1 mm, 6 faces (baked)
FEATURE [Part::Feature] Part__Feature066  label="id141"
  Placement = pos=(-0.595807,44.562,69.8733) rot=(0,0,1;0rad)
  shape: bbox 274 x 436 x 2 mm, 18 faces (baked)
FEATURE [Part::Feature] Part__Feature067  label="id146"
  Placement = pos=(-0.595807,44.562,69.8733) rot=(0,0,1;0rad)
  shape: bbox 125 x 42.28 x 0.1 mm, 8 faces (baked)
FEATURE [Part::Feature] Part__Feature068  label="id151"
  Placement = pos=(-0.595807,44.562,69.8733) rot=(0,0,1;0rad)
  shape: bbox 125 x 42.28 x 0.1 mm, 8 faces (baked)
FEATURE [Part::Feature] Part__Feature069  label="id156"
  Placement = pos=(-0.595807,44.562,69.8733) rot=(0,0,1;0rad)
  shape: bbox 125 x 42.28 x 0.1 mm, 8 faces (baked)
FEATURE [Part::Feature] Part__Feature070  label="id161"
  Placement = pos=(-0.595807,44.562,69.8733) rot=(0,0,1;0rad)
  shape: bbox 125 x 40.44 x 0.1 mm, 6 faces (baked)
FEATURE [Part::Feature] Part__Feature076  label="Part 1"
  Placement = pos=(-0.595807,44.562,74.9733) rot=(1,0,0;3.14159rad)
  shape: bbox 274 x 436 x 1.1 mm, 18 faces (baked)
FEATURE [Part::Feature] Part__Feature077  label="JBox - 30 mm"
  Placement = pos=(-50.5959,-43.7114,69.8733) rot=(0,1,0;3.14159rad)
  shape: bbox 30.01 x 30.09 x 5.866 mm, 175 faces (baked)
FEATURE [App::Part] P120  label="solarPanel"
  Group = -> [Part__Feature039,Part__Feature041,Part__Feature042,Part__Feature043,Part__Feature044,Part__Feature045,Part__Feature046,Part__Feature047,Part__Feature048,Part__Feature229,Part__Feature050,Part__Feature051,Part__Feature052,Part__Feature053,Part__Feature054,Part__Feature055,Part__Feature056,Part__Feature057,Part__Feature058,Part__Feature059,Part__Feature060,Part__Feature061,Part__Feature062,+10 more]
  Origin = -> Origin058
  Placement = pos=(0.6,-120,-180) rot=(1,0,0;0.698132rad)
FEATURE [App::Part] V75_ASM__1_  label="V75 ASM <1>"
  Group = -> [Part__Feature217,Part__Feature218,Part__Feature219,Part__Feature220,Part__Feature221,Part__Feature222,Part__Feature223,Part__Feature224,Part__Feature225,Part__Feature226,Part__Feature227,Part__Feature228,Part__Feature025,Part__Feature026,Part__Feature027]
  Origin = -> Origin055
  Placement = pos=(6,15.97,20) rot=(0,0,1;0rad)
FEATURE [App::Part] E305__20x28x7cm_  label="box"
  Group = -> [Part__Feature204,Part__Feature205,Part__Feature206,Part__Feature207,Part__Feature208,Part__Feature209,Part__Feature210,Cable_Gland_PG7_PG19__PG13_5__1_,Part__Feature216,V75_ASM__1_,Part__Feature028,Part__Feature029,Part__Feature030,Cable_Gland_PG7_PG19__PG9__1_]
  Origin = -> Origin057
  Placement = pos=(175.533,-124.11,-130.152) rot=(0,-0.939693,-0.34202;3.14159rad)
FEATURE [Part::Cylinder] Cylinder154  label="base014"
  Angle = 360
  AttacherType = Attacher::AttachEngine3D
  FirstAngle = 0
  Height = 4.5
  Placement = pos=(136,0,65) rot=(0,0,1;0rad)
  Radius = 40
  SecondAngle = 0
FEATURE [Part::Cylinder] Cylinder155  label="baseCut003"
  Angle = 360
  AttacherType = Attacher::AttachEngine3D
  FirstAngle = 0
  Height = 7
  Placement = pos=(5,0,74) rot=(0,0,1;0rad)
  Radius = 24
  SecondAngle = 0
FEATURE [Part::Cylinder] Cylinder156
  Angle = 360
  AttacherType = Attacher::AttachEngine3D
  FirstAngle = 0
  Height = 1
  Placement = pos=(134,32.6,65) rot=(0,0,1;0rad)
  Radius = 5.5
  SecondAngle = 0
FEATURE [Part::Cylinder] Cylinder157
  Angle = 360
  AttacherType = Attacher::AttachEngine3D
  FirstAngle = 0
  Height = 5.82
  Placement = pos=(0,-21,0) rot=(0,0,1;0rad)
  Radius = 5
  SecondAngle = 0
FEATURE [Part::Cylinder] Cylinder158
  Angle = 360
  AttacherType = Attacher::AttachEngine3D
  FirstAngle = 0
  Height = 5.82
  Placement = pos=(20.5,-21,0) rot=(0,0,1;0rad)
  Radius = 5
  SecondAngle = 0
  expr: Radius = 5
FEATURE [Part::Cylinder] Cylinder159
  Angle = 360
  AttacherType = Attacher::AttachEngine3D
  FirstAngle = 0
  Height = 5.82
  Placement = pos=(0,-21,0) rot=(0,0,1;0rad)
  Radius = 5
  SecondAngle = 0
FEATURE [Part::Cylinder] Cylinder160
  Angle = 360
  AttacherType = Attacher::AttachEngine3D
  FirstAngle = 0
  Height = 5.82
  Placement = pos=(20.5,-21,0) rot=(0,0,1;0rad)
  Radius = 5
  SecondAngle = 0
FEATURE [Part::Cylinder] Cylinder161
  Angle = 360
  AttacherType = Attacher::AttachEngine3D
  FirstAngle = 0
  Height = 10
  Placement = pos=(0,-21,0) rot=(0,0,1;0rad)
  Radius = 2
  SecondAngle = 0
FEATURE [Part::Cylinder] Cylinder162
  Angle = 360
  AttacherType = Attacher::AttachEngine3D
  FirstAngle = 0
  Height = 10
  Placement = pos=(20.5,-21,0) rot=(0,0,1;0rad)
  Radius = 2
  SecondAngle = 0
FEATURE [Part::Cylinder] Cylinder163
  Angle = 360
  AttacherType = Attacher::AttachEngine3D
  FirstAngle = 0
  Height = 10
  Placement = pos=(0,-21,0) rot=(0,0,1;0rad)
  Radius = 2
  SecondAngle = 0
FEATURE [Part::Cylinder] Cylinder164
  Angle = 360
  AttacherType = Attacher::AttachEngine3D
  FirstAngle = 0
  Height = 10
  Placement = pos=(20.5,-21,0) rot=(0,0,1;0rad)
  Radius = 2
  SecondAngle = 0
FEATURE [Part::MultiFuse] Fusion097  label="m3HeatSetCuts021"
  Placement = pos=(-5,39,70) rot=(0,0,1;0rad)
  Shapes = -> [Cylinder158,Cylinder157]
FEATURE [Part::MultiFuse] Fusion098  label="m3HeatSetCuts022"
  Placement = pos=(-5,3,70) rot=(0,0,1;0rad)
  Shapes = -> [Cylinder160,Cylinder159]
FEATURE [Part::MultiFuse] Fusion099  label="m3HeatSetCuts023"
  Placement = pos=(128.75,10,-1) rot=(0,0,1;0rad)
  Shapes = -> [Fusion098,Fusion097]
FEATURE [Part::MultiFuse] Fusion103  label="m3HeatSetCuts025"
  Placement = pos=(-5,39,70) rot=(0,0,1;0rad)
  Shapes = -> [Cylinder162,Cylinder161]
FEATURE [Part::MultiFuse] Fusion104  label="m3HeatSetCuts026"
  Placement = pos=(-5,3,70) rot=(0,0,1;0rad)
  Shapes = -> [Cylinder164,Cylinder163]
FEATURE [Part::MultiFuse] Fusion102  label="m3HeatSetCuts024"
  Placement = pos=(128.75,10,-1) rot=(0,0,1;0rad)
  Shapes = -> [Fusion104,Fusion103]
FEATURE [Part::Sphere] Sphere005  label="SphereBase003"
  Angle1 = 0
  Angle2 = 12
  Angle3 = 360
  AttacherType = Attacher::AttachEngine3D
  Placement = pos=(5,0,74) rot=(0,0,1;0rad)
  Radius = 27.5
FEATURE [Part::Cut] Cut053
  Base = -> Sphere005
  Placement = pos=(131,0,-5) rot=(0,0,1;0rad)
  Tool = -> Cylinder155
FEATURE [Part::MultiFuse] Fusion100  label="Base003"
  Placement = pos=(-2,10,0) rot=(0,0,1;0rad)
  Shapes = -> [Cut053,Cylinder154]
FEATURE [Part::MultiFuse] Fusion101  label="lightModule010"
  Shapes = -> [Fusion100,Cylinder156,Fusion099]
FEATURE [Part::Feature] Part__Feature230  label="ANT-868-PW-QW-UFL-BODY002"
  shape: bbox 15.69 x 84 x 15.69 mm, 56 faces (baked)
FEATURE [Part::Feature] Part__Feature231  label="Screw002"
  Placement = pos=(0,-7.05,0) rot=(0,0,1;0rad)
  shape: bbox 7.002 x 7.052 x 7.002 mm, 20 faces (baked)
FEATURE [Part::Feature] Part__Feature232  label="Ring002"
  shape: bbox 9.2 x 6 x 9.2 mm, 8 faces, 2 solids (baked)
FEATURE [Part::Compound] Compound003  label="loraAntenna001"
  Links = -> [Part__Feature232,Part__Feature230,Part__Feature231]
  Placement = pos=(-0.5,-512,-305.5) rot=(0.57735,-0.57735,-0.57735;2.0944rad)
FEATURE [Sketcher::SketchObject] Sketch136
  FullyConstrained = true
  Placement = pos=(-20,0,0) rot=(0.57735,0.57735,0.57735;2.0944rad)
  sketch-geometry (8):
    g0: LineSegment StartX=-299.827 StartY=3.70134 StartZ=0 EndX=-297.77 EndY=1.25 EndZ=0
    g1: LineSegment StartX=-297.77 StartY=1.25 StartZ=0 EndX=-279 EndY=17 EndZ=0
    g2: LineSegment StartX=-299.827 StartY=3.70134 StartZ=0 EndX=-328.073 EndY=-20 EndZ=0
    g3: LineSegment StartX=-328.073 StartY=-20 StartZ=0 EndX=-279 EndY=-20 EndZ=0
    g4: LineSegment StartX=-279 StartY=-20 StartZ=0 EndX=-279 EndY=17 EndZ=0
    g5: LineSegment StartX=-306.073 StartY=-12 StartZ=0 EndX=-284.073 EndY=-12 EndZ=0
    g6: LineSegment StartX=-284.073 StartY=-12 StartZ=0 EndX=-284.073 EndY=6.46019 EndZ=0
    g7: LineSegment StartX=-284.073 StartY=6.46019 StartZ=0 EndX=-306.073 EndY=-12 EndZ=0
  constraints (24):
    c: Coincident(g1,g0)
    c: DistanceX(g1) = -279
    c: DistanceY(g1) = 17
    c: Angle(g1,g0) = 1.5708
    c: Angle(g1) = 0.698132
    c: Distance(g0) = 3.2
    c: DistanceY(g0) = 1.25
    c: Coincident(g2,g0)
    c: DistanceY(g2) = -20
    c: Coincident(g3,g2)
    c: Horizontal(g3)
    c: Coincident(g4,g3)
    c: Coincident(g4,g1)
    c: Vertical(g4)
    c: Angle(g3,g2) = 0.698132
    c: Horizontal(g5)
    c: Coincident(g6,g5)
    c: Vertical(g6)
    c: Coincident(g7,g6)
    c: Coincident(g7,g5)
    c: DistanceY(g2,g5) = 8
    c: Angle(g5,g7) = 0.698132
    c: DistanceX(g5,g5) = 22
    c: DistanceX(g2,g5) = 22
FEATURE [Sketcher::SketchObject] Sketch137
  FullyConstrained = true
  Placement = pos=(0,0,-20) rot=(0,0,1;0rad)
  sketch-geometry (5):
    g0: LineSegment StartX=20 StartY=-256.531 StartZ=0 EndX=20 EndY=-234 EndZ=0
    g1: LineSegment StartX=20 StartY=-234 StartZ=0 EndX=-20 EndY=-234 EndZ=0
    g2: LineSegment StartX=-20 StartY=-234 StartZ=0 EndX=-20 EndY=-256.531 EndZ=0
    g3: LineSegment StartX=-20 StartY=-256.531 StartZ=0 EndX=0 EndY=-242 EndZ=0
    g4: LineSegment StartX=0 StartY=-242 StartZ=0 EndX=20 EndY=-256.531 EndZ=0
  constraints (15):
    c: Vertical(g0)
    c: Coincident(g1,g0)
    c: Horizontal(g1)
    c: Coincident(g2,g1)
    c: Vertical(g2)
    c: Coincident(g3,g2)
    c: PointOnObject(g3,g-2)
    c: Coincident(g4,g3)
    c: Coincident(g4,g0)
    c: Angle(g3,g4) = 1.88496
    c: DistanceY(g3) = -242
    c: DistanceY(g2,g0) = 0
    c: DistanceX(g2) = -20
    c: DistanceX(g0) = 20
    c: DistanceY(g1) = -234
FEATURE [Part::Extrusion] Extrude040  label="tSllotHoldCut"
  Base = -> Sketch137
  Dir = (0,0,1)
  DirMode = 2
  FaceMakerClass = Part::FaceMakerBullseye
  LengthFwd = 37
  LengthRev = 0
  Solid = true
  Symmetric = false
FEATURE [Part::Extrusion] Extrude041  label="solarPanelMount002"
  Base = -> Sketch136
  Dir = (1,-2e-16,2e-16)
  DirMode = 2
  FaceMakerClass = Part::FaceMakerBullseye
  LengthFwd = 40
  LengthRev = 0
  Solid = true
  Symmetric = false
FEATURE [Part::Cut] Cut056  label="tSlotHold001"
  Base = -> Extrude038
  Tool = -> Extrude040
FEATURE [Part::MultiFuse] Fusion106  label="srs"
  Shapes = -> [Fusion094,Extrude041,Cut056]
FEATURE [Part::Cylinder] Cylinder167  label="m6Cut"
  Angle = 360
  AttacherType = Attacher::AttachEngine3D
  FirstAngle = 0
  Height = 10
  Placement = pos=(0,-263.25,14.5) rot=(0,0,1;0rad)
  Radius = 5.75
  SecondAngle = 0
FEATURE [Sketcher::SketchObject] Sketch067
  FullyConstrained = true
  Placement = pos=(0,0,-20) rot=(0,0,1;0rad)
  sketch-geometry (6):
    g0: LineSegment StartX=9 StartY=-360 StartZ=0 EndX=9 EndY=-400 EndZ=0
    g1: LineSegment StartX=9 StartY=-400 StartZ=0 EndX=-9 EndY=-400 EndZ=0
    g2: Circle CenterX=0 CenterY=-390 CenterZ=0 NormalX=0 NormalY=0 NormalZ=1 AngleXU=0 Radius=3.25
    g3: Circle CenterX=0 CenterY=-371 CenterZ=0 NormalX=0 NormalY=0 NormalZ=1 AngleXU=0 Radius=3.25
    g4: LineSegment StartX=9 StartY=-360 StartZ=0 EndX=-9 EndY=-360 EndZ=0
    g5: LineSegment StartX=-9 StartY=-360 StartZ=0 EndX=-9 EndY=-400 EndZ=0
  constraints (18):
    c: Vertical(g0)
    c: Coincident(g1,g0)
    c: Horizontal(g1)
    c: Distance(g1) = 18
    c: Distance(g0) = 40
    c: DistanceY(g2,g3) = 19
    c: Radius(g2) = 3.25
    c: Radius(g3) = 3.25
    c: DistanceX(g2,g3) = 0
    c: Coincident(g4,g0)
    c: Horizontal(g4)
    c: Coincident(g5,g4)
    c: Coincident(g5,g1)
    c: Vertical(g5)
    c: DistanceX(g1,g2) = 9
    c: DistanceY(g1,g2) = 10
    c: DistanceY(g4) = -360
    c: DistanceX(g3) = 0
FEATURE [Part::Cut] Cut042  label="SLS"
  Base = -> Cut041
  Tool = -> Box042
FEATURE [Part::Cylinder] Cylinder168
  Angle = 360
  AttacherType = Attacher::AttachEngine3D
  FirstAngle = 0
  Height = 13
  Placement = pos=(0,0,0) rot=(0,1,0;3.14159rad)
  Radius = 35.35
  SecondAngle = 0
FEATURE [Sketcher::SketchObject] Sketch138
  FullyConstrained = true
  sketch-geometry (6):
    g0: Circle CenterX=0 CenterY=56.295 CenterZ=0 NormalX=0 NormalY=0 NormalZ=1 AngleXU=0 Radius=3.2
    g1: Circle CenterX=0 CenterY=75.345 CenterZ=0 NormalX=0 NormalY=0 NormalZ=1 AngleXU=0 Radius=3.2
    g2: LineSegment StartX=-12 StartY=84.875 StartZ=0 EndX=12 EndY=84.875 EndZ=0
    g3: LineSegment StartX=12 StartY=84.875 StartZ=0 EndX=12 EndY=0 EndZ=0
    g4: LineSegment StartX=12 StartY=0 StartZ=0 EndX=-12 EndY=0 EndZ=0
    g5: LineSegment StartX=-12 StartY=0 StartZ=0 EndX=-12 EndY=84.875 EndZ=0
  constraints (18):
    c: PointOnObject(g0,g-2)
    c: PointOnObject(g1,g-2)
    c: DistanceY(g0,g1) = 19.05
    c: Equal(g0,g1)
    c: Diameter(g0) = 6.4
    c: Coincident(g2,g3)
    c: Coincident(g3,g4)
    c: Coincident(g4,g5)
    c: Coincident(g5,g2)
    c: Horizontal(g2)
    c: Horizontal(g4)
    c: Vertical(g3)
    c: Vertical(g5)
    c: DistanceY(g1,g2) = 9.53
    c: DistanceX(g2,g2) = 24
    c: DistanceX(g2,g1) = 12
    c: DistanceY(g4,g2) = 84.875
    c: DistanceY(g4,g-1) = 0
FEATURE [Part::Extrusion] Extrude042
  Base = -> Sketch138
  Dir = (0,0,1)
  DirMode = 2
  FaceMakerClass = Part::FaceMakerBullseye
  LengthFwd = 13
  LengthRev = 0
  Reversed = true
  Solid = true
  Symmetric = false
FEATURE [Sketcher::SketchObject] Sketch001
  FullyConstrained = true
  Placement = pos=(0,0,-13) rot=(0,0,1;0rad)
  sketch-geometry (4):
    g0: LineSegment StartX=-9.58 StartY=84.875 StartZ=0 EndX=9.58 EndY=84.875 EndZ=0
    g1: LineSegment StartX=9.58 StartY=84.875 StartZ=0 EndX=9.58 EndY=35.355 EndZ=0
    g2: LineSegment StartX=9.58 StartY=35.355 StartZ=0 EndX=-9.58 EndY=35.355 EndZ=0
    g3: LineSegment StartX=-9.58 StartY=35.355 StartZ=0 EndX=-9.58 EndY=84.875 EndZ=0
  constraints (12):
    c: Coincident(g0,g1)
    c: Coincident(g1,g2)
    c: Coincident(g2,g3)
    c: Coincident(g3,g0)
    c: Horizontal(g0)
    c: Horizontal(g2)
    c: Vertical(g1)
    c: Vertical(g3)
    c: DistanceX(g0,g0) = 19.16
    c: DistanceX(g2) = -9.58
    c: DistanceY(g2) = 35.355
    c: DistanceY(g3,g3) = 49.52
FEATURE [Part::Extrusion] Extrude001
  Base = -> Sketch001
  Dir = (0,0,1)
  DirMode = 2
  FaceMakerClass = Part::FaceMakerBullseye
  LengthFwd = 10.4
  LengthRev = 0
  Solid = true
  Symmetric = false
FEATURE [Part::Sphere] Sphere
  Angle1 = 0
  Angle2 = 90
  Angle3 = 360
  AttacherType = Attacher::AttachEngine3D
  Radius = 35.35
FEATURE [Part::MultiFuse] Fusion107
  Shapes = -> [Sphere,Extrude042,Cylinder168]
FEATURE [Part::Cut] Cut057  label="rg15"
  Base = -> Fusion107
  Placement = pos=(0,-450,-7) rot=(0,0,1;0rad)
  Tool = -> Extrude001
FEATURE [Sketcher::SketchObject] Sketch139
  FullyConstrained = true
  Placement = pos=(0,0,-20) rot=(0,0,1;0rad)
  sketch-geometry (6):
    g0: LineSegment StartX=-9.25 StartY=-279 StartZ=0 EndX=9.25 EndY=-279 EndZ=0
    g1: LineSegment StartX=9.25 StartY=-279 StartZ=0 EndX=9.25 EndY=-405 EndZ=0
    g2: LineSegment StartX=9.25 StartY=-405 StartZ=0 EndX=-9.25 EndY=-405 EndZ=0
    g3: LineSegment StartX=-9.25 StartY=-405 StartZ=0 EndX=-9.25 EndY=-279 EndZ=0
    g4: Circle CenterX=0 CenterY=-393.7 CenterZ=0 NormalX=0 NormalY=0 NormalZ=1 AngleXU=0 Radius=3.5
    g5: Circle CenterX=0 CenterY=-374.54 CenterZ=0 NormalX=0 NormalY=0 NormalZ=1 AngleXU=0 Radius=3.5
  constraints (18):
    c: Coincident(g0,g1)
    c: Coincident(g1,g2)
    c: Coincident(g2,g3)
    c: Coincident(g3,g0)
    c: Horizontal(g0)
    c: Horizontal(g2)
    c: Vertical(g1)
    c: Vertical(g3)
    c: DistanceX(g2,g2) = 18.5
    c: DistanceX(g2) = -9.25
    c: DistanceY(g2) = -405
    c: PointOnObject(g4,g-2)
    c: PointOnObject(g5,g-2)
    c: Equal(g4,g5)
    c: Diameter(g4) = 7
    c: DistanceY(g4,g5) = 19.16
    c: DistanceY(g4) = -393.7
    c: DistanceY(g1,g1) = 126
FEATURE [Part::Feature] Part__Feature233  label="m6s001"
  Placement = pos=(0,-409.05,-16.5) rot=(0,0,1;0rad)
  shape: bbox 10.31 x 10.31 x 31.75 mm, 372 faces (baked)
FEATURE [Part::Feature] Part__Feature234  label="m6s"
  Placement = pos=(0,-390,-16.5) rot=(0,0,1;0rad)
  shape: bbox 10.31 x 10.31 x 31.75 mm, 372 faces (baked)
FEATURE [Part::MultiFuse] Fusion108  label="m6s002"
  Placement = pos=(0,15.35,0) rot=(0,0,1;0rad)
  Shapes = -> [Part__Feature233,Part__Feature234]
FEATURE [Part::Feature] Part__Feature235  label="M6Nut"
  Placement = pos=(0,-393.7,-20) rot=(1,0,0;3.14159rad)
  shape: bbox 25.4 x 11.25 x 3.15 mm, 18 faces (baked)
FEATURE [Part::Feature] Part__Feature236  label="M6Nut001"
  Placement = pos=(0,-374.65,-20) rot=(-1,0,0;3.14159rad)
  shape: bbox 25.4 x 11.25 x 3.15 mm, 18 faces (baked)
FEATURE [Part::Extrusion] Extrude043  label="beam"
  Base = -> Sketch139
  Dir = (0,0,1)
  DirMode = 2
  FaceMakerClass = Part::FaceMakerBullseye
  LengthFwd = 10
  LengthRev = 0
  Solid = true
  Symmetric = false
FEATURE [Part::MultiFuse] Fusion109  label="m6Nuts"
  Shapes = -> [Part__Feature235,Part__Feature236]
FEATURE [Part::MultiFuse] Fusion110  label="m6s003"
  Shapes = -> [Fusion108,Fusion109]
FEATURE [Part::Feature] Part__Feature237  label="m4Nut"
  Placement = pos=(0,-393.75,-15) rot=(1,0,0;4.71239rad)
  shape: bbox 8.084 x 2.201 x 8.084 mm, 26 faces (baked)
FEATURE [Part::Cylinder] Cylinder169  label="m2HeatSetInsets020"
  Angle = 360
  AttacherType = Attacher::AttachEngine3D
  FirstAngle = 0
  Height = 10
  Placement = pos=(-35,0,65) rot=(0,0,1;0rad)
  Radius = 2
  SecondAngle = 0
  expr: Radius = 2
FEATURE [Part::Cylinder] Cylinder170  label="m2HeatSetInsets021"
  Angle = 360
  AttacherType = Attacher::AttachEngine3D
  FirstAngle = 0
  Height = 10
  Placement = pos=(35,0,65) rot=(0,0,1;0rad)
  Radius = 2
  SecondAngle = 0
FEATURE [Part::Cylinder] Cylinder171  label="m2HeatSetInsets022"
  Angle = 360
  AttacherType = Attacher::AttachEngine3D
  FirstAngle = 0
  Height = 10
  Placement = pos=(0,35,65) rot=(0,0,1;0rad)
  Radius = 2
  SecondAngle = 0
FEATURE [Part::Cylinder] Cylinder172  label="m2HeatSetInsets023"
  Angle = 360
  AttacherType = Attacher::AttachEngine3D
  FirstAngle = 0
  Height = 10
  Placement = pos=(0,-35,65) rot=(0,0,1;0rad)
  Radius = 2
  SecondAngle = 0
  expr: Radius = 2
FEATURE [Part::MultiFuse] Fusion111  label="m3DomeCuts"
  Placement = pos=(0,-374,-75) rot=(0,0,-1;0.785398rad)
  Shapes = -> [Cylinder169,Cylinder170,Cylinder171,Cylinder172]
FEATURE [Part::Cylinder] Cylinder165  label="WireCut004"
  Angle = 360
  AttacherType = Attacher::AttachEngine3D
  FirstAngle = 0
  Height = 60
  Placement = pos=(134,32.6,20) rot=(0,0,1;0rad)
  Radius = 2.5
  SecondAngle = 0
FEATURE [Part::MultiFuse] Fusion105  label="lightModuleCut005"
  Shapes = -> [Fusion102,Cylinder165]
FEATURE [Part::Cut] Cut054  label="lightModule009"
  Base = -> Fusion101
  Placement = pos=(-134,-384,-74) rot=(0,0,1;0rad)
  Tool = -> Fusion105
FEATURE [Part::Cylinder] Cylinder173  label="base015"
  Angle = 360
  AttacherType = Attacher::AttachEngine3D
  FirstAngle = 0
  Height = 4.5
  Placement = pos=(136,0,65) rot=(0,0,1;0rad)
  Radius = 40
  SecondAngle = 0
FEATURE [Part::Cylinder] Cylinder174  label="baseCut004"
  Angle = 360
  AttacherType = Attacher::AttachEngine3D
  FirstAngle = 0
  Height = 7
  Placement = pos=(5,0,74) rot=(0,0,1;0rad)
  Radius = 24
  SecondAngle = 0
FEATURE [Part::Cylinder] Cylinder175
  Angle = 360
  AttacherType = Attacher::AttachEngine3D
  FirstAngle = 0
  Height = 1
  Placement = pos=(134,32.6,65) rot=(0,0,1;0rad)
  Radius = 5.5
  SecondAngle = 0
FEATURE [Part::Cylinder] Cylinder176
  Angle = 360
  AttacherType = Attacher::AttachEngine3D
  FirstAngle = 0
  Height = 5.82
  Placement = pos=(0,-21,0) rot=(0,0,1;0rad)
  Radius = 5
  SecondAngle = 0
FEATURE [Part::Cylinder] Cylinder177
  Angle = 360
  AttacherType = Attacher::AttachEngine3D
  FirstAngle = 0
  Height = 5.82
  Placement = pos=(20.5,-21,0) rot=(0,0,1;0rad)
  Radius = 5
  SecondAngle = 0
  expr: Radius = 5
FEATURE [Part::Cylinder] Cylinder178
  Angle = 360
  AttacherType = Attacher::AttachEngine3D
  FirstAngle = 0
  Height = 5.82
  Placement = pos=(0,-21,0) rot=(0,0,1;0rad)
  Radius = 5
  SecondAngle = 0
FEATURE [Part::Cylinder] Cylinder179
  Angle = 360
  AttacherType = Attacher::AttachEngine3D
  FirstAngle = 0
  Height = 5.82
  Placement = pos=(20.5,-21,0) rot=(0,0,1;0rad)
  Radius = 5
  SecondAngle = 0
FEATURE [Part::Cylinder] Cylinder180
  Angle = 360
  AttacherType = Attacher::AttachEngine3D
  FirstAngle = 0
  Height = 10
  Placement = pos=(0,-21,0) rot=(0,0,1;0rad)
  Radius = 2
  SecondAngle = 0
FEATURE [Part::Cylinder] Cylinder181
  Angle = 360
  AttacherType = Attacher::AttachEngine3D
  FirstAngle = 0
  Height = 10
  Placement = pos=(20.5,-21,0) rot=(0,0,1;0rad)
  Radius = 2
  SecondAngle = 0
FEATURE [Part::Cylinder] Cylinder182
  Angle = 360
  AttacherType = Attacher::AttachEngine3D
  FirstAngle = 0
  Height = 10
  Placement = pos=(0,-21,0) rot=(0,0,1;0rad)
  Radius = 2
  SecondAngle = 0
FEATURE [Part::Cylinder] Cylinder183
  Angle = 360
  AttacherType = Attacher::AttachEngine3D
  FirstAngle = 0
  Height = 10
  Placement = pos=(20.5,-21,0) rot=(0,0,1;0rad)
  Radius = 2
  SecondAngle = 0
FEATURE [Part::MultiFuse] Fusion112  label="m3HeatSetCuts027"
  Placement = pos=(-5,39,70) rot=(0,0,1;0rad)
  Shapes = -> [Cylinder177,Cylinder176]
FEATURE [Part::MultiFuse] Fusion113  label="m3HeatSetCuts028"
  Placement = pos=(-5,3,70) rot=(0,0,1;0rad)
  Shapes = -> [Cylinder179,Cylinder178]
FEATURE [Part::MultiFuse] Fusion114  label="m3HeatSetCuts029"
  Placement = pos=(128.75,10,-1) rot=(0,0,1;0rad)
  Shapes = -> [Fusion113,Fusion112]
FEATURE [Part::MultiFuse] Fusion118  label="m3HeatSetCuts031"
  Placement = pos=(-5,39,70) rot=(0,0,1;0rad)
  Shapes = -> [Cylinder181,Cylinder180]
FEATURE [Part::MultiFuse] Fusion119  label="m3HeatSetCuts032"
  Placement = pos=(-5,3,70) rot=(0,0,1;0rad)
  Shapes = -> [Cylinder183,Cylinder182]
FEATURE [Part::MultiFuse] Fusion117  label="m3HeatSetCuts030"
  Placement = pos=(128.75,10,-1) rot=(0,0,1;0rad)
  Shapes = -> [Fusion119,Fusion118]
FEATURE [Part::Sphere] Sphere006  label="SphereBase004"
  Angle1 = 0
  Angle2 = 12
  Angle3 = 360
  AttacherType = Attacher::AttachEngine3D
  Placement = pos=(5,0,74) rot=(0,0,1;0rad)
  Radius = 27.5
FEATURE [Part::Cut] Cut058
  Base = -> Sphere006
  Placement = pos=(131,0,-5) rot=(0,0,1;0rad)
  Tool = -> Cylinder174
FEATURE [Part::MultiFuse] Fusion115  label="Base004"
  Placement = pos=(-2,10,0) rot=(0,0,1;0rad)
  Shapes = -> [Cut058,Cylinder173]
FEATURE [Part::MultiFuse] Fusion116  label="lightModule012"
  Shapes = -> [Fusion115,Cylinder175,Fusion114]
FEATURE [Part::MultiFuse] Fusion120
  Shapes = -> [Fusion111,Fusion117]
FEATURE [Part::MultiFuse] Fusion096  label="mainModule"
  Placement = pos=(0,0,239.25) rot=(0,0,1;0rad)
  Shapes = -> [E305__20x28x7cm_,Fusion095,P120]
FEATURE [Part::Cut] Cut059
  Base = -> Fusion116
  Tool = -> Fusion120
